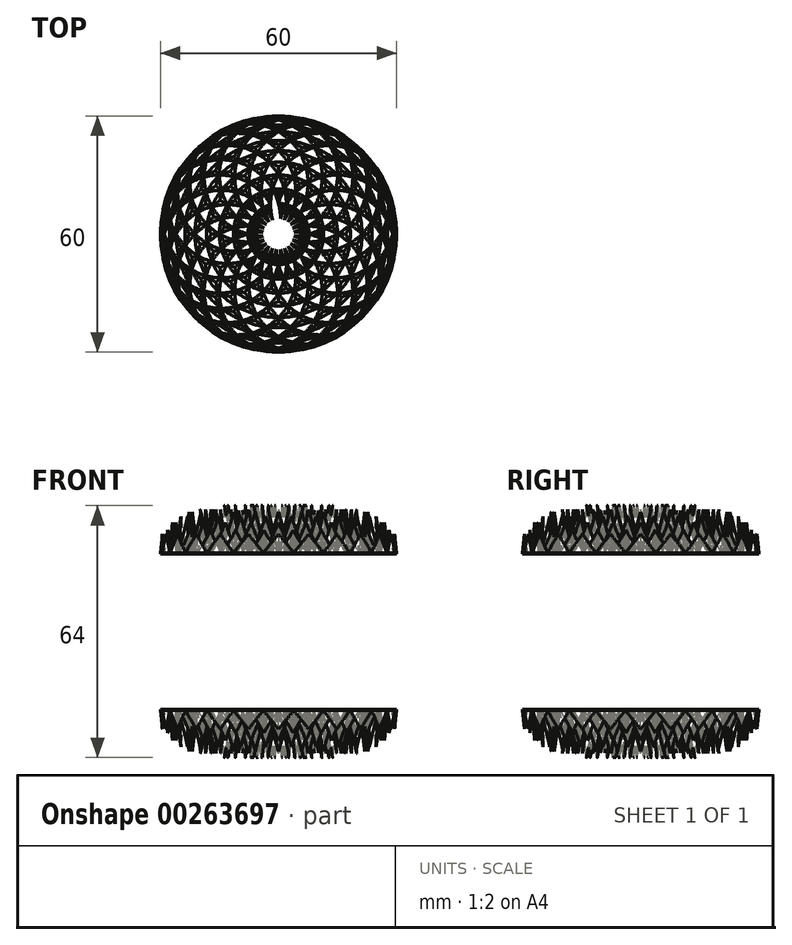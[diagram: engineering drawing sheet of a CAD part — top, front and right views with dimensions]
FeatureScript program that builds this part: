
annotation { "Feature Type Name" : "Feature", "Feature Type Description" : "" }
export const myFeature = defineFeature(function(context is Context, id is Id, definition is map)
    precondition{}
    {
        {
            var Q0;
            Q0=qCreatedBy(makeId("Top.planeOp"),FACE);
            var sketch = newSketch(context, id + "F0", { "sketchPlane" : qUnion([Q0])});
            skCircle(sketch, "E0", {"center": v(0, 0) * mm, "radius": 15 * mm});
            skLineSegment(sketch, "E1", {"start": v(-15, 0) * mm, "end": v(15, 0) * mm, "construction": true});
            skLineSegment(sketch, "E2", {"start": v(0, 15) * mm, "end": v(0, -15) * mm, "construction": true});
            skCircle(sketch, "E3", {"center": v(15, 0) * mm, "radius": 15 * mm});
            skCircle(sketch, "E4", {"center": v(7.5, 13) * mm, "radius": 15 * mm});
            skCircle(sketch, "E5", {"center": v(7.5, -13) * mm, "radius": 15 * mm});
            skCircle(sketch, "E6", {"center": v(-7.5, 13) * mm, "radius": 15 * mm});
            skCircle(sketch, "E7", {"center": v(-7.5, -13) * mm, "radius": 15 * mm});
            skCircle(sketch, "E8", {"center": v(-15, 0) * mm, "radius": 15 * mm});
            skLineSegment(sketch, "E9", {"start": v(0, 0) * mm, "end": v(22.5, 13) * mm, "construction": true});
            skCircle(sketch, "E10", {"center": v(13, 7.5) * mm, "radius": 15 * mm});
            skCircle(sketch, "E11", {"center": v(13, -7.5) * mm, "radius": 15 * mm});
            skCircle(sketch, "E12", {"center": v(0, -15) * mm, "radius": 15 * mm});
            skCircle(sketch, "E13", {"center": v(-13, -7.5) * mm, "radius": 15 * mm});
            skCircle(sketch, "E14", {"center": v(-13, 7.5) * mm, "radius": 15 * mm});
            skCircle(sketch, "E15", {"center": v(0, 15) * mm, "radius": 15 * mm});
            skLineSegment(sketch, "E16", {"start": v(7.5, 2) * mm, "end": v(20.5, 5.5) * mm, "construction": true});
            skCircle(sketch, "E17", {"center": v(14.49, 3.88) * mm, "radius": 15 * mm});
            skCircle(sketch, "E18", {"center": v(10.6, -10.6) * mm, "radius": 15 * mm});
            skCircle(sketch, "E19", {"center": v(-3.88, -14.49) * mm, "radius": 15 * mm});
            skCircle(sketch, "E20", {"center": v(-14.49, -3.88) * mm, "radius": 15 * mm});
            skCircle(sketch, "E21", {"center": v(-10.6, 10.6) * mm, "radius": 15 * mm});
            skCircle(sketch, "E22", {"center": v(3.88, 14.49) * mm, "radius": 15 * mm});
            skLineSegment(sketch, "E23", {"start": v(-2, 7.5) * mm, "end": v(-5.5, 20.5) * mm, "construction": true});
            skCircle(sketch, "E24", {"center": v(-3.88, 14.49) * mm, "radius": 15 * mm});
            skCircle(sketch, "E25", {"center": v(10.6, 10.6) * mm, "radius": 15 * mm});
            skCircle(sketch, "E26", {"center": v(14.49, -3.88) * mm, "radius": 15 * mm});
            skCircle(sketch, "E27", {"center": v(3.88, -14.49) * mm, "radius": 15 * mm});
            skCircle(sketch, "E28", {"center": v(-10.6, -10.6) * mm, "radius": 15 * mm});
            skCircle(sketch, "E29", {"center": v(-14.49, 3.88) * mm, "radius": 15 * mm});
            skCircle(sketch, "E30", {"center": v(0, 0) * mm, "radius": 18.26 * mm});
            skLineSegment(sketch, "E31", {"start": v(-6.99, 16.87) * mm, "end": v(-2.38, 18.1) * mm, "construction": true});
            skCircle(sketch, "E32", {"center": v(0, 0) * mm, "radius": 21.21 * mm});
            skLineSegment(sketch, "E33", {"start": v(0, 0) * mm, "end": v(7.5, 28) * mm, "construction": true});
            skCircle(sketch, "E34", {"center": v(0, 0) * mm, "radius": 28.98 * mm});
            skLineSegment(sketch, "E35", {"start": v(0, 0) * mm, "end": v(3.1, 23.6) * mm, "construction": true});
            skCircle(sketch, "E36", {"center": v(0, 0) * mm, "radius": 23.8 * mm});
            skLineSegment(sketch, "E37", {"start": v(0, 0) * mm, "end": v(-3.62, 27.48) * mm, "construction": true});
            skCircle(sketch, "E38", {"center": v(0, 0) * mm, "radius": 27.72 * mm});
            skLineSegment(sketch, "E39", {"start": v(0, 0) * mm, "end": v(-13, 22.5) * mm, "construction": true});
            skCircle(sketch, "E40", {"center": v(0, 0) * mm, "radius": 25.98 * mm});
            skLineSegment(sketch, "E41", {"start": v(0, 0) * mm, "end": v(-9.1, 6.99) * mm, "construction": true});
            skCircle(sketch, "E42", {"center": v(0, 0) * mm, "radius": 11.48 * mm});
            skLineSegment(sketch, "E43", {"start": v(0, 0) * mm, "end": v(-6.72, 3.88) * mm, "construction": true});
            skCircle(sketch, "E44", {"center": v(0, 0) * mm, "radius": 7.76 * mm});
            skLineSegment(sketch, "E45", {"start": v(0, 0) * mm, "end": v(-2.38, -3.1) * mm, "construction": true});
            skCircle(sketch, "E46", {"center": v(0, 0) * mm, "radius": 3.92 * mm});
            skSolve(sketch);
        }
        {
            var Q0;
            Q0=qCreatedBy(makeId("Top.planeOp"),FACE);
            cPlane(context, id + "F1", {"entities" : qUnion([Q0]), "cplaneType" : CPlaneType.OFFSET, "offset" : 0 * mm, "width" : 150 * mm, "height" : 150 * mm});
        }
        {
            var Q0;
            Q0=qCreatedBy(id+"F1.planeOp",FACE);
            var sketch = newSketch(context, id + "F2", { "sketchPlane" : qUnion([Q0])});
            skArc(sketch, "E47.0.0", {"start": v(-7.5, 2) * mm, "mid": v(-9.46, 1.88) * mm, "end": v(-11.38, 1.5) * mm});
            skArc(sketch, "E47.0.1", {"start": v(-11.38, 1.5) * mm, "mid": v(-9.62, 0.63) * mm, "end": v(-7.76, 0) * mm});
            skArc(sketch, "E48.0.1", {"start": v(-6.72, 3.88) * mm, "mid": v(-8.65, 4.27) * mm, "end": v(-10.6, 4.4) * mm});
            skArc(sketch, "E48.0.2", {"start": v(-10.6, 4.4) * mm, "mid": v(-9.13, 3.1) * mm, "end": v(-7.5, 2) * mm});
            skArc(sketch, "E49.0.1", {"start": v(-5.5, 5.5) * mm, "mid": v(-7.25, 6.36) * mm, "end": v(-9.1, 6.99) * mm});
            skArc(sketch, "E49.0.2", {"start": v(-9.1, 6.99) * mm, "mid": v(-8.02, 5.36) * mm, "end": v(-6.72, 3.88) * mm});
            skArc(sketch, "E50.0.0", {"start": v(-3.88, 6.72) * mm, "mid": v(-5.36, 8.02) * mm, "end": v(-6.99, 9.1) * mm});
            skArc(sketch, "E50.0.1", {"start": v(-6.99, 9.1) * mm, "mid": v(-6.36, 7.25) * mm, "end": v(-5.5, 5.5) * mm});
            skArc(sketch, "E51.0.1", {"start": v(-2, 7.5) * mm, "mid": v(-3.1, 9.13) * mm, "end": v(-4.4, 10.6) * mm});
            skArc(sketch, "E51.0.2", {"start": v(-4.4, 10.6) * mm, "mid": v(-4.27, 8.65) * mm, "end": v(-3.88, 6.72) * mm});
            skArc(sketch, "E52.0.1", {"start": v(0, 7.76) * mm, "mid": v(-0.63, 9.62) * mm, "end": v(-1.5, 11.38) * mm});
            skArc(sketch, "E52.0.2", {"start": v(-1.5, 11.38) * mm, "mid": v(-1.88, 9.46) * mm, "end": v(-2, 7.5) * mm});
            skArc(sketch, "E53.0.0", {"start": v(2, 7.5) * mm, "mid": v(1.88, 9.46) * mm, "end": v(1.5, 11.38) * mm});
            skArc(sketch, "E53.0.1", {"start": v(1.5, 11.38) * mm, "mid": v(0.63, 9.62) * mm, "end": v(0, 7.76) * mm});
            skArc(sketch, "E54.0.0", {"start": v(3.88, 6.72) * mm, "mid": v(4.27, 8.65) * mm, "end": v(4.4, 10.6) * mm});
            skArc(sketch, "E54.0.1", {"start": v(4.4, 10.6) * mm, "mid": v(3.1, 9.13) * mm, "end": v(2, 7.5) * mm});
            skArc(sketch, "E55.0.0", {"start": v(5.5, 5.5) * mm, "mid": v(6.36, 7.25) * mm, "end": v(6.99, 9.1) * mm});
            skArc(sketch, "E55.0.1", {"start": v(6.99, 9.1) * mm, "mid": v(5.36, 8.02) * mm, "end": v(3.88, 6.72) * mm});
            skArc(sketch, "E56.0.1", {"start": v(6.72, 3.88) * mm, "mid": v(8.02, 5.36) * mm, "end": v(9.1, 6.99) * mm});
            skArc(sketch, "E56.0.2", {"start": v(9.1, 6.99) * mm, "mid": v(7.25, 6.36) * mm, "end": v(5.5, 5.5) * mm});
            skArc(sketch, "E57.0.1", {"start": v(7.5, 2) * mm, "mid": v(9.13, 3.1) * mm, "end": v(10.6, 4.4) * mm});
            skArc(sketch, "E57.0.2", {"start": v(10.6, 4.4) * mm, "mid": v(8.65, 4.27) * mm, "end": v(6.72, 3.88) * mm});
            skArc(sketch, "E58.0.0", {"start": v(7.76, 0) * mm, "mid": v(9.62, 0.63) * mm, "end": v(11.38, 1.5) * mm});
            skArc(sketch, "E58.0.1", {"start": v(11.38, 1.5) * mm, "mid": v(9.46, 1.88) * mm, "end": v(7.5, 2) * mm});
            skArc(sketch, "E59.0.1", {"start": v(7.5, -2) * mm, "mid": v(9.46, -1.88) * mm, "end": v(11.38, -1.5) * mm});
            skArc(sketch, "E59.0.2", {"start": v(11.38, -1.5) * mm, "mid": v(9.62, -0.63) * mm, "end": v(7.76, 0) * mm});
            skArc(sketch, "E60.0.1", {"start": v(6.72, -3.88) * mm, "mid": v(8.65, -4.27) * mm, "end": v(10.6, -4.4) * mm});
            skArc(sketch, "E60.0.2", {"start": v(10.6, -4.4) * mm, "mid": v(9.13, -3.1) * mm, "end": v(7.5, -2) * mm});
            skArc(sketch, "E61.0.1", {"start": v(5.5, -5.5) * mm, "mid": v(7.25, -6.36) * mm, "end": v(9.1, -6.99) * mm});
            skArc(sketch, "E61.0.2", {"start": v(9.1, -6.99) * mm, "mid": v(8.02, -5.36) * mm, "end": v(6.72, -3.88) * mm});
            skArc(sketch, "E62.0.1", {"start": v(3.88, -6.72) * mm, "mid": v(5.36, -8.02) * mm, "end": v(6.99, -9.1) * mm});
            skArc(sketch, "E62.0.2", {"start": v(6.99, -9.1) * mm, "mid": v(6.36, -7.25) * mm, "end": v(5.5, -5.5) * mm});
            skArc(sketch, "E63.0.0", {"start": v(2, -7.5) * mm, "mid": v(3.1, -9.13) * mm, "end": v(4.4, -10.6) * mm});
            skArc(sketch, "E63.0.1", {"start": v(4.4, -10.6) * mm, "mid": v(4.27, -8.65) * mm, "end": v(3.88, -6.72) * mm});
            skArc(sketch, "E64.0.1", {"start": v(0, -7.76) * mm, "mid": v(0.63, -9.62) * mm, "end": v(1.5, -11.38) * mm});
            skArc(sketch, "E64.0.2", {"start": v(1.5, -11.38) * mm, "mid": v(1.88, -9.46) * mm, "end": v(2, -7.5) * mm});
            skArc(sketch, "E65.0.0", {"start": v(-2, -7.5) * mm, "mid": v(-1.88, -9.46) * mm, "end": v(-1.5, -11.38) * mm});
            skArc(sketch, "E65.0.1", {"start": v(-1.5, -11.38) * mm, "mid": v(-0.63, -9.62) * mm, "end": v(0, -7.76) * mm});
            skArc(sketch, "E66.0.1", {"start": v(-3.88, -6.72) * mm, "mid": v(-4.27, -8.65) * mm, "end": v(-4.4, -10.6) * mm});
            skArc(sketch, "E66.0.2", {"start": v(-4.4, -10.6) * mm, "mid": v(-3.1, -9.13) * mm, "end": v(-2, -7.5) * mm});
            skArc(sketch, "E67.0.0", {"start": v(-5.5, -5.5) * mm, "mid": v(-6.36, -7.25) * mm, "end": v(-6.99, -9.1) * mm});
            skArc(sketch, "E67.0.1", {"start": v(-6.99, -9.1) * mm, "mid": v(-5.36, -8.02) * mm, "end": v(-3.88, -6.72) * mm});
            skArc(sketch, "E68.0.1", {"start": v(-6.72, -3.88) * mm, "mid": v(-8.02, -5.36) * mm, "end": v(-9.1, -6.99) * mm});
            skArc(sketch, "E68.0.2", {"start": v(-9.1, -6.99) * mm, "mid": v(-7.25, -6.36) * mm, "end": v(-5.5, -5.5) * mm});
            skArc(sketch, "E69.0.1", {"start": v(-7.5, -2) * mm, "mid": v(-9.13, -3.1) * mm, "end": v(-10.6, -4.4) * mm});
            skArc(sketch, "E69.0.2", {"start": v(-10.6, -4.4) * mm, "mid": v(-8.65, -4.27) * mm, "end": v(-6.72, -3.88) * mm});
            skArc(sketch, "E70.0.1", {"start": v(-7.76, 0) * mm, "mid": v(-9.62, -0.63) * mm, "end": v(-11.38, -1.5) * mm});
            skArc(sketch, "E70.0.2", {"start": v(-11.38, -1.5) * mm, "mid": v(-9.46, -1.88) * mm, "end": v(-7.5, -2) * mm});
            skArc(sketch, "E71.0.1", {"start": v(-10.6, 4.4) * mm, "mid": v(-12.56, 4.27) * mm, "end": v(-14.49, 3.88) * mm});
            skArc(sketch, "E71.0.2", {"start": v(-14.49, 3.88) * mm, "mid": v(-13.01, 2.59) * mm, "end": v(-11.38, 1.5) * mm});
            skArc(sketch, "E72.0.1", {"start": v(-9.1, 6.99) * mm, "mid": v(-11.03, 7.37) * mm, "end": v(-13, 7.5) * mm});
            skArc(sketch, "E72.0.2", {"start": v(-13, 7.5) * mm, "mid": v(-11.9, 5.87) * mm, "end": v(-10.6, 4.4) * mm});
            skArc(sketch, "E73.0.1", {"start": v(-6.99, 9.1) * mm, "mid": v(-8.75, 9.98) * mm, "end": v(-10.6, 10.6) * mm});
            skArc(sketch, "E73.0.2", {"start": v(-10.6, 10.6) * mm, "mid": v(-9.98, 8.75) * mm, "end": v(-9.1, 6.99) * mm});
            skArc(sketch, "E74.0.1", {"start": v(-4.4, 10.6) * mm, "mid": v(-5.87, 11.9) * mm, "end": v(-7.5, 13) * mm});
            skArc(sketch, "E74.0.2", {"start": v(-7.5, 13) * mm, "mid": v(-7.37, 11.03) * mm, "end": v(-6.99, 9.1) * mm});
            skArc(sketch, "E75.0.1", {"start": v(-1.5, 11.38) * mm, "mid": v(-2.59, 13.01) * mm, "end": v(-3.88, 14.49) * mm});
            skArc(sketch, "E75.0.2", {"start": v(-3.88, 14.49) * mm, "mid": v(-4.27, 12.56) * mm, "end": v(-4.4, 10.6) * mm});
            skArc(sketch, "E76.0.0", {"start": v(1.5, 11.38) * mm, "mid": v(0.87, 13.24) * mm, "end": v(0, 15) * mm});
            skArc(sketch, "E76.0.1", {"start": v(0, 15) * mm, "mid": v(-0.87, 13.24) * mm, "end": v(-1.5, 11.38) * mm});
            skArc(sketch, "E77.0.1", {"start": v(4.4, 10.6) * mm, "mid": v(4.27, 12.56) * mm, "end": v(3.88, 14.49) * mm});
            skArc(sketch, "E77.0.2", {"start": v(3.88, 14.49) * mm, "mid": v(2.59, 13.01) * mm, "end": v(1.5, 11.38) * mm});
            skArc(sketch, "E78.0.1", {"start": v(6.99, 9.1) * mm, "mid": v(7.37, 11.03) * mm, "end": v(7.5, 13) * mm});
            skArc(sketch, "E78.0.2", {"start": v(7.5, 13) * mm, "mid": v(5.87, 11.9) * mm, "end": v(4.4, 10.6) * mm});
            skArc(sketch, "E79.0.1", {"start": v(9.1, 6.99) * mm, "mid": v(9.98, 8.75) * mm, "end": v(10.6, 10.6) * mm});
            skArc(sketch, "E79.0.2", {"start": v(10.6, 10.6) * mm, "mid": v(8.75, 9.98) * mm, "end": v(6.99, 9.1) * mm});
            skArc(sketch, "E80.0.0", {"start": v(10.6, 4.4) * mm, "mid": v(11.9, 5.87) * mm, "end": v(13, 7.5) * mm});
            skArc(sketch, "E80.0.1", {"start": v(13, 7.5) * mm, "mid": v(11.03, 7.37) * mm, "end": v(9.1, 6.99) * mm});
            skArc(sketch, "E81.0.1", {"start": v(11.38, 1.5) * mm, "mid": v(13.01, 2.59) * mm, "end": v(14.49, 3.88) * mm});
            skArc(sketch, "E81.0.2", {"start": v(14.49, 3.88) * mm, "mid": v(12.56, 4.27) * mm, "end": v(10.6, 4.4) * mm});
            skArc(sketch, "E82.0.0", {"start": v(11.38, -1.5) * mm, "mid": v(13.24, -0.87) * mm, "end": v(15, 0) * mm});
            skArc(sketch, "E82.0.1", {"start": v(15, 0) * mm, "mid": v(13.24, 0.87) * mm, "end": v(11.38, 1.5) * mm});
            skArc(sketch, "E83.0.1", {"start": v(10.6, -4.4) * mm, "mid": v(12.56, -4.27) * mm, "end": v(14.49, -3.88) * mm});
            skArc(sketch, "E83.0.2", {"start": v(14.49, -3.88) * mm, "mid": v(13.01, -2.59) * mm, "end": v(11.38, -1.5) * mm});
            skArc(sketch, "E84.0.1", {"start": v(9.1, -6.99) * mm, "mid": v(11.03, -7.37) * mm, "end": v(13, -7.5) * mm});
            skArc(sketch, "E84.0.2", {"start": v(13, -7.5) * mm, "mid": v(11.9, -5.87) * mm, "end": v(10.6, -4.4) * mm});
            skArc(sketch, "E85.0.1", {"start": v(6.99, -9.1) * mm, "mid": v(8.75, -9.98) * mm, "end": v(10.6, -10.6) * mm});
            skArc(sketch, "E85.0.2", {"start": v(10.6, -10.6) * mm, "mid": v(9.98, -8.75) * mm, "end": v(9.1, -6.99) * mm});
            skArc(sketch, "E86.0.0", {"start": v(4.4, -10.6) * mm, "mid": v(5.87, -11.9) * mm, "end": v(7.5, -13) * mm});
            skArc(sketch, "E86.0.1", {"start": v(7.5, -13) * mm, "mid": v(7.37, -11.03) * mm, "end": v(6.99, -9.1) * mm});
            skArc(sketch, "E87.0.1", {"start": v(1.5, -11.38) * mm, "mid": v(2.59, -13.01) * mm, "end": v(3.88, -14.49) * mm});
            skArc(sketch, "E87.0.2", {"start": v(3.88, -14.49) * mm, "mid": v(4.27, -12.56) * mm, "end": v(4.4, -10.6) * mm});
            skArc(sketch, "E88.0.1", {"start": v(-1.5, -11.38) * mm, "mid": v(-0.87, -13.24) * mm, "end": v(0, -15) * mm});
            skArc(sketch, "E88.0.2", {"start": v(0, -15) * mm, "mid": v(0.87, -13.24) * mm, "end": v(1.5, -11.38) * mm});
            skArc(sketch, "E89.0.1", {"start": v(-4.4, -10.6) * mm, "mid": v(-4.27, -12.56) * mm, "end": v(-3.88, -14.49) * mm});
            skArc(sketch, "E89.0.2", {"start": v(-3.88, -14.49) * mm, "mid": v(-2.59, -13.01) * mm, "end": v(-1.5, -11.38) * mm});
            skArc(sketch, "E90.0.1", {"start": v(-6.99, -9.1) * mm, "mid": v(-7.37, -11.03) * mm, "end": v(-7.5, -13) * mm});
            skArc(sketch, "E90.0.2", {"start": v(-7.5, -13) * mm, "mid": v(-5.87, -11.9) * mm, "end": v(-4.4, -10.6) * mm});
            skArc(sketch, "E91.0.0", {"start": v(-9.1, -6.99) * mm, "mid": v(-9.98, -8.75) * mm, "end": v(-10.6, -10.6) * mm});
            skArc(sketch, "E91.0.1", {"start": v(-10.6, -10.6) * mm, "mid": v(-8.75, -9.98) * mm, "end": v(-6.99, -9.1) * mm});
            skArc(sketch, "E92.0.1", {"start": v(-10.6, -4.4) * mm, "mid": v(-11.9, -5.87) * mm, "end": v(-13, -7.5) * mm});
            skArc(sketch, "E92.0.2", {"start": v(-13, -7.5) * mm, "mid": v(-11.03, -7.37) * mm, "end": v(-9.1, -6.99) * mm});
            skArc(sketch, "E93.0.0", {"start": v(-11.38, -1.5) * mm, "mid": v(-13.01, -2.59) * mm, "end": v(-14.49, -3.88) * mm});
            skArc(sketch, "E93.0.1", {"start": v(-14.49, -3.88) * mm, "mid": v(-12.56, -4.27) * mm, "end": v(-10.6, -4.4) * mm});
            skArc(sketch, "E94.0.1", {"start": v(-11.38, 1.5) * mm, "mid": v(-13.24, 0.87) * mm, "end": v(-15, 0) * mm});
            skArc(sketch, "E94.0.2", {"start": v(-15, 0) * mm, "mid": v(-13.24, -0.87) * mm, "end": v(-11.38, -1.5) * mm});
            skArc(sketch, "E95.0.0", {"start": v(-3.88, 6.72) * mm, "mid": v(-2.59, 5.25) * mm, "end": v(-1.5, 3.62) * mm});
            skArc(sketch, "E95.0.1", {"start": v(-1.5, 3.62) * mm, "mid": v(-1.88, 5.54) * mm, "end": v(-2, 7.5) * mm});
            skArc(sketch, "E95.0.2", {"start": v(-2, 7.5) * mm, "mid": v(-2.97, 7.17) * mm, "end": v(-3.88, 6.72) * mm});
            skArc(sketch, "E96.0.0", {"start": v(-2.38, 3.1) * mm, "mid": v(-3.25, 4.87) * mm, "end": v(-3.88, 6.72) * mm});
            skArc(sketch, "E96.0.1", {"start": v(-3.88, 6.72) * mm, "mid": v(-4.73, 6.16) * mm, "end": v(-5.5, 5.5) * mm});
            skArc(sketch, "E96.0.2", {"start": v(-5.5, 5.5) * mm, "mid": v(-3.86, 4.4) * mm, "end": v(-2.38, 3.1) * mm});
            skArc(sketch, "E97.0.0", {"start": v(-6.72, 3.88) * mm, "mid": v(-4.87, 3.25) * mm, "end": v(-3.1, 2.38) * mm});
            skArc(sketch, "E97.0.1", {"start": v(-3.1, 2.38) * mm, "mid": v(-4.4, 3.86) * mm, "end": v(-5.5, 5.5) * mm});
            skArc(sketch, "E98.0.0", {"start": v(-3.62, 1.5) * mm, "mid": v(-5.25, 2.59) * mm, "end": v(-6.72, 3.88) * mm});
            skArc(sketch, "E98.0.1", {"start": v(-6.72, 3.88) * mm, "mid": v(-7.17, 2.97) * mm, "end": v(-7.5, 2) * mm});
            skArc(sketch, "E98.0.2", {"start": v(-7.5, 2) * mm, "mid": v(-5.54, 1.88) * mm, "end": v(-3.62, 1.5) * mm});
            skArc(sketch, "E99.0.0", {"start": v(-3.88, 0.51) * mm, "mid": v(-5.74, 1.14) * mm, "end": v(-7.5, 2) * mm});
            skArc(sketch, "E99.0.1", {"start": v(-7.5, 2) * mm, "mid": v(-7.7, 1.01) * mm, "end": v(-7.76, 0) * mm});
            skArc(sketch, "E99.0.2", {"start": v(-7.76, 0) * mm, "mid": v(-5.84, 0.38) * mm, "end": v(-3.88, 0.51) * mm});
            skArc(sketch, "E100.0.0", {"start": v(-3.88, -0.51) * mm, "mid": v(-5.84, -0.38) * mm, "end": v(-7.76, 0) * mm});
            skArc(sketch, "E100.0.1", {"start": v(-7.76, 0) * mm, "mid": v(-7.7, -1.01) * mm, "end": v(-7.5, -2) * mm});
            skArc(sketch, "E100.0.2", {"start": v(-7.5, -2) * mm, "mid": v(-5.74, -1.14) * mm, "end": v(-3.88, -0.51) * mm});
            skArc(sketch, "E101.0.0", {"start": v(-3.62, -1.5) * mm, "mid": v(-5.54, -1.88) * mm, "end": v(-7.5, -2) * mm});
            skArc(sketch, "E101.0.1", {"start": v(-7.5, -2) * mm, "mid": v(-7.17, -2.97) * mm, "end": v(-6.72, -3.88) * mm});
            skArc(sketch, "E101.0.2", {"start": v(-6.72, -3.88) * mm, "mid": v(-5.25, -2.59) * mm, "end": v(-3.62, -1.5) * mm});
            skArc(sketch, "E102.0.0", {"start": v(-5.5, -5.5) * mm, "mid": v(-4.4, -3.86) * mm, "end": v(-3.1, -2.38) * mm});
            skArc(sketch, "E102.0.1", {"start": v(-3.1, -2.38) * mm, "mid": v(-4.87, -3.25) * mm, "end": v(-6.72, -3.88) * mm});
            skArc(sketch, "E102.0.2", {"start": v(-6.72, -3.88) * mm, "mid": v(-6.16, -4.73) * mm, "end": v(-5.5, -5.5) * mm});
            skArc(sketch, "E103.0.0", {"start": v(-2.38, -3.1) * mm, "mid": v(-3.86, -4.4) * mm, "end": v(-5.5, -5.5) * mm});
            skArc(sketch, "E103.0.1", {"start": v(-5.5, -5.5) * mm, "mid": v(-4.73, -6.16) * mm, "end": v(-3.88, -6.72) * mm});
            skArc(sketch, "E103.0.2", {"start": v(-3.88, -6.72) * mm, "mid": v(-3.25, -4.87) * mm, "end": v(-2.38, -3.1) * mm});
            skArc(sketch, "E104.0.0", {"start": v(-1.5, -3.62) * mm, "mid": v(-2.59, -5.25) * mm, "end": v(-3.88, -6.72) * mm});
            skArc(sketch, "E104.0.1", {"start": v(-3.88, -6.72) * mm, "mid": v(-2.97, -7.17) * mm, "end": v(-2, -7.5) * mm});
            skArc(sketch, "E104.0.2", {"start": v(-2, -7.5) * mm, "mid": v(-1.88, -5.54) * mm, "end": v(-1.5, -3.62) * mm});
            skArc(sketch, "E105.0.0", {"start": v(0, -7.76) * mm, "mid": v(-0.38, -5.84) * mm, "end": v(-0.51, -3.88) * mm});
            skArc(sketch, "E105.0.1", {"start": v(-0.51, -3.88) * mm, "mid": v(-1.14, -5.74) * mm, "end": v(-2, -7.5) * mm});
            skArc(sketch, "E105.0.2", {"start": v(-2, -7.5) * mm, "mid": v(-1.01, -7.7) * mm, "end": v(0, -7.76) * mm});
            skArc(sketch, "E106.0.0", {"start": v(0.51, -3.88) * mm, "mid": v(0.38, -5.84) * mm, "end": v(0, -7.76) * mm});
            skArc(sketch, "E106.0.1", {"start": v(0, -7.76) * mm, "mid": v(1.01, -7.7) * mm, "end": v(2, -7.5) * mm});
            skArc(sketch, "E106.0.2", {"start": v(2, -7.5) * mm, "mid": v(1.14, -5.74) * mm, "end": v(0.51, -3.88) * mm});
            skArc(sketch, "E107.0.0", {"start": v(1.5, -3.62) * mm, "mid": v(1.88, -5.54) * mm, "end": v(2, -7.5) * mm});
            skArc(sketch, "E107.0.1", {"start": v(2, -7.5) * mm, "mid": v(2.97, -7.17) * mm, "end": v(3.88, -6.72) * mm});
            skArc(sketch, "E107.0.2", {"start": v(3.88, -6.72) * mm, "mid": v(2.59, -5.25) * mm, "end": v(1.5, -3.62) * mm});
            skArc(sketch, "E108.0.0", {"start": v(2.38, -3.1) * mm, "mid": v(3.25, -4.87) * mm, "end": v(3.88, -6.72) * mm});
            skArc(sketch, "E108.0.1", {"start": v(3.88, -6.72) * mm, "mid": v(4.73, -6.16) * mm, "end": v(5.5, -5.5) * mm});
            skArc(sketch, "E108.0.2", {"start": v(5.5, -5.5) * mm, "mid": v(3.86, -4.4) * mm, "end": v(2.38, -3.1) * mm});
            skArc(sketch, "E109.0.0", {"start": v(3.1, -2.38) * mm, "mid": v(4.4, -3.86) * mm, "end": v(5.5, -5.5) * mm});
            skArc(sketch, "E109.0.1", {"start": v(5.5, -5.5) * mm, "mid": v(6.16, -4.73) * mm, "end": v(6.72, -3.88) * mm});
            skArc(sketch, "E109.0.2", {"start": v(6.72, -3.88) * mm, "mid": v(4.87, -3.25) * mm, "end": v(3.1, -2.38) * mm});
            skArc(sketch, "E110.0.0", {"start": v(7.5, -2) * mm, "mid": v(5.54, -1.88) * mm, "end": v(3.62, -1.5) * mm});
            skArc(sketch, "E110.0.1", {"start": v(3.62, -1.5) * mm, "mid": v(5.25, -2.59) * mm, "end": v(6.72, -3.88) * mm});
            skArc(sketch, "E110.0.2", {"start": v(6.72, -3.88) * mm, "mid": v(7.17, -2.97) * mm, "end": v(7.5, -2) * mm});
            skArc(sketch, "E111.0.0", {"start": v(3.88, -0.51) * mm, "mid": v(5.74, -1.14) * mm, "end": v(7.5, -2) * mm});
            skArc(sketch, "E111.0.1", {"start": v(7.5, -2) * mm, "mid": v(7.7, -1.01) * mm, "end": v(7.76, 0) * mm});
            skArc(sketch, "E111.0.2", {"start": v(7.76, 0) * mm, "mid": v(5.84, -0.38) * mm, "end": v(3.88, -0.51) * mm});
            skArc(sketch, "E112.0.0", {"start": v(7.5, 2) * mm, "mid": v(5.74, 1.14) * mm, "end": v(3.88, 0.51) * mm});
            skArc(sketch, "E112.0.1", {"start": v(3.88, 0.51) * mm, "mid": v(5.84, 0.38) * mm, "end": v(7.76, 0) * mm});
            skArc(sketch, "E112.0.2", {"start": v(7.76, 0) * mm, "mid": v(7.7, 1.01) * mm, "end": v(7.5, 2) * mm});
            skArc(sketch, "E113.0.0", {"start": v(6.72, 3.88) * mm, "mid": v(5.25, 2.59) * mm, "end": v(3.62, 1.5) * mm});
            skArc(sketch, "E113.0.1", {"start": v(3.62, 1.5) * mm, "mid": v(5.54, 1.88) * mm, "end": v(7.5, 2) * mm});
            skArc(sketch, "E113.0.2", {"start": v(7.5, 2) * mm, "mid": v(7.17, 2.97) * mm, "end": v(6.72, 3.88) * mm});
            skArc(sketch, "E114.0.0", {"start": v(3.1, 2.38) * mm, "mid": v(4.87, 3.25) * mm, "end": v(6.72, 3.88) * mm});
            skArc(sketch, "E114.0.1", {"start": v(6.72, 3.88) * mm, "mid": v(6.16, 4.73) * mm, "end": v(5.5, 5.5) * mm});
            skArc(sketch, "E114.0.2", {"start": v(5.5, 5.5) * mm, "mid": v(4.4, 3.86) * mm, "end": v(3.1, 2.38) * mm});
            skArc(sketch, "E115.0.0", {"start": v(2.38, 3.1) * mm, "mid": v(3.86, 4.4) * mm, "end": v(5.5, 5.5) * mm});
            skArc(sketch, "E115.0.1", {"start": v(5.5, 5.5) * mm, "mid": v(4.73, 6.16) * mm, "end": v(3.88, 6.72) * mm});
            skArc(sketch, "E115.0.2", {"start": v(3.88, 6.72) * mm, "mid": v(3.25, 4.87) * mm, "end": v(2.38, 3.1) * mm});
            skArc(sketch, "E116.0.0", {"start": v(1.5, 3.62) * mm, "mid": v(2.59, 5.25) * mm, "end": v(3.88, 6.72) * mm});
            skArc(sketch, "E116.0.1", {"start": v(3.88, 6.72) * mm, "mid": v(2.97, 7.17) * mm, "end": v(2, 7.5) * mm});
            skArc(sketch, "E116.0.2", {"start": v(2, 7.5) * mm, "mid": v(1.88, 5.54) * mm, "end": v(1.5, 3.62) * mm});
            skArc(sketch, "E117.0.0", {"start": v(0.51, 3.88) * mm, "mid": v(1.14, 5.74) * mm, "end": v(2, 7.5) * mm});
            skArc(sketch, "E117.0.1", {"start": v(2, 7.5) * mm, "mid": v(1.01, 7.7) * mm, "end": v(0, 7.76) * mm});
            skArc(sketch, "E117.0.2", {"start": v(0, 7.76) * mm, "mid": v(0.38, 5.84) * mm, "end": v(0.51, 3.88) * mm});
            skArc(sketch, "E118.0.0", {"start": v(-2, 7.5) * mm, "mid": v(-1.14, 5.74) * mm, "end": v(-0.51, 3.88) * mm});
            skArc(sketch, "E118.0.1", {"start": v(-0.51, 3.88) * mm, "mid": v(-0.38, 5.84) * mm, "end": v(0, 7.76) * mm});
            skArc(sketch, "E118.0.2", {"start": v(0, 7.76) * mm, "mid": v(-1.01, 7.7) * mm, "end": v(-2, 7.5) * mm});
            skArc(sketch, "E119.0.0", {"start": v(0, 0) * mm, "mid": v(0.87, 1.76) * mm, "end": v(1.5, 3.62) * mm});
            skArc(sketch, "E119.0.1", {"start": v(1.5, 3.62) * mm, "mid": v(0.63, 1.86) * mm, "end": v(0, 0) * mm});
            skArc(sketch, "E120.0.0", {"start": v(0, 0) * mm, "mid": v(1.3, 1.48) * mm, "end": v(2.38, 3.1) * mm});
            skArc(sketch, "E120.0.1", {"start": v(2.38, 3.1) * mm, "mid": v(1.1, 1.63) * mm, "end": v(0, 0) * mm});
            skArc(sketch, "E121.0.0", {"start": v(3.1, 2.38) * mm, "mid": v(1.48, 1.3) * mm, "end": v(0, 0) * mm});
            skArc(sketch, "E121.0.1", {"start": v(0, 0) * mm, "mid": v(1.63, 1.1) * mm, "end": v(3.1, 2.38) * mm});
            skArc(sketch, "E122.0.0", {"start": v(3.62, 1.5) * mm, "mid": v(1.76, 0.87) * mm, "end": v(0, 0) * mm});
            skArc(sketch, "E122.0.1", {"start": v(0, 0) * mm, "mid": v(1.86, 0.63) * mm, "end": v(3.62, 1.5) * mm});
            skArc(sketch, "E123.0.0", {"start": v(3.88, 0.51) * mm, "mid": v(1.92, 0.38) * mm, "end": v(0, 0) * mm});
            skArc(sketch, "E123.0.1", {"start": v(0, 0) * mm, "mid": v(1.96, 0.13) * mm, "end": v(3.88, 0.51) * mm});
            skArc(sketch, "E124.0.0", {"start": v(3.88, -0.51) * mm, "mid": v(1.96, -0.13) * mm, "end": v(0, 0) * mm});
            skArc(sketch, "E124.0.1", {"start": v(0, 0) * mm, "mid": v(1.92, -0.38) * mm, "end": v(3.88, -0.51) * mm});
            skArc(sketch, "E125.0.0", {"start": v(3.62, -1.5) * mm, "mid": v(1.86, -0.63) * mm, "end": v(0, 0) * mm});
            skArc(sketch, "E125.0.1", {"start": v(0, 0) * mm, "mid": v(1.76, -0.87) * mm, "end": v(3.62, -1.5) * mm});
            skArc(sketch, "E126.0.0", {"start": v(3.1, -2.38) * mm, "mid": v(1.63, -1.1) * mm, "end": v(0, 0) * mm});
            skArc(sketch, "E126.0.1", {"start": v(0, 0) * mm, "mid": v(1.48, -1.3) * mm, "end": v(3.1, -2.38) * mm});
            skArc(sketch, "E127.0.0", {"start": v(0, 0) * mm, "mid": v(1.1, -1.63) * mm, "end": v(2.38, -3.1) * mm});
            skArc(sketch, "E127.0.1", {"start": v(2.38, -3.1) * mm, "mid": v(1.3, -1.48) * mm, "end": v(0, 0) * mm});
            skArc(sketch, "E128.0.0", {"start": v(0, 0) * mm, "mid": v(0.63, -1.86) * mm, "end": v(1.5, -3.62) * mm});
            skArc(sketch, "E128.0.1", {"start": v(1.5, -3.62) * mm, "mid": v(0.87, -1.76) * mm, "end": v(0, 0) * mm});
            skArc(sketch, "E129.0.0", {"start": v(0, 0) * mm, "mid": v(0.13, -1.96) * mm, "end": v(0.51, -3.88) * mm});
            skArc(sketch, "E129.0.1", {"start": v(0.51, -3.88) * mm, "mid": v(0.38, -1.92) * mm, "end": v(0, 0) * mm});
            skArc(sketch, "E130.0.0", {"start": v(-0.51, -3.88) * mm, "mid": v(-0.13, -1.96) * mm, "end": v(0, 0) * mm});
            skArc(sketch, "E130.0.1", {"start": v(0, 0) * mm, "mid": v(-0.38, -1.92) * mm, "end": v(-0.51, -3.88) * mm});
            skArc(sketch, "E131.0.0", {"start": v(0, 0) * mm, "mid": v(-0.87, -1.76) * mm, "end": v(-1.5, -3.62) * mm});
            skArc(sketch, "E131.0.1", {"start": v(-1.5, -3.62) * mm, "mid": v(-0.63, -1.86) * mm, "end": v(0, 0) * mm});
            skArc(sketch, "E132.0.0", {"start": v(0, 0) * mm, "mid": v(-1.3, -1.48) * mm, "end": v(-2.38, -3.1) * mm});
            skArc(sketch, "E132.0.1", {"start": v(-2.38, -3.1) * mm, "mid": v(-1.1, -1.63) * mm, "end": v(0, 0) * mm});
            skArc(sketch, "E133.0.0", {"start": v(-3.1, -2.38) * mm, "mid": v(-1.48, -1.3) * mm, "end": v(0, 0) * mm});
            skArc(sketch, "E133.0.1", {"start": v(0, 0) * mm, "mid": v(-1.63, -1.1) * mm, "end": v(-3.1, -2.38) * mm});
            skArc(sketch, "E134.0.0", {"start": v(-3.62, -1.5) * mm, "mid": v(-1.76, -0.87) * mm, "end": v(0, 0) * mm});
            skArc(sketch, "E134.0.1", {"start": v(0, 0) * mm, "mid": v(-1.86, -0.63) * mm, "end": v(-3.62, -1.5) * mm});
            skArc(sketch, "E135.0.0", {"start": v(0, 0) * mm, "mid": v(-1.96, -0.13) * mm, "end": v(-3.88, -0.51) * mm});
            skArc(sketch, "E135.0.1", {"start": v(-3.88, -0.51) * mm, "mid": v(-1.92, -0.38) * mm, "end": v(0, 0) * mm});
            skArc(sketch, "E136.0.0", {"start": v(0, 0) * mm, "mid": v(-1.92, 0.38) * mm, "end": v(-3.88, 0.51) * mm});
            skArc(sketch, "E136.0.1", {"start": v(-3.88, 0.51) * mm, "mid": v(-1.96, 0.13) * mm, "end": v(0, 0) * mm});
            skArc(sketch, "E137.0.0", {"start": v(0, 0) * mm, "mid": v(-1.76, 0.87) * mm, "end": v(-3.62, 1.5) * mm});
            skArc(sketch, "E137.0.1", {"start": v(-3.62, 1.5) * mm, "mid": v(-1.86, 0.63) * mm, "end": v(0, 0) * mm});
            skArc(sketch, "E138.0.0", {"start": v(-3.1, 2.38) * mm, "mid": v(-1.63, 1.1) * mm, "end": v(0, 0) * mm});
            skArc(sketch, "E138.0.1", {"start": v(0, 0) * mm, "mid": v(-1.48, 1.3) * mm, "end": v(-3.1, 2.38) * mm});
            skArc(sketch, "E139.0.0", {"start": v(-2.38, 3.1) * mm, "mid": v(-1.3, 1.48) * mm, "end": v(0, 0) * mm});
            skArc(sketch, "E139.0.1", {"start": v(0, 0) * mm, "mid": v(-1.1, 1.63) * mm, "end": v(-2.38, 3.1) * mm});
            skArc(sketch, "E140.0.0", {"start": v(-1.5, 3.62) * mm, "mid": v(-0.87, 1.76) * mm, "end": v(0, 0) * mm});
            skArc(sketch, "E140.0.1", {"start": v(0, 0) * mm, "mid": v(-0.63, 1.86) * mm, "end": v(-1.5, 3.62) * mm});
            skArc(sketch, "E141.0.0", {"start": v(0, 0) * mm, "mid": v(-0.13, 1.96) * mm, "end": v(-0.51, 3.88) * mm});
            skArc(sketch, "E141.0.1", {"start": v(-0.51, 3.88) * mm, "mid": v(-0.38, 1.92) * mm, "end": v(0, 0) * mm});
            skArc(sketch, "E142.0.0", {"start": v(0, 0) * mm, "mid": v(0.38, 1.92) * mm, "end": v(0.51, 3.88) * mm});
            skArc(sketch, "E142.0.1", {"start": v(0.51, 3.88) * mm, "mid": v(0.13, 1.96) * mm, "end": v(0, 0) * mm});
            skCircle(sketch, "E143.0", {"center": v(0, 0) * mm, "radius": 7.76 * mm});
            skCircle(sketch, "E144.0", {"center": v(0, 0) * mm, "radius": 11.48 * mm});
            skCircle(sketch, "E145.0", {"center": v(0, 0) * mm, "radius": 15 * mm});
            skCircle(sketch, "E146.0", {"center": v(0, 0) * mm, "radius": 18.26 * mm});
            skCircle(sketch, "E147.0", {"center": v(0, 0) * mm, "radius": 21.21 * mm});
            skCircle(sketch, "E148.0", {"center": v(0, 0) * mm, "radius": 23.8 * mm});
            skCircle(sketch, "E149.0", {"center": v(0, 0) * mm, "radius": 25.98 * mm});
            skCircle(sketch, "E150.0", {"center": v(0, 0) * mm, "radius": 27.72 * mm});
            skCircle(sketch, "E151.0", {"center": v(0, 0) * mm, "radius": 28.98 * mm});
            skSolve(sketch);
        }
        {
            var Q0;
            Q0=makeQuery(id+"F2.imprint","IMPRINT",FACE,{"disambiguationData":[TD([[makeQuery(id+"F2.imprint","IMPRINT",EDGE,{"derivedFrom":sQuery(id+"F2.wireOp",EDGE,"E117.0.2")}),-1.0]])]});
            var Q1;
            Q1=makeQuery(id+"F2.imprint","IMPRINT",FACE,{"disambiguationData":[TD([[makeQuery(id+"F2.imprint","IMPRINT",EDGE,{"derivedFrom":sQuery(id+"F2.wireOp",EDGE,"E116.0.2")}),-1.0]])]});
            var Q2;
            Q2=makeQuery(id+"F2.imprint","IMPRINT",FACE,{"disambiguationData":[TD([[makeQuery(id+"F2.imprint","IMPRINT",EDGE,{"derivedFrom":sQuery(id+"F2.wireOp",EDGE,"E115.0.2")}),-1.0]])]});
            var Q3;
            Q3=makeQuery(id+"F2.imprint","IMPRINT",FACE,{"disambiguationData":[TD([[makeQuery(id+"F2.imprint","IMPRINT",EDGE,{"derivedFrom":sQuery(id+"F2.wireOp",EDGE,"E114.0.2")}),-1.0]])]});
            var Q4;
            Q4=makeQuery(id+"F2.imprint","IMPRINT",FACE,{"disambiguationData":[TD([[makeQuery(id+"F2.imprint","IMPRINT",EDGE,{"derivedFrom":sQuery(id+"F2.wireOp",EDGE,"E113.0.0")}),-1.0]])]});
            var Q5;
            Q5=makeQuery(id+"F2.imprint","IMPRINT",FACE,{"disambiguationData":[TD([[makeQuery(id+"F2.imprint","IMPRINT",EDGE,{"derivedFrom":sQuery(id+"F2.wireOp",EDGE,"E112.0.0")}),-1.0]])]});
            var Q6;
            Q6=makeQuery(id+"F2.imprint","IMPRINT",FACE,{"disambiguationData":[TD([[makeQuery(id+"F2.imprint","IMPRINT",EDGE,{"derivedFrom":sQuery(id+"F2.wireOp",EDGE,"E111.0.2")}),-1.0]])]});
            var Q7;
            Q7=makeQuery(id+"F2.imprint","IMPRINT",FACE,{"disambiguationData":[TD([[makeQuery(id+"F2.imprint","IMPRINT",EDGE,{"derivedFrom":sQuery(id+"F2.wireOp",EDGE,"E110.0.0")}),-1.0]])]});
            var Q8;
            Q8=makeQuery(id+"F2.imprint","IMPRINT",FACE,{"disambiguationData":[TD([[makeQuery(id+"F2.imprint","IMPRINT",EDGE,{"derivedFrom":sQuery(id+"F2.wireOp",EDGE,"E109.0.2")}),-1.0]])]});
            var Q9;
            Q9=makeQuery(id+"F2.imprint","IMPRINT",FACE,{"disambiguationData":[TD([[makeQuery(id+"F2.imprint","IMPRINT",EDGE,{"derivedFrom":sQuery(id+"F2.wireOp",EDGE,"E108.0.2")}),-1.0]])]});
            var Q10;
            Q10=makeQuery(id+"F2.imprint","IMPRINT",FACE,{"disambiguationData":[TD([[makeQuery(id+"F2.imprint","IMPRINT",EDGE,{"derivedFrom":sQuery(id+"F2.wireOp",EDGE,"E106.0.2")}),-1.0]])]});
            var Q11;
            Q11=makeQuery(id+"F2.imprint","IMPRINT",FACE,{"disambiguationData":[TD([[makeQuery(id+"F2.imprint","IMPRINT",EDGE,{"derivedFrom":sQuery(id+"F2.wireOp",EDGE,"E104.0.2")}),-1.0]])]});
            var Q12;
            Q12=makeQuery(id+"F2.imprint","IMPRINT",FACE,{"disambiguationData":[TD([[makeQuery(id+"F2.imprint","IMPRINT",EDGE,{"derivedFrom":sQuery(id+"F2.wireOp",EDGE,"E103.0.2")}),-1.0]])]});
            var Q13;
            Q13=makeQuery(id+"F2.imprint","IMPRINT",FACE,{"disambiguationData":[TD([[makeQuery(id+"F2.imprint","IMPRINT",EDGE,{"derivedFrom":sQuery(id+"F2.wireOp",EDGE,"E102.0.0")}),-1.0]])]});
            var Q14;
            Q14=makeQuery(id+"F2.imprint","IMPRINT",FACE,{"disambiguationData":[TD([[makeQuery(id+"F2.imprint","IMPRINT",EDGE,{"derivedFrom":sQuery(id+"F2.wireOp",EDGE,"E101.0.2")}),-1.0]])]});
            var Q15;
            Q15=makeQuery(id+"F2.imprint","IMPRINT",FACE,{"disambiguationData":[TD([[makeQuery(id+"F2.imprint","IMPRINT",EDGE,{"derivedFrom":sQuery(id+"F2.wireOp",EDGE,"E100.0.2")}),-1.0]])]});
            var Q16;
            Q16=makeQuery(id+"F2.imprint","IMPRINT",FACE,{"disambiguationData":[TD([[makeQuery(id+"F2.imprint","IMPRINT",EDGE,{"derivedFrom":sQuery(id+"F2.wireOp",EDGE,"E99.0.2")}),-1.0]])]});
            var Q17;
            Q17=makeQuery(id+"F2.imprint","IMPRINT",FACE,{"disambiguationData":[TD([[makeQuery(id+"F2.imprint","IMPRINT",EDGE,{"derivedFrom":sQuery(id+"F2.wireOp",EDGE,"E98.0.2")}),-1.0]])]});
            var Q18;
            Q18=makeQuery(id+"F2.imprint","IMPRINT",FACE,{"disambiguationData":[TD([[makeQuery(id+"F2.imprint","IMPRINT",EDGE,{"derivedFrom":sQuery(id+"F2.wireOp",EDGE,"E96.0.2")}),-1.0]])]});
            var Q19;
            Q19=makeQuery(id+"F2.imprint","IMPRINT",FACE,{"disambiguationData":[TD([[makeQuery(id+"F2.imprint","IMPRINT",EDGE,{"derivedFrom":sQuery(id+"F2.wireOp",EDGE,"E95.0.0")}),-1.0]])]});
            var Q20;
            Q20=makeQuery(id+"F2.imprint","IMPRINT",FACE,{"disambiguationData":[TD([[makeQuery(id+"F2.imprint","IMPRINT",EDGE,{"derivedFrom":sQuery(id+"F2.wireOp",EDGE,"E95.0.1")}),-1.0]])]});
            var Q21;
            Q21=makeQuery(id+"F2.imprint","IMPRINT",FACE,{"disambiguationData":[TD([[makeQuery(id+"F2.imprint","IMPRINT",EDGE,{"derivedFrom":sQuery(id+"F2.wireOp",EDGE,"E105.0.0")}),-1.0]])]});
            var Q22;
            Q22=makeQuery(id+"F2.imprint","IMPRINT",FACE,{"disambiguationData":[TD([[makeQuery(id+"F2.imprint","IMPRINT",EDGE,{"derivedFrom":sQuery(id+"F2.wireOp",EDGE,"E107.0.2")}),-1.0]])]});
            var Q23;
            Q23=makeQuery(id+"F2.imprint","IMPRINT",FACE,{"disambiguationData":[TD([[makeQuery(id+"F2.imprint","IMPRINT",EDGE,{"derivedFrom":sQuery(id+"F2.wireOp",EDGE,"E97.0.0")}),-1.0]])]});
            extrude(context, id + "F3", {"entities" : qUnion([Q0, Q1, Q2, Q3, Q4, Q5, Q6, Q7, Q8, Q9, Q10, Q11, Q12, Q13, Q14, Q15, Q16, Q17, Q18, Q19, Q20, Q21, Q22, Q23]), "depth" : 12 * mm, "hasDraft" : true, "draftAngle" : 3 * degree, "draftPullDirection" : true});
        }
        {
            var Q0;
            {var subQ0=sQuery(id+"F0.wireOp",EDGE,"E42");var subQ1=sQuery(id+"F0.wireOp",EDGE,"E17");var subQ2=makeQuery(id+"F0.imprint","INTERSECT",VERTEX,{"derivedFrom":[sQuery(id+"F0.wireOp",EDGE,"E7"),subQ1,subQ0]});Q0=makeQuery(id+"F0.imprint","IMPRINT",FACE,{"disambiguationData":[TD([[makeQuery(id+"F0.imprint","IMPRINT",EDGE,{"disambiguationData":[TD([[subQ2,1.0]])],"derivedFrom":subQ1}),-1.0]])]});}
            var Q1;
            {var subQ0=sQuery(id+"F0.wireOp",EDGE,"E28");var subQ1=sQuery(id+"F0.wireOp",EDGE,"E0");var subQ2=makeQuery(id+"F0.imprint","INTERSECT",VERTEX,{"derivedFrom":[subQ1,sQuery(id+"F0.wireOp",EDGE,"E26"),subQ0]});Q1=makeQuery(id+"F0.imprint","IMPRINT",FACE,{"disambiguationData":[TD([[makeQuery(id+"F0.imprint","IMPRINT",EDGE,{"disambiguationData":[TD([[subQ2,-1.0]])],"derivedFrom":subQ1}),1.0]])]});}
            var Q2;
            {var subQ0=sQuery(id+"F0.wireOp",EDGE,"E7");var subQ1=sQuery(id+"F0.wireOp",EDGE,"E0");var subQ2=makeQuery(id+"F0.imprint","INTERSECT",VERTEX,{"derivedFrom":[subQ1,sQuery(id+"F0.wireOp",EDGE,"E3"),subQ0]});Q2=makeQuery(id+"F0.imprint","IMPRINT",FACE,{"disambiguationData":[TD([[makeQuery(id+"F0.imprint","IMPRINT",EDGE,{"disambiguationData":[TD([[subQ2,-1.0]])],"derivedFrom":subQ1}),1.0]])]});}
            var Q3;
            {var subQ0=sQuery(id+"F0.wireOp",EDGE,"E42");var subQ1=sQuery(id+"F0.wireOp",EDGE,"E7");var subQ2=makeQuery(id+"F0.imprint","INTERSECT",VERTEX,{"derivedFrom":[subQ1,sQuery(id+"F0.wireOp",EDGE,"E17"),subQ0]});Q3=makeQuery(id+"F0.imprint","IMPRINT",FACE,{"disambiguationData":[TD([[makeQuery(id+"F0.imprint","IMPRINT",EDGE,{"disambiguationData":[TD([[subQ2,-1.0]])],"derivedFrom":subQ1}),-1.0]])]});}
            var Q4;
            {var subQ0=sQuery(id+"F0.wireOp",EDGE,"E19");var subQ1=sQuery(id+"F0.wireOp",EDGE,"E0");var subQ2=makeQuery(id+"F0.imprint","INTERSECT",VERTEX,{"derivedFrom":[subQ1,sQuery(id+"F0.wireOp",EDGE,"E17"),subQ0]});Q4=makeQuery(id+"F0.imprint","IMPRINT",FACE,{"disambiguationData":[TD([[makeQuery(id+"F0.imprint","IMPRINT",EDGE,{"disambiguationData":[TD([[subQ2,-1.0]])],"derivedFrom":subQ1}),1.0]])]});}
            var Q5;
            {var subQ0=sQuery(id+"F0.wireOp",EDGE,"E13");var subQ1=sQuery(id+"F0.wireOp",EDGE,"E3");var subQ2=makeQuery(id+"F0.imprint","INTERSECT",VERTEX,{"derivedFrom":[subQ1,subQ0,sQuery(id+"F0.wireOp",EDGE,"E44")]});Q5=makeQuery(id+"F0.imprint","IMPRINT",FACE,{"disambiguationData":[TD([[makeQuery(id+"F0.imprint","IMPRINT",EDGE,{"disambiguationData":[TD([[subQ2,-1.0]])],"derivedFrom":subQ1}),-1.0]])]});}
            var Q6;
            {var subQ0=sQuery(id+"F0.wireOp",EDGE,"E42");var subQ1=sQuery(id+"F0.wireOp",EDGE,"E20");var subQ2=makeQuery(id+"F0.imprint","INTERSECT",VERTEX,{"derivedFrom":[sQuery(id+"F0.wireOp",EDGE,"E11"),subQ1,subQ0]});Q6=makeQuery(id+"F0.imprint","IMPRINT",FACE,{"disambiguationData":[TD([[makeQuery(id+"F0.imprint","IMPRINT",EDGE,{"disambiguationData":[TD([[subQ2,-1.0]])],"derivedFrom":subQ1}),-1.0]])]});}
            var Q7;
            {var subQ0=sQuery(id+"F0.wireOp",EDGE,"E42");var subQ1=sQuery(id+"F0.wireOp",EDGE,"E8");var subQ2=makeQuery(id+"F0.imprint","INTERSECT",VERTEX,{"derivedFrom":[subQ1,sQuery(id+"F0.wireOp",EDGE,"E18"),subQ0]});Q7=makeQuery(id+"F0.imprint","IMPRINT",FACE,{"disambiguationData":[TD([[makeQuery(id+"F0.imprint","IMPRINT",EDGE,{"disambiguationData":[TD([[subQ2,-1.0]])],"derivedFrom":subQ1}),-1.0]])]});}
            var Q8;
            {var subQ0=sQuery(id+"F0.wireOp",EDGE,"E42");var subQ1=sQuery(id+"F0.wireOp",EDGE,"E18");var subQ2=makeQuery(id+"F0.imprint","INTERSECT",VERTEX,{"derivedFrom":[sQuery(id+"F0.wireOp",EDGE,"E8"),subQ1,subQ0]});Q8=makeQuery(id+"F0.imprint","IMPRINT",FACE,{"disambiguationData":[TD([[makeQuery(id+"F0.imprint","IMPRINT",EDGE,{"disambiguationData":[TD([[subQ2,1.0]])],"derivedFrom":subQ1}),-1.0]])]});}
            var Q9;
            {var subQ0=sQuery(id+"F0.wireOp",EDGE,"E14");var subQ1=sQuery(id+"F0.wireOp",EDGE,"E5");var subQ2=makeQuery(id+"F0.imprint","INTERSECT",VERTEX,{"derivedFrom":[subQ1,subQ0,sQuery(id+"F0.wireOp",EDGE,"E44")]});Q9=makeQuery(id+"F0.imprint","IMPRINT",FACE,{"disambiguationData":[TD([[makeQuery(id+"F0.imprint","IMPRINT",EDGE,{"disambiguationData":[TD([[subQ2,-1.0]])],"derivedFrom":subQ1}),-1.0]])]});}
            var Q10;
            {var subQ0=sQuery(id+"F0.wireOp",EDGE,"E42");var subQ1=sQuery(id+"F0.wireOp",EDGE,"E21");var subQ2=makeQuery(id+"F0.imprint","INTERSECT",VERTEX,{"derivedFrom":[sQuery(id+"F0.wireOp",EDGE,"E12"),subQ1,subQ0]});Q10=makeQuery(id+"F0.imprint","IMPRINT",FACE,{"disambiguationData":[TD([[makeQuery(id+"F0.imprint","IMPRINT",EDGE,{"disambiguationData":[TD([[subQ2,-1.0]])],"derivedFrom":subQ1}),-1.0]])]});}
            var Q11;
            {var subQ0=sQuery(id+"F0.wireOp",EDGE,"E42");var subQ1=sQuery(id+"F0.wireOp",EDGE,"E6");var subQ2=makeQuery(id+"F0.imprint","INTERSECT",VERTEX,{"derivedFrom":[subQ1,sQuery(id+"F0.wireOp",EDGE,"E19"),subQ0]});Q11=makeQuery(id+"F0.imprint","IMPRINT",FACE,{"disambiguationData":[TD([[makeQuery(id+"F0.imprint","IMPRINT",EDGE,{"disambiguationData":[TD([[subQ2,-1.0]])],"derivedFrom":subQ1}),-1.0]])]});}
            var Q12;
            {var subQ0=sQuery(id+"F0.wireOp",EDGE,"E42");var subQ1=sQuery(id+"F0.wireOp",EDGE,"E19");var subQ2=makeQuery(id+"F0.imprint","INTERSECT",VERTEX,{"derivedFrom":[sQuery(id+"F0.wireOp",EDGE,"E6"),subQ1,subQ0]});Q12=makeQuery(id+"F0.imprint","IMPRINT",FACE,{"disambiguationData":[TD([[makeQuery(id+"F0.imprint","IMPRINT",EDGE,{"disambiguationData":[TD([[subQ2,1.0]])],"derivedFrom":subQ1}),-1.0]])]});}
            var Q13;
            {var subQ0=sQuery(id+"F0.wireOp",EDGE,"E42");var subQ1=sQuery(id+"F0.wireOp",EDGE,"E22");var subQ2=makeQuery(id+"F0.imprint","INTERSECT",VERTEX,{"derivedFrom":[sQuery(id+"F0.wireOp",EDGE,"E13"),subQ1,subQ0]});Q13=makeQuery(id+"F0.imprint","IMPRINT",FACE,{"disambiguationData":[TD([[makeQuery(id+"F0.imprint","IMPRINT",EDGE,{"disambiguationData":[TD([[subQ2,-1.0]])],"derivedFrom":subQ1}),-1.0]])]});}
            var Q14;
            {var subQ0=sQuery(id+"F0.wireOp",EDGE,"E42");var subQ1=sQuery(id+"F0.wireOp",EDGE,"E4");var subQ2=makeQuery(id+"F0.imprint","INTERSECT",VERTEX,{"derivedFrom":[subQ1,sQuery(id+"F0.wireOp",EDGE,"E20"),subQ0]});Q14=makeQuery(id+"F0.imprint","IMPRINT",FACE,{"disambiguationData":[TD([[makeQuery(id+"F0.imprint","IMPRINT",EDGE,{"disambiguationData":[TD([[subQ2,-1.0]])],"derivedFrom":subQ1}),-1.0]])]});}
            var Q15;
            {var subQ0=sQuery(id+"F0.wireOp",EDGE,"E15");var subQ1=sQuery(id+"F0.wireOp",EDGE,"E7");var subQ2=makeQuery(id+"F0.imprint","INTERSECT",VERTEX,{"derivedFrom":[subQ1,subQ0,sQuery(id+"F0.wireOp",EDGE,"E44")]});Q15=makeQuery(id+"F0.imprint","IMPRINT",FACE,{"disambiguationData":[TD([[makeQuery(id+"F0.imprint","IMPRINT",EDGE,{"disambiguationData":[TD([[subQ2,-1.0]])],"derivedFrom":subQ1}),-1.0]])]});}
            var Q16;
            {var subQ0=sQuery(id+"F0.wireOp",EDGE,"E42");var subQ1=sQuery(id+"F0.wireOp",EDGE,"E20");var subQ2=makeQuery(id+"F0.imprint","INTERSECT",VERTEX,{"derivedFrom":[sQuery(id+"F0.wireOp",EDGE,"E4"),subQ1,subQ0]});Q16=makeQuery(id+"F0.imprint","IMPRINT",FACE,{"disambiguationData":[TD([[makeQuery(id+"F0.imprint","IMPRINT",EDGE,{"disambiguationData":[TD([[subQ2,1.0]])],"derivedFrom":subQ1}),-1.0]])]});}
            var Q17;
            {var subQ0=sQuery(id+"F0.wireOp",EDGE,"E10");var subQ1=sQuery(id+"F0.wireOp",EDGE,"E8");var subQ2=makeQuery(id+"F0.imprint","INTERSECT",VERTEX,{"derivedFrom":[subQ1,subQ0,sQuery(id+"F0.wireOp",EDGE,"E44")]});Q17=makeQuery(id+"F0.imprint","IMPRINT",FACE,{"disambiguationData":[TD([[makeQuery(id+"F0.imprint","IMPRINT",EDGE,{"disambiguationData":[TD([[subQ2,-1.0]])],"derivedFrom":subQ1}),-1.0]])]});}
            var Q18;
            {var subQ0=sQuery(id+"F0.wireOp",EDGE,"E42");var subQ1=sQuery(id+"F0.wireOp",EDGE,"E3");var subQ2=makeQuery(id+"F0.imprint","INTERSECT",VERTEX,{"derivedFrom":[subQ1,sQuery(id+"F0.wireOp",EDGE,"E21"),subQ0]});Q18=makeQuery(id+"F0.imprint","IMPRINT",FACE,{"disambiguationData":[TD([[makeQuery(id+"F0.imprint","IMPRINT",EDGE,{"disambiguationData":[TD([[subQ2,-1.0]])],"derivedFrom":subQ1}),-1.0]])]});}
            var Q19;
            {var subQ0=sQuery(id+"F0.wireOp",EDGE,"E42");var subQ1=sQuery(id+"F0.wireOp",EDGE,"E21");var subQ2=makeQuery(id+"F0.imprint","INTERSECT",VERTEX,{"derivedFrom":[sQuery(id+"F0.wireOp",EDGE,"E3"),subQ1,subQ0]});Q19=makeQuery(id+"F0.imprint","IMPRINT",FACE,{"disambiguationData":[TD([[makeQuery(id+"F0.imprint","IMPRINT",EDGE,{"disambiguationData":[TD([[subQ2,1.0]])],"derivedFrom":subQ1}),-1.0]])]});}
            var Q20;
            {var subQ0=sQuery(id+"F0.wireOp",EDGE,"E11");var subQ1=sQuery(id+"F0.wireOp",EDGE,"E6");var subQ2=makeQuery(id+"F0.imprint","INTERSECT",VERTEX,{"derivedFrom":[subQ1,subQ0,sQuery(id+"F0.wireOp",EDGE,"E44")]});Q20=makeQuery(id+"F0.imprint","IMPRINT",FACE,{"disambiguationData":[TD([[makeQuery(id+"F0.imprint","IMPRINT",EDGE,{"disambiguationData":[TD([[subQ2,-1.0]])],"derivedFrom":subQ1}),-1.0]])]});}
            var Q21;
            {var subQ0=sQuery(id+"F0.wireOp",EDGE,"E42");var subQ1=sQuery(id+"F0.wireOp",EDGE,"E18");var subQ2=makeQuery(id+"F0.imprint","INTERSECT",VERTEX,{"derivedFrom":[sQuery(id+"F0.wireOp",EDGE,"E15"),subQ1,subQ0]});Q21=makeQuery(id+"F0.imprint","IMPRINT",FACE,{"disambiguationData":[TD([[makeQuery(id+"F0.imprint","IMPRINT",EDGE,{"disambiguationData":[TD([[subQ2,-1.0]])],"derivedFrom":subQ1}),-1.0]])]});}
            var Q22;
            {var subQ0=sQuery(id+"F0.wireOp",EDGE,"E42");var subQ1=sQuery(id+"F0.wireOp",EDGE,"E5");var subQ2=makeQuery(id+"F0.imprint","INTERSECT",VERTEX,{"derivedFrom":[subQ1,sQuery(id+"F0.wireOp",EDGE,"E22"),subQ0]});Q22=makeQuery(id+"F0.imprint","IMPRINT",FACE,{"disambiguationData":[TD([[makeQuery(id+"F0.imprint","IMPRINT",EDGE,{"disambiguationData":[TD([[subQ2,-1.0]])],"derivedFrom":subQ1}),-1.0]])]});}
            var Q23;
            {var subQ0=sQuery(id+"F0.wireOp",EDGE,"E42");var subQ1=sQuery(id+"F0.wireOp",EDGE,"E22");var subQ2=makeQuery(id+"F0.imprint","INTERSECT",VERTEX,{"derivedFrom":[sQuery(id+"F0.wireOp",EDGE,"E5"),subQ1,subQ0]});Q23=makeQuery(id+"F0.imprint","IMPRINT",FACE,{"disambiguationData":[TD([[makeQuery(id+"F0.imprint","IMPRINT",EDGE,{"disambiguationData":[TD([[subQ2,1.0]])],"derivedFrom":subQ1}),-1.0]])]});}
            var Q24;
            {var subQ0=sQuery(id+"F0.wireOp",EDGE,"E12");var subQ1=sQuery(id+"F0.wireOp",EDGE,"E4");var subQ2=makeQuery(id+"F0.imprint","INTERSECT",VERTEX,{"derivedFrom":[subQ1,subQ0,sQuery(id+"F0.wireOp",EDGE,"E44")]});Q24=makeQuery(id+"F0.imprint","IMPRINT",FACE,{"disambiguationData":[TD([[makeQuery(id+"F0.imprint","IMPRINT",EDGE,{"disambiguationData":[TD([[subQ2,-1.0]])],"derivedFrom":subQ1}),-1.0]])]});}
            var Q25;
            {var subQ0=sQuery(id+"F0.wireOp",EDGE,"E42");var subQ1=sQuery(id+"F0.wireOp",EDGE,"E19");var subQ2=makeQuery(id+"F0.imprint","INTERSECT",VERTEX,{"derivedFrom":[sQuery(id+"F0.wireOp",EDGE,"E10"),subQ1,subQ0]});Q25=makeQuery(id+"F0.imprint","IMPRINT",FACE,{"disambiguationData":[TD([[makeQuery(id+"F0.imprint","IMPRINT",EDGE,{"disambiguationData":[TD([[subQ2,-1.0]])],"derivedFrom":subQ1}),-1.0]])]});}
            var Q26;
            {var subQ0=sQuery(id+"F0.wireOp",EDGE,"E13");var subQ1=sQuery(id+"F0.wireOp",EDGE,"E0");var subQ2=makeQuery(id+"F0.imprint","INTERSECT",VERTEX,{"derivedFrom":[subQ1,sQuery(id+"F0.wireOp",EDGE,"E11"),subQ0]});Q26=makeQuery(id+"F0.imprint","IMPRINT",FACE,{"disambiguationData":[TD([[makeQuery(id+"F0.imprint","IMPRINT",EDGE,{"disambiguationData":[TD([[subQ2,-1.0]])],"derivedFrom":subQ1}),1.0]])]});}
            var Q27;
            {var subQ0=sQuery(id+"F0.wireOp",EDGE,"E20");var subQ1=sQuery(id+"F0.wireOp",EDGE,"E0");var subQ2=makeQuery(id+"F0.imprint","INTERSECT",VERTEX,{"derivedFrom":[subQ1,sQuery(id+"F0.wireOp",EDGE,"E18"),subQ0]});Q27=makeQuery(id+"F0.imprint","IMPRINT",FACE,{"disambiguationData":[TD([[makeQuery(id+"F0.imprint","IMPRINT",EDGE,{"disambiguationData":[TD([[subQ2,-1.0]])],"derivedFrom":subQ1}),1.0]])]});}
            var Q28;
            {var subQ0=sQuery(id+"F0.wireOp",EDGE,"E8");var subQ1=sQuery(id+"F0.wireOp",EDGE,"E0");var subQ2=makeQuery(id+"F0.imprint","INTERSECT",VERTEX,{"derivedFrom":[subQ1,sQuery(id+"F0.wireOp",EDGE,"E5"),subQ0]});Q28=makeQuery(id+"F0.imprint","IMPRINT",FACE,{"disambiguationData":[TD([[makeQuery(id+"F0.imprint","IMPRINT",EDGE,{"disambiguationData":[TD([[subQ2,-1.0]])],"derivedFrom":subQ1}),1.0]])]});}
            var Q29;
            {var subQ0=sQuery(id+"F0.wireOp",EDGE,"E29");var subQ1=sQuery(id+"F0.wireOp",EDGE,"E0");var subQ2=makeQuery(id+"F0.imprint","INTERSECT",VERTEX,{"derivedFrom":[subQ1,sQuery(id+"F0.wireOp",EDGE,"E27"),subQ0]});Q29=makeQuery(id+"F0.imprint","IMPRINT",FACE,{"disambiguationData":[TD([[makeQuery(id+"F0.imprint","IMPRINT",EDGE,{"disambiguationData":[TD([[subQ2,-1.0]])],"derivedFrom":subQ1}),1.0]])]});}
            var Q30;
            {var subQ0=sQuery(id+"F0.wireOp",EDGE,"E14");var subQ1=sQuery(id+"F0.wireOp",EDGE,"E0");var subQ2=makeQuery(id+"F0.imprint","INTERSECT",VERTEX,{"derivedFrom":[subQ1,sQuery(id+"F0.wireOp",EDGE,"E12"),subQ0]});Q30=makeQuery(id+"F0.imprint","IMPRINT",FACE,{"disambiguationData":[TD([[makeQuery(id+"F0.imprint","IMPRINT",EDGE,{"disambiguationData":[TD([[subQ2,-1.0]])],"derivedFrom":subQ1}),1.0]])]});}
            var Q31;
            {var subQ0=sQuery(id+"F0.wireOp",EDGE,"E21");var subQ1=sQuery(id+"F0.wireOp",EDGE,"E0");var subQ2=makeQuery(id+"F0.imprint","INTERSECT",VERTEX,{"derivedFrom":[subQ1,sQuery(id+"F0.wireOp",EDGE,"E19"),subQ0]});Q31=makeQuery(id+"F0.imprint","IMPRINT",FACE,{"disambiguationData":[TD([[makeQuery(id+"F0.imprint","IMPRINT",EDGE,{"disambiguationData":[TD([[subQ2,-1.0]])],"derivedFrom":subQ1}),1.0]])]});}
            var Q32;
            {var subQ0=sQuery(id+"F0.wireOp",EDGE,"E6");var subQ1=sQuery(id+"F0.wireOp",EDGE,"E0");var subQ2=makeQuery(id+"F0.imprint","INTERSECT",VERTEX,{"derivedFrom":[subQ1,subQ0,sQuery(id+"F0.wireOp",EDGE,"E7")]});Q32=makeQuery(id+"F0.imprint","IMPRINT",FACE,{"disambiguationData":[TD([[makeQuery(id+"F0.imprint","IMPRINT",EDGE,{"disambiguationData":[TD([[subQ2,-1.0]])],"derivedFrom":subQ1}),1.0]])]});}
            var Q33;
            {var subQ0=sQuery(id+"F0.wireOp",EDGE,"E24");var subQ1=sQuery(id+"F0.wireOp",EDGE,"E0");var subQ2=makeQuery(id+"F0.imprint","INTERSECT",VERTEX,{"derivedFrom":[subQ1,subQ0,sQuery(id+"F0.wireOp",EDGE,"E28")]});Q33=makeQuery(id+"F0.imprint","IMPRINT",FACE,{"disambiguationData":[TD([[makeQuery(id+"F0.imprint","IMPRINT",EDGE,{"disambiguationData":[TD([[subQ2,-1.0]])],"derivedFrom":subQ1}),1.0]])]});}
            var Q34;
            {var subQ0=sQuery(id+"F0.wireOp",EDGE,"E15");var subQ1=sQuery(id+"F0.wireOp",EDGE,"E0");var subQ2=makeQuery(id+"F0.imprint","INTERSECT",VERTEX,{"derivedFrom":[subQ1,sQuery(id+"F0.wireOp",EDGE,"E13"),subQ0]});Q34=makeQuery(id+"F0.imprint","IMPRINT",FACE,{"disambiguationData":[TD([[makeQuery(id+"F0.imprint","IMPRINT",EDGE,{"disambiguationData":[TD([[subQ2,-1.0]])],"derivedFrom":subQ1}),1.0]])]});}
            var Q35;
            {var subQ0=sQuery(id+"F0.wireOp",EDGE,"E22");var subQ1=sQuery(id+"F0.wireOp",EDGE,"E0");var subQ2=makeQuery(id+"F0.imprint","INTERSECT",VERTEX,{"derivedFrom":[subQ1,sQuery(id+"F0.wireOp",EDGE,"E20"),subQ0]});Q35=makeQuery(id+"F0.imprint","IMPRINT",FACE,{"disambiguationData":[TD([[makeQuery(id+"F0.imprint","IMPRINT",EDGE,{"disambiguationData":[TD([[subQ2,-1.0]])],"derivedFrom":subQ1}),1.0]])]});}
            var Q36;
            {var subQ0=sQuery(id+"F0.wireOp",EDGE,"E4");var subQ1=sQuery(id+"F0.wireOp",EDGE,"E0");var subQ2=makeQuery(id+"F0.imprint","INTERSECT",VERTEX,{"derivedFrom":[subQ1,subQ0,sQuery(id+"F0.wireOp",EDGE,"E8")]});Q36=makeQuery(id+"F0.imprint","IMPRINT",FACE,{"disambiguationData":[TD([[makeQuery(id+"F0.imprint","IMPRINT",EDGE,{"disambiguationData":[TD([[subQ2,-1.0]])],"derivedFrom":subQ1}),1.0]])]});}
            var Q37;
            {var subQ0=sQuery(id+"F0.wireOp",EDGE,"E25");var subQ1=sQuery(id+"F0.wireOp",EDGE,"E0");var subQ2=makeQuery(id+"F0.imprint","INTERSECT",VERTEX,{"derivedFrom":[subQ1,subQ0,sQuery(id+"F0.wireOp",EDGE,"E29")]});Q37=makeQuery(id+"F0.imprint","IMPRINT",FACE,{"disambiguationData":[TD([[makeQuery(id+"F0.imprint","IMPRINT",EDGE,{"disambiguationData":[TD([[subQ2,-1.0]])],"derivedFrom":subQ1}),1.0]])]});}
            var Q38;
            {var subQ0=sQuery(id+"F0.wireOp",EDGE,"E26");var subQ1=sQuery(id+"F0.wireOp",EDGE,"E0");var subQ2=makeQuery(id+"F0.imprint","INTERSECT",VERTEX,{"derivedFrom":[subQ1,sQuery(id+"F0.wireOp",EDGE,"E24"),subQ0]});Q38=makeQuery(id+"F0.imprint","IMPRINT",FACE,{"disambiguationData":[TD([[makeQuery(id+"F0.imprint","IMPRINT",EDGE,{"disambiguationData":[TD([[subQ2,-1.0]])],"derivedFrom":subQ1}),1.0]])]});}
            var Q39;
            {var subQ0=sQuery(id+"F0.wireOp",EDGE,"E18");var subQ1=sQuery(id+"F0.wireOp",EDGE,"E0");var subQ2=makeQuery(id+"F0.imprint","INTERSECT",VERTEX,{"derivedFrom":[subQ1,subQ0,sQuery(id+"F0.wireOp",EDGE,"E22")]});Q39=makeQuery(id+"F0.imprint","IMPRINT",FACE,{"disambiguationData":[TD([[makeQuery(id+"F0.imprint","IMPRINT",EDGE,{"disambiguationData":[TD([[subQ2,-1.0]])],"derivedFrom":subQ1}),1.0]])]});}
            var Q40;
            {var subQ0=sQuery(id+"F0.wireOp",EDGE,"E11");var subQ1=sQuery(id+"F0.wireOp",EDGE,"E0");var subQ2=makeQuery(id+"F0.imprint","INTERSECT",VERTEX,{"derivedFrom":[subQ1,subQ0,sQuery(id+"F0.wireOp",EDGE,"E15")]});Q40=makeQuery(id+"F0.imprint","IMPRINT",FACE,{"disambiguationData":[TD([[makeQuery(id+"F0.imprint","IMPRINT",EDGE,{"disambiguationData":[TD([[subQ2,-1.0]])],"derivedFrom":subQ1}),1.0]])]});}
            var Q41;
            {var subQ0=sQuery(id+"F0.wireOp",EDGE,"E4");var subQ1=sQuery(id+"F0.wireOp",EDGE,"E0");var subQ2=makeQuery(id+"F0.imprint","INTERSECT",VERTEX,{"derivedFrom":[subQ1,subQ0,sQuery(id+"F0.wireOp",EDGE,"E5")]});Q41=makeQuery(id+"F0.imprint","IMPRINT",FACE,{"disambiguationData":[TD([[makeQuery(id+"F0.imprint","IMPRINT",EDGE,{"disambiguationData":[TD([[subQ2,1.0]])],"derivedFrom":subQ1}),1.0]])]});}
            var Q42;
            {var subQ0=sQuery(id+"F0.wireOp",EDGE,"E22");var subQ1=sQuery(id+"F0.wireOp",EDGE,"E0");var subQ2=makeQuery(id+"F0.imprint","INTERSECT",VERTEX,{"derivedFrom":[subQ1,sQuery(id+"F0.wireOp",EDGE,"E18"),subQ0]});Q42=makeQuery(id+"F0.imprint","IMPRINT",FACE,{"disambiguationData":[TD([[makeQuery(id+"F0.imprint","IMPRINT",EDGE,{"disambiguationData":[TD([[subQ2,1.0]])],"derivedFrom":subQ1}),1.0]])]});}
            var Q43;
            {var subQ0=sQuery(id+"F0.wireOp",EDGE,"E12");var subQ1=sQuery(id+"F0.wireOp",EDGE,"E0");var subQ2=makeQuery(id+"F0.imprint","INTERSECT",VERTEX,{"derivedFrom":[subQ1,sQuery(id+"F0.wireOp",EDGE,"E10"),subQ0]});Q43=makeQuery(id+"F0.imprint","IMPRINT",FACE,{"disambiguationData":[TD([[makeQuery(id+"F0.imprint","IMPRINT",EDGE,{"disambiguationData":[TD([[subQ2,-1.0]])],"derivedFrom":subQ1}),1.0]])]});}
            var Q44;
            {var subQ0=sQuery(id+"F0.wireOp",EDGE,"E3");var subQ1=sQuery(id+"F0.wireOp",EDGE,"E0");var subQ2=makeQuery(id+"F0.imprint","INTERSECT",VERTEX,{"derivedFrom":[subQ1,subQ0,sQuery(id+"F0.wireOp",EDGE,"E6")]});Q44=makeQuery(id+"F0.imprint","IMPRINT",FACE,{"disambiguationData":[TD([[makeQuery(id+"F0.imprint","IMPRINT",EDGE,{"disambiguationData":[TD([[subQ2,-1.0]])],"derivedFrom":subQ1}),1.0]])]});}
            var Q45;
            {var subQ0=sQuery(id+"F0.wireOp",EDGE,"E10");var subQ1=sQuery(id+"F0.wireOp",EDGE,"E0");var subQ2=makeQuery(id+"F0.imprint","INTERSECT",VERTEX,{"derivedFrom":[subQ1,subQ0,sQuery(id+"F0.wireOp",EDGE,"E14")]});Q45=makeQuery(id+"F0.imprint","IMPRINT",FACE,{"disambiguationData":[TD([[makeQuery(id+"F0.imprint","IMPRINT",EDGE,{"disambiguationData":[TD([[subQ2,-1.0]])],"derivedFrom":subQ1}),1.0]])]});}
            var Q46;
            {var subQ0=sQuery(id+"F0.wireOp",EDGE,"E17");var subQ1=sQuery(id+"F0.wireOp",EDGE,"E0");var subQ2=makeQuery(id+"F0.imprint","INTERSECT",VERTEX,{"derivedFrom":[subQ1,subQ0,sQuery(id+"F0.wireOp",EDGE,"E21")]});Q46=makeQuery(id+"F0.imprint","IMPRINT",FACE,{"disambiguationData":[TD([[makeQuery(id+"F0.imprint","IMPRINT",EDGE,{"disambiguationData":[TD([[subQ2,-1.0]])],"derivedFrom":subQ1}),1.0]])]});}
            var Q47;
            {var subQ0=sQuery(id+"F0.wireOp",EDGE,"E42");var subQ1=sQuery(id+"F0.wireOp",EDGE,"E17");var subQ2=makeQuery(id+"F0.imprint","INTERSECT",VERTEX,{"derivedFrom":[sQuery(id+"F0.wireOp",EDGE,"E14"),subQ1,subQ0]});Q47=makeQuery(id+"F0.imprint","IMPRINT",FACE,{"disambiguationData":[TD([[makeQuery(id+"F0.imprint","IMPRINT",EDGE,{"disambiguationData":[TD([[subQ2,-1.0]])],"derivedFrom":subQ1}),-1.0]])]});}
            extrude(context, id + "F4", {"entities" : qUnion([Q0, Q1, Q2, Q3, Q4, Q5, Q6, Q7, Q8, Q9, Q10, Q11, Q12, Q13, Q14, Q15, Q16, Q17, Q18, Q19, Q20, Q21, Q22, Q23, Q24, Q25, Q26, Q27, Q28, Q29, Q30, Q31, Q32, Q33, Q34, Q35, Q36, Q37, Q38, Q39, Q40, Q41, Q42, Q43, Q44, Q45, Q46, Q47]), "depth" : 12 * mm, "hasDraft" : true, "draftAngle" : 5 * degree, "draftPullDirection" : true});
        }
        {
            var Q0;
            {var subQ0=sQuery(id+"F0.wireOp",EDGE,"E20");var subQ1=sQuery(id+"F0.wireOp",EDGE,"E18");var subQ2=makeQuery(id+"F0.imprint","INTERSECT",VERTEX,{"derivedFrom":[sQuery(id+"F0.wireOp",EDGE,"E0"),subQ1,subQ0]});Q0=makeQuery(id+"F0.imprint","IMPRINT",FACE,{"disambiguationData":[TD([[makeQuery(id+"F0.imprint","IMPRINT",EDGE,{"disambiguationData":[TD([[subQ2,-1.0]])],"derivedFrom":subQ1}),-1.0]])]});}
            var Q1;
            {var subQ0=sQuery(id+"F0.wireOp",EDGE,"E13");var subQ1=sQuery(id+"F0.wireOp",EDGE,"E11");var subQ2=makeQuery(id+"F0.imprint","INTERSECT",VERTEX,{"derivedFrom":[sQuery(id+"F0.wireOp",EDGE,"E0"),subQ1,subQ0]});Q1=makeQuery(id+"F0.imprint","IMPRINT",FACE,{"disambiguationData":[TD([[makeQuery(id+"F0.imprint","IMPRINT",EDGE,{"disambiguationData":[TD([[subQ2,-1.0]])],"derivedFrom":subQ1}),-1.0]])]});}
            var Q2;
            {var subQ0=sQuery(id+"F0.wireOp",EDGE,"E28");var subQ1=sQuery(id+"F0.wireOp",EDGE,"E26");var subQ2=makeQuery(id+"F0.imprint","INTERSECT",VERTEX,{"derivedFrom":[sQuery(id+"F0.wireOp",EDGE,"E0"),subQ1,subQ0]});Q2=makeQuery(id+"F0.imprint","IMPRINT",FACE,{"disambiguationData":[TD([[makeQuery(id+"F0.imprint","IMPRINT",EDGE,{"disambiguationData":[TD([[subQ2,-1.0]])],"derivedFrom":subQ1}),-1.0]])]});}
            var Q3;
            {var subQ0=sQuery(id+"F0.wireOp",EDGE,"E7");var subQ1=sQuery(id+"F0.wireOp",EDGE,"E3");var subQ2=makeQuery(id+"F0.imprint","INTERSECT",VERTEX,{"derivedFrom":[sQuery(id+"F0.wireOp",EDGE,"E0"),subQ1,subQ0]});Q3=makeQuery(id+"F0.imprint","IMPRINT",FACE,{"disambiguationData":[TD([[makeQuery(id+"F0.imprint","IMPRINT",EDGE,{"disambiguationData":[TD([[subQ2,-1.0]])],"derivedFrom":subQ1}),-1.0]])]});}
            var Q4;
            {var subQ0=sQuery(id+"F0.wireOp",EDGE,"E19");var subQ1=sQuery(id+"F0.wireOp",EDGE,"E17");var subQ2=makeQuery(id+"F0.imprint","INTERSECT",VERTEX,{"derivedFrom":[sQuery(id+"F0.wireOp",EDGE,"E0"),subQ1,subQ0]});Q4=makeQuery(id+"F0.imprint","IMPRINT",FACE,{"disambiguationData":[TD([[makeQuery(id+"F0.imprint","IMPRINT",EDGE,{"disambiguationData":[TD([[subQ2,-1.0]])],"derivedFrom":subQ1}),-1.0]])]});}
            var Q5;
            {var subQ0=sQuery(id+"F0.wireOp",EDGE,"E12");var subQ1=sQuery(id+"F0.wireOp",EDGE,"E10");var subQ2=makeQuery(id+"F0.imprint","INTERSECT",VERTEX,{"derivedFrom":[sQuery(id+"F0.wireOp",EDGE,"E0"),subQ1,subQ0]});Q5=makeQuery(id+"F0.imprint","IMPRINT",FACE,{"disambiguationData":[TD([[makeQuery(id+"F0.imprint","IMPRINT",EDGE,{"disambiguationData":[TD([[subQ2,-1.0]])],"derivedFrom":subQ1}),-1.0]])]});}
            var Q6;
            {var subQ0=sQuery(id+"F0.wireOp",EDGE,"E27");var subQ1=sQuery(id+"F0.wireOp",EDGE,"E25");var subQ2=makeQuery(id+"F0.imprint","INTERSECT",VERTEX,{"derivedFrom":[sQuery(id+"F0.wireOp",EDGE,"E0"),subQ1,subQ0]});Q6=makeQuery(id+"F0.imprint","IMPRINT",FACE,{"disambiguationData":[TD([[makeQuery(id+"F0.imprint","IMPRINT",EDGE,{"disambiguationData":[TD([[subQ2,-1.0]])],"derivedFrom":subQ1}),-1.0]])]});}
            var Q7;
            {var subQ0=sQuery(id+"F0.wireOp",EDGE,"E5");var subQ1=sQuery(id+"F0.wireOp",EDGE,"E4");var subQ2=makeQuery(id+"F0.imprint","INTERSECT",VERTEX,{"derivedFrom":[sQuery(id+"F0.wireOp",EDGE,"E0"),subQ1,subQ0]});Q7=makeQuery(id+"F0.imprint","IMPRINT",FACE,{"disambiguationData":[TD([[makeQuery(id+"F0.imprint","IMPRINT",EDGE,{"disambiguationData":[TD([[subQ2,-1.0]])],"derivedFrom":subQ1}),-1.0]])]});}
            var Q8;
            {var subQ0=sQuery(id+"F0.wireOp",EDGE,"E22");var subQ1=sQuery(id+"F0.wireOp",EDGE,"E18");var subQ2=makeQuery(id+"F0.imprint","INTERSECT",VERTEX,{"derivedFrom":[sQuery(id+"F0.wireOp",EDGE,"E0"),subQ1,subQ0]});Q8=makeQuery(id+"F0.imprint","IMPRINT",FACE,{"disambiguationData":[TD([[makeQuery(id+"F0.imprint","IMPRINT",EDGE,{"disambiguationData":[TD([[subQ2,1.0]])],"derivedFrom":subQ1}),-1.0]])]});}
            var Q9;
            {var subQ0=sQuery(id+"F0.wireOp",EDGE,"E15");var subQ1=sQuery(id+"F0.wireOp",EDGE,"E11");var subQ2=makeQuery(id+"F0.imprint","INTERSECT",VERTEX,{"derivedFrom":[sQuery(id+"F0.wireOp",EDGE,"E0"),subQ1,subQ0]});Q9=makeQuery(id+"F0.imprint","IMPRINT",FACE,{"disambiguationData":[TD([[makeQuery(id+"F0.imprint","IMPRINT",EDGE,{"disambiguationData":[TD([[subQ2,1.0]])],"derivedFrom":subQ1}),-1.0]])]});}
            var Q10;
            {var subQ0=sQuery(id+"F0.wireOp",EDGE,"E26");var subQ1=sQuery(id+"F0.wireOp",EDGE,"E24");var subQ2=makeQuery(id+"F0.imprint","INTERSECT",VERTEX,{"derivedFrom":[sQuery(id+"F0.wireOp",EDGE,"E0"),subQ1,subQ0]});Q10=makeQuery(id+"F0.imprint","IMPRINT",FACE,{"disambiguationData":[TD([[makeQuery(id+"F0.imprint","IMPRINT",EDGE,{"disambiguationData":[TD([[subQ2,-1.0]])],"derivedFrom":subQ1}),-1.0]])]});}
            var Q11;
            {var subQ0=sQuery(id+"F0.wireOp",EDGE,"E6");var subQ1=sQuery(id+"F0.wireOp",EDGE,"E3");var subQ2=makeQuery(id+"F0.imprint","INTERSECT",VERTEX,{"derivedFrom":[sQuery(id+"F0.wireOp",EDGE,"E0"),subQ1,subQ0]});Q11=makeQuery(id+"F0.imprint","IMPRINT",FACE,{"disambiguationData":[TD([[makeQuery(id+"F0.imprint","IMPRINT",EDGE,{"disambiguationData":[TD([[subQ2,1.0]])],"derivedFrom":subQ1}),-1.0]])]});}
            var Q12;
            {var subQ0=sQuery(id+"F0.wireOp",EDGE,"E21");var subQ1=sQuery(id+"F0.wireOp",EDGE,"E17");var subQ2=makeQuery(id+"F0.imprint","INTERSECT",VERTEX,{"derivedFrom":[sQuery(id+"F0.wireOp",EDGE,"E0"),subQ1,subQ0]});Q12=makeQuery(id+"F0.imprint","IMPRINT",FACE,{"disambiguationData":[TD([[makeQuery(id+"F0.imprint","IMPRINT",EDGE,{"disambiguationData":[TD([[subQ2,1.0]])],"derivedFrom":subQ1}),-1.0]])]});}
            var Q13;
            {var subQ0=sQuery(id+"F0.wireOp",EDGE,"E14");var subQ1=sQuery(id+"F0.wireOp",EDGE,"E10");var subQ2=makeQuery(id+"F0.imprint","INTERSECT",VERTEX,{"derivedFrom":[sQuery(id+"F0.wireOp",EDGE,"E0"),subQ1,subQ0]});Q13=makeQuery(id+"F0.imprint","IMPRINT",FACE,{"disambiguationData":[TD([[makeQuery(id+"F0.imprint","IMPRINT",EDGE,{"disambiguationData":[TD([[subQ2,1.0]])],"derivedFrom":subQ1}),-1.0]])]});}
            var Q14;
            {var subQ0=sQuery(id+"F0.wireOp",EDGE,"E29");var subQ1=sQuery(id+"F0.wireOp",EDGE,"E25");var subQ2=makeQuery(id+"F0.imprint","INTERSECT",VERTEX,{"derivedFrom":[sQuery(id+"F0.wireOp",EDGE,"E0"),subQ1,subQ0]});Q14=makeQuery(id+"F0.imprint","IMPRINT",FACE,{"disambiguationData":[TD([[makeQuery(id+"F0.imprint","IMPRINT",EDGE,{"disambiguationData":[TD([[subQ2,1.0]])],"derivedFrom":subQ1}),-1.0]])]});}
            var Q15;
            {var subQ0=sQuery(id+"F0.wireOp",EDGE,"E8");var subQ1=sQuery(id+"F0.wireOp",EDGE,"E4");var subQ2=makeQuery(id+"F0.imprint","INTERSECT",VERTEX,{"derivedFrom":[sQuery(id+"F0.wireOp",EDGE,"E0"),subQ1,subQ0]});Q15=makeQuery(id+"F0.imprint","IMPRINT",FACE,{"disambiguationData":[TD([[makeQuery(id+"F0.imprint","IMPRINT",EDGE,{"disambiguationData":[TD([[subQ2,1.0]])],"derivedFrom":subQ1}),-1.0]])]});}
            var Q16;
            {var subQ0=sQuery(id+"F0.wireOp",EDGE,"E22");var subQ1=sQuery(id+"F0.wireOp",EDGE,"E20");var subQ2=makeQuery(id+"F0.imprint","INTERSECT",VERTEX,{"derivedFrom":[sQuery(id+"F0.wireOp",EDGE,"E0"),subQ1,subQ0]});Q16=makeQuery(id+"F0.imprint","IMPRINT",FACE,{"disambiguationData":[TD([[makeQuery(id+"F0.imprint","IMPRINT",EDGE,{"disambiguationData":[TD([[subQ2,-1.0]])],"derivedFrom":subQ1}),-1.0]])]});}
            var Q17;
            {var subQ0=sQuery(id+"F0.wireOp",EDGE,"E15");var subQ1=sQuery(id+"F0.wireOp",EDGE,"E13");var subQ2=makeQuery(id+"F0.imprint","INTERSECT",VERTEX,{"derivedFrom":[sQuery(id+"F0.wireOp",EDGE,"E0"),subQ1,subQ0]});Q17=makeQuery(id+"F0.imprint","IMPRINT",FACE,{"disambiguationData":[TD([[makeQuery(id+"F0.imprint","IMPRINT",EDGE,{"disambiguationData":[TD([[subQ2,-1.0]])],"derivedFrom":subQ1}),-1.0]])]});}
            var Q18;
            {var subQ0=sQuery(id+"F0.wireOp",EDGE,"E28");var subQ1=sQuery(id+"F0.wireOp",EDGE,"E24");var subQ2=makeQuery(id+"F0.imprint","INTERSECT",VERTEX,{"derivedFrom":[sQuery(id+"F0.wireOp",EDGE,"E0"),subQ1,subQ0]});Q18=makeQuery(id+"F0.imprint","IMPRINT",FACE,{"disambiguationData":[TD([[makeQuery(id+"F0.imprint","IMPRINT",EDGE,{"disambiguationData":[TD([[subQ2,1.0]])],"derivedFrom":subQ1}),-1.0]])]});}
            var Q19;
            {var subQ0=sQuery(id+"F0.wireOp",EDGE,"E7");var subQ1=sQuery(id+"F0.wireOp",EDGE,"E6");var subQ2=makeQuery(id+"F0.imprint","INTERSECT",VERTEX,{"derivedFrom":[sQuery(id+"F0.wireOp",EDGE,"E0"),subQ1,subQ0]});Q19=makeQuery(id+"F0.imprint","IMPRINT",FACE,{"disambiguationData":[TD([[makeQuery(id+"F0.imprint","IMPRINT",EDGE,{"disambiguationData":[TD([[subQ2,1.0]])],"derivedFrom":subQ1}),-1.0]])]});}
            var Q20;
            {var subQ0=sQuery(id+"F0.wireOp",EDGE,"E21");var subQ1=sQuery(id+"F0.wireOp",EDGE,"E19");var subQ2=makeQuery(id+"F0.imprint","INTERSECT",VERTEX,{"derivedFrom":[sQuery(id+"F0.wireOp",EDGE,"E0"),subQ1,subQ0]});Q20=makeQuery(id+"F0.imprint","IMPRINT",FACE,{"disambiguationData":[TD([[makeQuery(id+"F0.imprint","IMPRINT",EDGE,{"disambiguationData":[TD([[subQ2,-1.0]])],"derivedFrom":subQ1}),-1.0]])]});}
            var Q21;
            {var subQ0=sQuery(id+"F0.wireOp",EDGE,"E14");var subQ1=sQuery(id+"F0.wireOp",EDGE,"E12");var subQ2=makeQuery(id+"F0.imprint","INTERSECT",VERTEX,{"derivedFrom":[sQuery(id+"F0.wireOp",EDGE,"E0"),subQ1,subQ0]});Q21=makeQuery(id+"F0.imprint","IMPRINT",FACE,{"disambiguationData":[TD([[makeQuery(id+"F0.imprint","IMPRINT",EDGE,{"disambiguationData":[TD([[subQ2,-1.0]])],"derivedFrom":subQ1}),-1.0]])]});}
            var Q22;
            {var subQ0=sQuery(id+"F0.wireOp",EDGE,"E29");var subQ1=sQuery(id+"F0.wireOp",EDGE,"E27");var subQ2=makeQuery(id+"F0.imprint","INTERSECT",VERTEX,{"derivedFrom":[sQuery(id+"F0.wireOp",EDGE,"E0"),subQ1,subQ0]});Q22=makeQuery(id+"F0.imprint","IMPRINT",FACE,{"disambiguationData":[TD([[makeQuery(id+"F0.imprint","IMPRINT",EDGE,{"disambiguationData":[TD([[subQ2,-1.0]])],"derivedFrom":subQ1}),-1.0]])]});}
            var Q23;
            {var subQ0=sQuery(id+"F0.wireOp",EDGE,"E8");var subQ1=sQuery(id+"F0.wireOp",EDGE,"E5");var subQ2=makeQuery(id+"F0.imprint","INTERSECT",VERTEX,{"derivedFrom":[sQuery(id+"F0.wireOp",EDGE,"E0"),subQ1,subQ0]});Q23=makeQuery(id+"F0.imprint","IMPRINT",FACE,{"disambiguationData":[TD([[makeQuery(id+"F0.imprint","IMPRINT",EDGE,{"disambiguationData":[TD([[subQ2,-1.0]])],"derivedFrom":subQ1}),-1.0]])]});}
            var Q24;
            {var subQ0=sQuery(id+"F0.wireOp",EDGE,"E22");var subQ1=sQuery(id+"F0.wireOp",EDGE,"E8");var subQ2=makeQuery(id+"F0.imprint","INTERSECT",VERTEX,{"derivedFrom":[subQ1,subQ0,sQuery(id+"F0.wireOp",EDGE,"E30")]});Q24=makeQuery(id+"F0.imprint","IMPRINT",FACE,{"disambiguationData":[TD([[makeQuery(id+"F0.imprint","IMPRINT",EDGE,{"disambiguationData":[TD([[subQ2,-1.0]])],"derivedFrom":subQ1}),-1.0]])]});}
            var Q25;
            {var subQ0=sQuery(id+"F0.wireOp",EDGE,"E32");var subQ1=sQuery(id+"F0.wireOp",EDGE,"E15");var subQ2=makeQuery(id+"F0.imprint","INTERSECT",VERTEX,{"derivedFrom":[sQuery(id+"F0.wireOp",EDGE,"E8"),subQ1,subQ0]});Q25=makeQuery(id+"F0.imprint","IMPRINT",FACE,{"disambiguationData":[TD([[makeQuery(id+"F0.imprint","IMPRINT",EDGE,{"disambiguationData":[TD([[subQ2,-1.0]])],"derivedFrom":subQ1}),-1.0]])]});}
            var Q26;
            {var subQ0=sQuery(id+"F0.wireOp",EDGE,"E32");var subQ1=sQuery(id+"F0.wireOp",EDGE,"E13");var subQ2=makeQuery(id+"F0.imprint","INTERSECT",VERTEX,{"derivedFrom":[sQuery(id+"F0.wireOp",EDGE,"E6"),subQ1,subQ0]});Q26=makeQuery(id+"F0.imprint","IMPRINT",FACE,{"disambiguationData":[TD([[makeQuery(id+"F0.imprint","IMPRINT",EDGE,{"disambiguationData":[TD([[subQ2,1.0]])],"derivedFrom":subQ1}),-1.0]])]});}
            var Q27;
            {var subQ0=sQuery(id+"F0.wireOp",EDGE,"E32");var subQ1=sQuery(id+"F0.wireOp",EDGE,"E6");var subQ2=makeQuery(id+"F0.imprint","INTERSECT",VERTEX,{"derivedFrom":[subQ1,sQuery(id+"F0.wireOp",EDGE,"E13"),subQ0]});Q27=makeQuery(id+"F0.imprint","IMPRINT",FACE,{"disambiguationData":[TD([[makeQuery(id+"F0.imprint","IMPRINT",EDGE,{"disambiguationData":[TD([[subQ2,-1.0]])],"derivedFrom":subQ1}),-1.0]])]});}
            var Q28;
            {var subQ0=sQuery(id+"F0.wireOp",EDGE,"E21");var subQ1=sQuery(id+"F0.wireOp",EDGE,"E7");var subQ2=makeQuery(id+"F0.imprint","INTERSECT",VERTEX,{"derivedFrom":[subQ1,subQ0,sQuery(id+"F0.wireOp",EDGE,"E30")]});Q28=makeQuery(id+"F0.imprint","IMPRINT",FACE,{"disambiguationData":[TD([[makeQuery(id+"F0.imprint","IMPRINT",EDGE,{"disambiguationData":[TD([[subQ2,-1.0]])],"derivedFrom":subQ1}),-1.0]])]});}
            var Q29;
            {var subQ0=sQuery(id+"F0.wireOp",EDGE,"E32");var subQ1=sQuery(id+"F0.wireOp",EDGE,"E14");var subQ2=makeQuery(id+"F0.imprint","INTERSECT",VERTEX,{"derivedFrom":[sQuery(id+"F0.wireOp",EDGE,"E7"),subQ1,subQ0]});Q29=makeQuery(id+"F0.imprint","IMPRINT",FACE,{"disambiguationData":[TD([[makeQuery(id+"F0.imprint","IMPRINT",EDGE,{"disambiguationData":[TD([[subQ2,-1.0]])],"derivedFrom":subQ1}),-1.0]])]});}
            var Q30;
            {var subQ0=sQuery(id+"F0.wireOp",EDGE,"E32");var subQ1=sQuery(id+"F0.wireOp",EDGE,"E12");var subQ2=makeQuery(id+"F0.imprint","INTERSECT",VERTEX,{"derivedFrom":[sQuery(id+"F0.wireOp",EDGE,"E8"),subQ1,subQ0]});Q30=makeQuery(id+"F0.imprint","IMPRINT",FACE,{"disambiguationData":[TD([[makeQuery(id+"F0.imprint","IMPRINT",EDGE,{"disambiguationData":[TD([[subQ2,1.0]])],"derivedFrom":subQ1}),-1.0]])]});}
            var Q31;
            {var subQ0=sQuery(id+"F0.wireOp",EDGE,"E32");var subQ1=sQuery(id+"F0.wireOp",EDGE,"E8");var subQ2=makeQuery(id+"F0.imprint","INTERSECT",VERTEX,{"derivedFrom":[subQ1,sQuery(id+"F0.wireOp",EDGE,"E12"),subQ0]});Q31=makeQuery(id+"F0.imprint","IMPRINT",FACE,{"disambiguationData":[TD([[makeQuery(id+"F0.imprint","IMPRINT",EDGE,{"disambiguationData":[TD([[subQ2,-1.0]])],"derivedFrom":subQ1}),-1.0]])]});}
            var Q32;
            {var subQ0=sQuery(id+"F0.wireOp",EDGE,"E20");var subQ1=sQuery(id+"F0.wireOp",EDGE,"E5");var subQ2=makeQuery(id+"F0.imprint","INTERSECT",VERTEX,{"derivedFrom":[subQ1,subQ0,sQuery(id+"F0.wireOp",EDGE,"E30")]});Q32=makeQuery(id+"F0.imprint","IMPRINT",FACE,{"disambiguationData":[TD([[makeQuery(id+"F0.imprint","IMPRINT",EDGE,{"disambiguationData":[TD([[subQ2,-1.0]])],"derivedFrom":subQ1}),-1.0]])]});}
            var Q33;
            {var subQ0=sQuery(id+"F0.wireOp",EDGE,"E32");var subQ1=sQuery(id+"F0.wireOp",EDGE,"E13");var subQ2=makeQuery(id+"F0.imprint","INTERSECT",VERTEX,{"derivedFrom":[sQuery(id+"F0.wireOp",EDGE,"E5"),subQ1,subQ0]});Q33=makeQuery(id+"F0.imprint","IMPRINT",FACE,{"disambiguationData":[TD([[makeQuery(id+"F0.imprint","IMPRINT",EDGE,{"disambiguationData":[TD([[subQ2,-1.0]])],"derivedFrom":subQ1}),-1.0]])]});}
            var Q34;
            {var subQ0=sQuery(id+"F0.wireOp",EDGE,"E32");var subQ1=sQuery(id+"F0.wireOp",EDGE,"E11");var subQ2=makeQuery(id+"F0.imprint","INTERSECT",VERTEX,{"derivedFrom":[sQuery(id+"F0.wireOp",EDGE,"E7"),subQ1,subQ0]});Q34=makeQuery(id+"F0.imprint","IMPRINT",FACE,{"disambiguationData":[TD([[makeQuery(id+"F0.imprint","IMPRINT",EDGE,{"disambiguationData":[TD([[subQ2,1.0]])],"derivedFrom":subQ1}),-1.0]])]});}
            var Q35;
            {var subQ0=sQuery(id+"F0.wireOp",EDGE,"E32");var subQ1=sQuery(id+"F0.wireOp",EDGE,"E7");var subQ2=makeQuery(id+"F0.imprint","INTERSECT",VERTEX,{"derivedFrom":[subQ1,sQuery(id+"F0.wireOp",EDGE,"E11"),subQ0]});Q35=makeQuery(id+"F0.imprint","IMPRINT",FACE,{"disambiguationData":[TD([[makeQuery(id+"F0.imprint","IMPRINT",EDGE,{"disambiguationData":[TD([[subQ2,-1.0]])],"derivedFrom":subQ1}),-1.0]])]});}
            var Q36;
            {var subQ0=sQuery(id+"F0.wireOp",EDGE,"E19");var subQ1=sQuery(id+"F0.wireOp",EDGE,"E3");var subQ2=makeQuery(id+"F0.imprint","INTERSECT",VERTEX,{"derivedFrom":[subQ1,subQ0,sQuery(id+"F0.wireOp",EDGE,"E30")]});Q36=makeQuery(id+"F0.imprint","IMPRINT",FACE,{"disambiguationData":[TD([[makeQuery(id+"F0.imprint","IMPRINT",EDGE,{"disambiguationData":[TD([[subQ2,-1.0]])],"derivedFrom":subQ1}),-1.0]])]});}
            var Q37;
            {var subQ0=sQuery(id+"F0.wireOp",EDGE,"E32");var subQ1=sQuery(id+"F0.wireOp",EDGE,"E12");var subQ2=makeQuery(id+"F0.imprint","INTERSECT",VERTEX,{"derivedFrom":[sQuery(id+"F0.wireOp",EDGE,"E3"),subQ1,subQ0]});Q37=makeQuery(id+"F0.imprint","IMPRINT",FACE,{"disambiguationData":[TD([[makeQuery(id+"F0.imprint","IMPRINT",EDGE,{"disambiguationData":[TD([[subQ2,-1.0]])],"derivedFrom":subQ1}),-1.0]])]});}
            var Q38;
            {var subQ0=sQuery(id+"F0.wireOp",EDGE,"E32");var subQ1=sQuery(id+"F0.wireOp",EDGE,"E10");var subQ2=makeQuery(id+"F0.imprint","INTERSECT",VERTEX,{"derivedFrom":[sQuery(id+"F0.wireOp",EDGE,"E5"),subQ1,subQ0]});Q38=makeQuery(id+"F0.imprint","IMPRINT",FACE,{"disambiguationData":[TD([[makeQuery(id+"F0.imprint","IMPRINT",EDGE,{"disambiguationData":[TD([[subQ2,1.0]])],"derivedFrom":subQ1}),-1.0]])]});}
            var Q39;
            {var subQ0=sQuery(id+"F0.wireOp",EDGE,"E32");var subQ1=sQuery(id+"F0.wireOp",EDGE,"E5");var subQ2=makeQuery(id+"F0.imprint","INTERSECT",VERTEX,{"derivedFrom":[subQ1,sQuery(id+"F0.wireOp",EDGE,"E10"),subQ0]});Q39=makeQuery(id+"F0.imprint","IMPRINT",FACE,{"disambiguationData":[TD([[makeQuery(id+"F0.imprint","IMPRINT",EDGE,{"disambiguationData":[TD([[subQ2,-1.0]])],"derivedFrom":subQ1}),-1.0]])]});}
            var Q40;
            {var subQ0=sQuery(id+"F0.wireOp",EDGE,"E18");var subQ1=sQuery(id+"F0.wireOp",EDGE,"E4");var subQ2=makeQuery(id+"F0.imprint","INTERSECT",VERTEX,{"derivedFrom":[subQ1,subQ0,sQuery(id+"F0.wireOp",EDGE,"E30")]});Q40=makeQuery(id+"F0.imprint","IMPRINT",FACE,{"disambiguationData":[TD([[makeQuery(id+"F0.imprint","IMPRINT",EDGE,{"disambiguationData":[TD([[subQ2,-1.0]])],"derivedFrom":subQ1}),-1.0]])]});}
            var Q41;
            {var subQ0=sQuery(id+"F0.wireOp",EDGE,"E32");var subQ1=sQuery(id+"F0.wireOp",EDGE,"E11");var subQ2=makeQuery(id+"F0.imprint","INTERSECT",VERTEX,{"derivedFrom":[sQuery(id+"F0.wireOp",EDGE,"E4"),subQ1,subQ0]});Q41=makeQuery(id+"F0.imprint","IMPRINT",FACE,{"disambiguationData":[TD([[makeQuery(id+"F0.imprint","IMPRINT",EDGE,{"disambiguationData":[TD([[subQ2,-1.0]])],"derivedFrom":subQ1}),-1.0]])]});}
            var Q42;
            {var subQ0=sQuery(id+"F0.wireOp",EDGE,"E32");var subQ1=sQuery(id+"F0.wireOp",EDGE,"E15");var subQ2=makeQuery(id+"F0.imprint","INTERSECT",VERTEX,{"derivedFrom":[sQuery(id+"F0.wireOp",EDGE,"E3"),subQ1,subQ0]});Q42=makeQuery(id+"F0.imprint","IMPRINT",FACE,{"disambiguationData":[TD([[makeQuery(id+"F0.imprint","IMPRINT",EDGE,{"disambiguationData":[TD([[subQ2,1.0]])],"derivedFrom":subQ1}),-1.0]])]});}
            var Q43;
            {var subQ0=sQuery(id+"F0.wireOp",EDGE,"E32");var subQ1=sQuery(id+"F0.wireOp",EDGE,"E3");var subQ2=makeQuery(id+"F0.imprint","INTERSECT",VERTEX,{"derivedFrom":[subQ1,sQuery(id+"F0.wireOp",EDGE,"E15"),subQ0]});Q43=makeQuery(id+"F0.imprint","IMPRINT",FACE,{"disambiguationData":[TD([[makeQuery(id+"F0.imprint","IMPRINT",EDGE,{"disambiguationData":[TD([[subQ2,-1.0]])],"derivedFrom":subQ1}),-1.0]])]});}
            var Q44;
            {var subQ0=sQuery(id+"F0.wireOp",EDGE,"E17");var subQ1=sQuery(id+"F0.wireOp",EDGE,"E6");var subQ2=makeQuery(id+"F0.imprint","INTERSECT",VERTEX,{"derivedFrom":[subQ1,subQ0,sQuery(id+"F0.wireOp",EDGE,"E30")]});Q44=makeQuery(id+"F0.imprint","IMPRINT",FACE,{"disambiguationData":[TD([[makeQuery(id+"F0.imprint","IMPRINT",EDGE,{"disambiguationData":[TD([[subQ2,-1.0]])],"derivedFrom":subQ1}),-1.0]])]});}
            var Q45;
            {var subQ0=sQuery(id+"F0.wireOp",EDGE,"E32");var subQ1=sQuery(id+"F0.wireOp",EDGE,"E10");var subQ2=makeQuery(id+"F0.imprint","INTERSECT",VERTEX,{"derivedFrom":[sQuery(id+"F0.wireOp",EDGE,"E6"),subQ1,subQ0]});Q45=makeQuery(id+"F0.imprint","IMPRINT",FACE,{"disambiguationData":[TD([[makeQuery(id+"F0.imprint","IMPRINT",EDGE,{"disambiguationData":[TD([[subQ2,-1.0]])],"derivedFrom":subQ1}),-1.0]])]});}
            var Q46;
            {var subQ0=sQuery(id+"F0.wireOp",EDGE,"E32");var subQ1=sQuery(id+"F0.wireOp",EDGE,"E14");var subQ2=makeQuery(id+"F0.imprint","INTERSECT",VERTEX,{"derivedFrom":[sQuery(id+"F0.wireOp",EDGE,"E4"),subQ1,subQ0]});Q46=makeQuery(id+"F0.imprint","IMPRINT",FACE,{"disambiguationData":[TD([[makeQuery(id+"F0.imprint","IMPRINT",EDGE,{"disambiguationData":[TD([[subQ2,1.0]])],"derivedFrom":subQ1}),-1.0]])]});}
            var Q47;
            {var subQ0=sQuery(id+"F0.wireOp",EDGE,"E32");var subQ1=sQuery(id+"F0.wireOp",EDGE,"E4");var subQ2=makeQuery(id+"F0.imprint","INTERSECT",VERTEX,{"derivedFrom":[subQ1,sQuery(id+"F0.wireOp",EDGE,"E14"),subQ0]});Q47=makeQuery(id+"F0.imprint","IMPRINT",FACE,{"disambiguationData":[TD([[makeQuery(id+"F0.imprint","IMPRINT",EDGE,{"disambiguationData":[TD([[subQ2,-1.0]])],"derivedFrom":subQ1}),-1.0]])]});}
            var Q48;
            {var subQ0=sQuery(id+"F0.wireOp",EDGE,"E32");var subQ1=sQuery(id+"F0.wireOp",EDGE,"E14");var subQ2=makeQuery(id+"F0.imprint","INTERSECT",VERTEX,{"derivedFrom":[sQuery(id+"F0.wireOp",EDGE,"E4"),subQ1,subQ0]});Q48=makeQuery(id+"F0.imprint","IMPRINT",FACE,{"disambiguationData":[TD([[makeQuery(id+"F0.imprint","IMPRINT",EDGE,{"disambiguationData":[TD([[subQ2,1.0]])],"derivedFrom":subQ1}),-1.0]])]});}
            var Q49;
            {var subQ0=sQuery(id+"F0.wireOp",EDGE,"E36");var subQ1=sQuery(id+"F0.wireOp",EDGE,"E18");var subQ2=makeQuery(id+"F0.imprint","INTERSECT",VERTEX,{"derivedFrom":[sQuery(id+"F0.wireOp",EDGE,"E7"),subQ1,subQ0]});Q49=makeQuery(id+"F0.imprint","IMPRINT",FACE,{"disambiguationData":[TD([[makeQuery(id+"F0.imprint","IMPRINT",EDGE,{"disambiguationData":[TD([[subQ2,1.0]])],"derivedFrom":subQ1}),-1.0]])]});}
            var Q50;
            {var subQ0=sQuery(id+"F0.wireOp",EDGE,"E36");var subQ1=sQuery(id+"F0.wireOp",EDGE,"E7");var subQ2=makeQuery(id+"F0.imprint","INTERSECT",VERTEX,{"derivedFrom":[subQ1,sQuery(id+"F0.wireOp",EDGE,"E18"),subQ0]});Q50=makeQuery(id+"F0.imprint","IMPRINT",FACE,{"disambiguationData":[TD([[makeQuery(id+"F0.imprint","IMPRINT",EDGE,{"disambiguationData":[TD([[subQ2,-1.0]])],"derivedFrom":subQ1}),-1.0]])]});}
            var Q51;
            {var subQ0=sQuery(id+"F0.wireOp",EDGE,"E36");var subQ1=sQuery(id+"F0.wireOp",EDGE,"E19");var subQ2=makeQuery(id+"F0.imprint","INTERSECT",VERTEX,{"derivedFrom":[sQuery(id+"F0.wireOp",EDGE,"E11"),subQ1,subQ0]});Q51=makeQuery(id+"F0.imprint","IMPRINT",FACE,{"disambiguationData":[TD([[makeQuery(id+"F0.imprint","IMPRINT",EDGE,{"disambiguationData":[TD([[subQ2,-1.0]])],"derivedFrom":subQ1}),-1.0]])]});}
            var Q52;
            {var subQ0=sQuery(id+"F0.wireOp",EDGE,"E12");var subQ1=sQuery(id+"F0.wireOp",EDGE,"E3");var subQ2=makeQuery(id+"F0.imprint","INTERSECT",VERTEX,{"derivedFrom":[subQ1,subQ0,sQuery(id+"F0.wireOp",EDGE,"E32")]});Q52=makeQuery(id+"F0.imprint","IMPRINT",FACE,{"disambiguationData":[TD([[makeQuery(id+"F0.imprint","IMPRINT",EDGE,{"disambiguationData":[TD([[subQ2,-1.0]])],"derivedFrom":subQ1}),-1.0]])]});}
            var Q53;
            {var subQ0=sQuery(id+"F0.wireOp",EDGE,"E36");var subQ1=sQuery(id+"F0.wireOp",EDGE,"E17");var subQ2=makeQuery(id+"F0.imprint","INTERSECT",VERTEX,{"derivedFrom":[sQuery(id+"F0.wireOp",EDGE,"E5"),subQ1,subQ0]});Q53=makeQuery(id+"F0.imprint","IMPRINT",FACE,{"disambiguationData":[TD([[makeQuery(id+"F0.imprint","IMPRINT",EDGE,{"disambiguationData":[TD([[subQ2,1.0]])],"derivedFrom":subQ1}),-1.0]])]});}
            var Q54;
            {var subQ0=sQuery(id+"F0.wireOp",EDGE,"E36");var subQ1=sQuery(id+"F0.wireOp",EDGE,"E5");var subQ2=makeQuery(id+"F0.imprint","INTERSECT",VERTEX,{"derivedFrom":[subQ1,sQuery(id+"F0.wireOp",EDGE,"E17"),subQ0]});Q54=makeQuery(id+"F0.imprint","IMPRINT",FACE,{"disambiguationData":[TD([[makeQuery(id+"F0.imprint","IMPRINT",EDGE,{"disambiguationData":[TD([[subQ2,-1.0]])],"derivedFrom":subQ1}),-1.0]])]});}
            var Q55;
            {var subQ0=sQuery(id+"F0.wireOp",EDGE,"E36");var subQ1=sQuery(id+"F0.wireOp",EDGE,"E18");var subQ2=makeQuery(id+"F0.imprint","INTERSECT",VERTEX,{"derivedFrom":[sQuery(id+"F0.wireOp",EDGE,"E10"),subQ1,subQ0]});Q55=makeQuery(id+"F0.imprint","IMPRINT",FACE,{"disambiguationData":[TD([[makeQuery(id+"F0.imprint","IMPRINT",EDGE,{"disambiguationData":[TD([[subQ2,-1.0]])],"derivedFrom":subQ1}),-1.0]])]});}
            var Q56;
            {var subQ0=sQuery(id+"F0.wireOp",EDGE,"E11");var subQ1=sQuery(id+"F0.wireOp",EDGE,"E4");var subQ2=makeQuery(id+"F0.imprint","INTERSECT",VERTEX,{"derivedFrom":[subQ1,subQ0,sQuery(id+"F0.wireOp",EDGE,"E32")]});Q56=makeQuery(id+"F0.imprint","IMPRINT",FACE,{"disambiguationData":[TD([[makeQuery(id+"F0.imprint","IMPRINT",EDGE,{"disambiguationData":[TD([[subQ2,-1.0]])],"derivedFrom":subQ1}),-1.0]])]});}
            var Q57;
            {var subQ0=sQuery(id+"F0.wireOp",EDGE,"E36");var subQ1=sQuery(id+"F0.wireOp",EDGE,"E22");var subQ2=makeQuery(id+"F0.imprint","INTERSECT",VERTEX,{"derivedFrom":[sQuery(id+"F0.wireOp",EDGE,"E3"),subQ1,subQ0]});Q57=makeQuery(id+"F0.imprint","IMPRINT",FACE,{"disambiguationData":[TD([[makeQuery(id+"F0.imprint","IMPRINT",EDGE,{"disambiguationData":[TD([[subQ2,1.0]])],"derivedFrom":subQ1}),-1.0]])]});}
            var Q58;
            {var subQ0=sQuery(id+"F0.wireOp",EDGE,"E36");var subQ1=sQuery(id+"F0.wireOp",EDGE,"E3");var subQ2=makeQuery(id+"F0.imprint","INTERSECT",VERTEX,{"derivedFrom":[subQ1,sQuery(id+"F0.wireOp",EDGE,"E22"),subQ0]});Q58=makeQuery(id+"F0.imprint","IMPRINT",FACE,{"disambiguationData":[TD([[makeQuery(id+"F0.imprint","IMPRINT",EDGE,{"disambiguationData":[TD([[subQ2,-1.0]])],"derivedFrom":subQ1}),-1.0]])]});}
            var Q59;
            {var subQ0=sQuery(id+"F0.wireOp",EDGE,"E36");var subQ1=sQuery(id+"F0.wireOp",EDGE,"E17");var subQ2=makeQuery(id+"F0.imprint","INTERSECT",VERTEX,{"derivedFrom":[sQuery(id+"F0.wireOp",EDGE,"E15"),subQ1,subQ0]});Q59=makeQuery(id+"F0.imprint","IMPRINT",FACE,{"disambiguationData":[TD([[makeQuery(id+"F0.imprint","IMPRINT",EDGE,{"disambiguationData":[TD([[subQ2,-1.0]])],"derivedFrom":subQ1}),-1.0]])]});}
            var Q60;
            {var subQ0=sQuery(id+"F0.wireOp",EDGE,"E10");var subQ1=sQuery(id+"F0.wireOp",EDGE,"E6");var subQ2=makeQuery(id+"F0.imprint","INTERSECT",VERTEX,{"derivedFrom":[subQ1,subQ0,sQuery(id+"F0.wireOp",EDGE,"E32")]});Q60=makeQuery(id+"F0.imprint","IMPRINT",FACE,{"disambiguationData":[TD([[makeQuery(id+"F0.imprint","IMPRINT",EDGE,{"disambiguationData":[TD([[subQ2,-1.0]])],"derivedFrom":subQ1}),-1.0]])]});}
            var Q61;
            {var subQ0=sQuery(id+"F0.wireOp",EDGE,"E36");var subQ1=sQuery(id+"F0.wireOp",EDGE,"E21");var subQ2=makeQuery(id+"F0.imprint","INTERSECT",VERTEX,{"derivedFrom":[sQuery(id+"F0.wireOp",EDGE,"E4"),subQ1,subQ0]});Q61=makeQuery(id+"F0.imprint","IMPRINT",FACE,{"disambiguationData":[TD([[makeQuery(id+"F0.imprint","IMPRINT",EDGE,{"disambiguationData":[TD([[subQ2,1.0]])],"derivedFrom":subQ1}),-1.0]])]});}
            var Q62;
            {var subQ0=sQuery(id+"F0.wireOp",EDGE,"E36");var subQ1=sQuery(id+"F0.wireOp",EDGE,"E4");var subQ2=makeQuery(id+"F0.imprint","INTERSECT",VERTEX,{"derivedFrom":[subQ1,sQuery(id+"F0.wireOp",EDGE,"E21"),subQ0]});Q62=makeQuery(id+"F0.imprint","IMPRINT",FACE,{"disambiguationData":[TD([[makeQuery(id+"F0.imprint","IMPRINT",EDGE,{"disambiguationData":[TD([[subQ2,-1.0]])],"derivedFrom":subQ1}),-1.0]])]});}
            var Q63;
            {var subQ0=sQuery(id+"F0.wireOp",EDGE,"E36");var subQ1=sQuery(id+"F0.wireOp",EDGE,"E22");var subQ2=makeQuery(id+"F0.imprint","INTERSECT",VERTEX,{"derivedFrom":[sQuery(id+"F0.wireOp",EDGE,"E14"),subQ1,subQ0]});Q63=makeQuery(id+"F0.imprint","IMPRINT",FACE,{"disambiguationData":[TD([[makeQuery(id+"F0.imprint","IMPRINT",EDGE,{"disambiguationData":[TD([[subQ2,-1.0]])],"derivedFrom":subQ1}),-1.0]])]});}
            var Q64;
            {var subQ0=sQuery(id+"F0.wireOp",EDGE,"E15");var subQ1=sQuery(id+"F0.wireOp",EDGE,"E8");var subQ2=makeQuery(id+"F0.imprint","INTERSECT",VERTEX,{"derivedFrom":[subQ1,subQ0,sQuery(id+"F0.wireOp",EDGE,"E32")]});Q64=makeQuery(id+"F0.imprint","IMPRINT",FACE,{"disambiguationData":[TD([[makeQuery(id+"F0.imprint","IMPRINT",EDGE,{"disambiguationData":[TD([[subQ2,-1.0]])],"derivedFrom":subQ1}),-1.0]])]});}
            var Q65;
            {var subQ0=sQuery(id+"F0.wireOp",EDGE,"E36");var subQ1=sQuery(id+"F0.wireOp",EDGE,"E20");var subQ2=makeQuery(id+"F0.imprint","INTERSECT",VERTEX,{"derivedFrom":[sQuery(id+"F0.wireOp",EDGE,"E6"),subQ1,subQ0]});Q65=makeQuery(id+"F0.imprint","IMPRINT",FACE,{"disambiguationData":[TD([[makeQuery(id+"F0.imprint","IMPRINT",EDGE,{"disambiguationData":[TD([[subQ2,1.0]])],"derivedFrom":subQ1}),-1.0]])]});}
            var Q66;
            {var subQ0=sQuery(id+"F0.wireOp",EDGE,"E36");var subQ1=sQuery(id+"F0.wireOp",EDGE,"E6");var subQ2=makeQuery(id+"F0.imprint","INTERSECT",VERTEX,{"derivedFrom":[subQ1,sQuery(id+"F0.wireOp",EDGE,"E20"),subQ0]});Q66=makeQuery(id+"F0.imprint","IMPRINT",FACE,{"disambiguationData":[TD([[makeQuery(id+"F0.imprint","IMPRINT",EDGE,{"disambiguationData":[TD([[subQ2,-1.0]])],"derivedFrom":subQ1}),-1.0]])]});}
            var Q67;
            {var subQ0=sQuery(id+"F0.wireOp",EDGE,"E36");var subQ1=sQuery(id+"F0.wireOp",EDGE,"E21");var subQ2=makeQuery(id+"F0.imprint","INTERSECT",VERTEX,{"derivedFrom":[sQuery(id+"F0.wireOp",EDGE,"E13"),subQ1,subQ0]});Q67=makeQuery(id+"F0.imprint","IMPRINT",FACE,{"disambiguationData":[TD([[makeQuery(id+"F0.imprint","IMPRINT",EDGE,{"disambiguationData":[TD([[subQ2,-1.0]])],"derivedFrom":subQ1}),-1.0]])]});}
            var Q68;
            {var subQ0=sQuery(id+"F0.wireOp",EDGE,"E14");var subQ1=sQuery(id+"F0.wireOp",EDGE,"E7");var subQ2=makeQuery(id+"F0.imprint","INTERSECT",VERTEX,{"derivedFrom":[subQ1,subQ0,sQuery(id+"F0.wireOp",EDGE,"E32")]});Q68=makeQuery(id+"F0.imprint","IMPRINT",FACE,{"disambiguationData":[TD([[makeQuery(id+"F0.imprint","IMPRINT",EDGE,{"disambiguationData":[TD([[subQ2,-1.0]])],"derivedFrom":subQ1}),-1.0]])]});}
            var Q69;
            {var subQ0=sQuery(id+"F0.wireOp",EDGE,"E36");var subQ1=sQuery(id+"F0.wireOp",EDGE,"E19");var subQ2=makeQuery(id+"F0.imprint","INTERSECT",VERTEX,{"derivedFrom":[sQuery(id+"F0.wireOp",EDGE,"E8"),subQ1,subQ0]});Q69=makeQuery(id+"F0.imprint","IMPRINT",FACE,{"disambiguationData":[TD([[makeQuery(id+"F0.imprint","IMPRINT",EDGE,{"disambiguationData":[TD([[subQ2,1.0]])],"derivedFrom":subQ1}),-1.0]])]});}
            var Q70;
            {var subQ0=sQuery(id+"F0.wireOp",EDGE,"E36");var subQ1=sQuery(id+"F0.wireOp",EDGE,"E8");var subQ2=makeQuery(id+"F0.imprint","INTERSECT",VERTEX,{"derivedFrom":[subQ1,sQuery(id+"F0.wireOp",EDGE,"E19"),subQ0]});Q70=makeQuery(id+"F0.imprint","IMPRINT",FACE,{"disambiguationData":[TD([[makeQuery(id+"F0.imprint","IMPRINT",EDGE,{"disambiguationData":[TD([[subQ2,-1.0]])],"derivedFrom":subQ1}),-1.0]])]});}
            var Q71;
            {var subQ0=sQuery(id+"F0.wireOp",EDGE,"E36");var subQ1=sQuery(id+"F0.wireOp",EDGE,"E20");var subQ2=makeQuery(id+"F0.imprint","INTERSECT",VERTEX,{"derivedFrom":[sQuery(id+"F0.wireOp",EDGE,"E12"),subQ1,subQ0]});Q71=makeQuery(id+"F0.imprint","IMPRINT",FACE,{"disambiguationData":[TD([[makeQuery(id+"F0.imprint","IMPRINT",EDGE,{"disambiguationData":[TD([[subQ2,-1.0]])],"derivedFrom":subQ1}),-1.0]])]});}
            var Q72;
            {var subQ0=sQuery(id+"F0.wireOp",EDGE,"E13");var subQ1=sQuery(id+"F0.wireOp",EDGE,"E5");var subQ2=makeQuery(id+"F0.imprint","INTERSECT",VERTEX,{"derivedFrom":[subQ1,subQ0,sQuery(id+"F0.wireOp",EDGE,"E32")]});Q72=makeQuery(id+"F0.imprint","IMPRINT",FACE,{"disambiguationData":[TD([[makeQuery(id+"F0.imprint","IMPRINT",EDGE,{"disambiguationData":[TD([[subQ2,-1.0]])],"derivedFrom":subQ1}),-1.0]])]});}
            var Q73;
            {var subQ0=sQuery(id+"F0.wireOp",EDGE,"E40");var subQ1=sQuery(id+"F0.wireOp",EDGE,"E6");var subQ2=makeQuery(id+"F0.imprint","INTERSECT",VERTEX,{"derivedFrom":[sQuery(id+"F0.wireOp",EDGE,"E4"),subQ1,subQ0]});Q73=makeQuery(id+"F0.imprint","IMPRINT",FACE,{"disambiguationData":[TD([[makeQuery(id+"F0.imprint","IMPRINT",EDGE,{"disambiguationData":[TD([[subQ2,1.0]])],"derivedFrom":subQ1}),-1.0]])]});}
            var Q74;
            {var subQ0=sQuery(id+"F0.wireOp",EDGE,"E40");var subQ1=sQuery(id+"F0.wireOp",EDGE,"E10");var subQ2=makeQuery(id+"F0.imprint","INTERSECT",VERTEX,{"derivedFrom":[subQ1,sQuery(id+"F0.wireOp",EDGE,"E15"),subQ0]});Q74=makeQuery(id+"F0.imprint","IMPRINT",FACE,{"disambiguationData":[TD([[makeQuery(id+"F0.imprint","IMPRINT",EDGE,{"disambiguationData":[TD([[subQ2,-1.0]])],"derivedFrom":subQ1}),-1.0]])]});}
            var Q75;
            {var subQ0=sQuery(id+"F0.wireOp",EDGE,"E40");var subQ1=sQuery(id+"F0.wireOp",EDGE,"E15");var subQ2=makeQuery(id+"F0.imprint","INTERSECT",VERTEX,{"derivedFrom":[sQuery(id+"F0.wireOp",EDGE,"E10"),subQ1,subQ0]});Q75=makeQuery(id+"F0.imprint","IMPRINT",FACE,{"disambiguationData":[TD([[makeQuery(id+"F0.imprint","IMPRINT",EDGE,{"disambiguationData":[TD([[subQ2,1.0]])],"derivedFrom":subQ1}),-1.0]])]});}
            var Q76;
            {var subQ0=sQuery(id+"F0.wireOp",EDGE,"E40");var subQ1=sQuery(id+"F0.wireOp",EDGE,"E3");var subQ2=makeQuery(id+"F0.imprint","INTERSECT",VERTEX,{"derivedFrom":[subQ1,sQuery(id+"F0.wireOp",EDGE,"E4"),subQ0]});Q76=makeQuery(id+"F0.imprint","IMPRINT",FACE,{"disambiguationData":[TD([[makeQuery(id+"F0.imprint","IMPRINT",EDGE,{"disambiguationData":[TD([[subQ2,-1.0]])],"derivedFrom":subQ1}),-1.0]])]});}
            var Q77;
            {var subQ0=sQuery(id+"F0.wireOp",EDGE,"E40");var subQ1=sQuery(id+"F0.wireOp",EDGE,"E4");var subQ2=makeQuery(id+"F0.imprint","INTERSECT",VERTEX,{"derivedFrom":[sQuery(id+"F0.wireOp",EDGE,"E3"),subQ1,subQ0]});Q77=makeQuery(id+"F0.imprint","IMPRINT",FACE,{"disambiguationData":[TD([[makeQuery(id+"F0.imprint","IMPRINT",EDGE,{"disambiguationData":[TD([[subQ2,1.0]])],"derivedFrom":subQ1}),-1.0]])]});}
            var Q78;
            {var subQ0=sQuery(id+"F0.wireOp",EDGE,"E40");var subQ1=sQuery(id+"F0.wireOp",EDGE,"E11");var subQ2=makeQuery(id+"F0.imprint","INTERSECT",VERTEX,{"derivedFrom":[sQuery(id+"F0.wireOp",EDGE,"E10"),subQ1,subQ0]});Q78=makeQuery(id+"F0.imprint","IMPRINT",FACE,{"disambiguationData":[TD([[makeQuery(id+"F0.imprint","IMPRINT",EDGE,{"disambiguationData":[TD([[subQ2,-1.0]])],"derivedFrom":subQ1}),-1.0]])]});}
            var Q79;
            {var subQ0=sQuery(id+"F0.wireOp",EDGE,"E18");var subQ1=sQuery(id+"F0.wireOp",EDGE,"E10");var subQ2=makeQuery(id+"F0.imprint","INTERSECT",VERTEX,{"derivedFrom":[subQ1,subQ0,sQuery(id+"F0.wireOp",EDGE,"E36")]});Q79=makeQuery(id+"F0.imprint","IMPRINT",FACE,{"disambiguationData":[TD([[makeQuery(id+"F0.imprint","IMPRINT",EDGE,{"disambiguationData":[TD([[subQ2,-1.0]])],"derivedFrom":subQ1}),-1.0]])]});}
            var Q80;
            {var subQ0=sQuery(id+"F0.wireOp",EDGE,"E40");var subQ1=sQuery(id+"F0.wireOp",EDGE,"E5");var subQ2=makeQuery(id+"F0.imprint","INTERSECT",VERTEX,{"derivedFrom":[sQuery(id+"F0.wireOp",EDGE,"E3"),subQ1,subQ0]});Q80=makeQuery(id+"F0.imprint","IMPRINT",FACE,{"disambiguationData":[TD([[makeQuery(id+"F0.imprint","IMPRINT",EDGE,{"disambiguationData":[TD([[subQ2,-1.0]])],"derivedFrom":subQ1}),-1.0]])]});}
            var Q81;
            {var subQ0=sQuery(id+"F0.wireOp",EDGE,"E27");var subQ1=sQuery(id+"F0.wireOp",EDGE,"E3");var subQ2=makeQuery(id+"F0.imprint","INTERSECT",VERTEX,{"derivedFrom":[subQ1,subQ0,sQuery(id+"F0.wireOp",EDGE,"E36")]});Q81=makeQuery(id+"F0.imprint","IMPRINT",FACE,{"disambiguationData":[TD([[makeQuery(id+"F0.imprint","IMPRINT",EDGE,{"disambiguationData":[TD([[subQ2,-1.0]])],"derivedFrom":subQ1}),-1.0]])]});}
            var Q82;
            {var subQ0=sQuery(id+"F0.wireOp",EDGE,"E40");var subQ1=sQuery(id+"F0.wireOp",EDGE,"E12");var subQ2=makeQuery(id+"F0.imprint","INTERSECT",VERTEX,{"derivedFrom":[sQuery(id+"F0.wireOp",EDGE,"E11"),subQ1,subQ0]});Q82=makeQuery(id+"F0.imprint","IMPRINT",FACE,{"disambiguationData":[TD([[makeQuery(id+"F0.imprint","IMPRINT",EDGE,{"disambiguationData":[TD([[subQ2,-1.0]])],"derivedFrom":subQ1}),-1.0]])]});}
            var Q83;
            {var subQ0=sQuery(id+"F0.wireOp",EDGE,"E19");var subQ1=sQuery(id+"F0.wireOp",EDGE,"E11");var subQ2=makeQuery(id+"F0.imprint","INTERSECT",VERTEX,{"derivedFrom":[subQ1,subQ0,sQuery(id+"F0.wireOp",EDGE,"E36")]});Q83=makeQuery(id+"F0.imprint","IMPRINT",FACE,{"disambiguationData":[TD([[makeQuery(id+"F0.imprint","IMPRINT",EDGE,{"disambiguationData":[TD([[subQ2,-1.0]])],"derivedFrom":subQ1}),-1.0]])]});}
            var Q84;
            {var subQ0=sQuery(id+"F0.wireOp",EDGE,"E40");var subQ1=sQuery(id+"F0.wireOp",EDGE,"E7");var subQ2=makeQuery(id+"F0.imprint","INTERSECT",VERTEX,{"derivedFrom":[sQuery(id+"F0.wireOp",EDGE,"E5"),subQ1,subQ0]});Q84=makeQuery(id+"F0.imprint","IMPRINT",FACE,{"disambiguationData":[TD([[makeQuery(id+"F0.imprint","IMPRINT",EDGE,{"disambiguationData":[TD([[subQ2,-1.0]])],"derivedFrom":subQ1}),-1.0]])]});}
            var Q85;
            {var subQ0=sQuery(id+"F0.wireOp",EDGE,"E28");var subQ1=sQuery(id+"F0.wireOp",EDGE,"E5");var subQ2=makeQuery(id+"F0.imprint","INTERSECT",VERTEX,{"derivedFrom":[subQ1,subQ0,sQuery(id+"F0.wireOp",EDGE,"E36")]});Q85=makeQuery(id+"F0.imprint","IMPRINT",FACE,{"disambiguationData":[TD([[makeQuery(id+"F0.imprint","IMPRINT",EDGE,{"disambiguationData":[TD([[subQ2,-1.0]])],"derivedFrom":subQ1}),-1.0]])]});}
            var Q86;
            {var subQ0=sQuery(id+"F0.wireOp",EDGE,"E40");var subQ1=sQuery(id+"F0.wireOp",EDGE,"E13");var subQ2=makeQuery(id+"F0.imprint","INTERSECT",VERTEX,{"derivedFrom":[sQuery(id+"F0.wireOp",EDGE,"E12"),subQ1,subQ0]});Q86=makeQuery(id+"F0.imprint","IMPRINT",FACE,{"disambiguationData":[TD([[makeQuery(id+"F0.imprint","IMPRINT",EDGE,{"disambiguationData":[TD([[subQ2,-1.0]])],"derivedFrom":subQ1}),-1.0]])]});}
            var Q87;
            {var subQ0=sQuery(id+"F0.wireOp",EDGE,"E20");var subQ1=sQuery(id+"F0.wireOp",EDGE,"E12");var subQ2=makeQuery(id+"F0.imprint","INTERSECT",VERTEX,{"derivedFrom":[subQ1,subQ0,sQuery(id+"F0.wireOp",EDGE,"E36")]});Q87=makeQuery(id+"F0.imprint","IMPRINT",FACE,{"disambiguationData":[TD([[makeQuery(id+"F0.imprint","IMPRINT",EDGE,{"disambiguationData":[TD([[subQ2,-1.0]])],"derivedFrom":subQ1}),-1.0]])]});}
            var Q88;
            {var subQ0=sQuery(id+"F0.wireOp",EDGE,"E40");var subQ1=sQuery(id+"F0.wireOp",EDGE,"E8");var subQ2=makeQuery(id+"F0.imprint","INTERSECT",VERTEX,{"derivedFrom":[sQuery(id+"F0.wireOp",EDGE,"E7"),subQ1,subQ0]});Q88=makeQuery(id+"F0.imprint","IMPRINT",FACE,{"disambiguationData":[TD([[makeQuery(id+"F0.imprint","IMPRINT",EDGE,{"disambiguationData":[TD([[subQ2,-1.0]])],"derivedFrom":subQ1}),-1.0]])]});}
            var Q89;
            {var subQ0=sQuery(id+"F0.wireOp",EDGE,"E29");var subQ1=sQuery(id+"F0.wireOp",EDGE,"E7");var subQ2=makeQuery(id+"F0.imprint","INTERSECT",VERTEX,{"derivedFrom":[subQ1,subQ0,sQuery(id+"F0.wireOp",EDGE,"E36")]});Q89=makeQuery(id+"F0.imprint","IMPRINT",FACE,{"disambiguationData":[TD([[makeQuery(id+"F0.imprint","IMPRINT",EDGE,{"disambiguationData":[TD([[subQ2,-1.0]])],"derivedFrom":subQ1}),-1.0]])]});}
            var Q90;
            {var subQ0=sQuery(id+"F0.wireOp",EDGE,"E40");var subQ1=sQuery(id+"F0.wireOp",EDGE,"E14");var subQ2=makeQuery(id+"F0.imprint","INTERSECT",VERTEX,{"derivedFrom":[sQuery(id+"F0.wireOp",EDGE,"E13"),subQ1,subQ0]});Q90=makeQuery(id+"F0.imprint","IMPRINT",FACE,{"disambiguationData":[TD([[makeQuery(id+"F0.imprint","IMPRINT",EDGE,{"disambiguationData":[TD([[subQ2,-1.0]])],"derivedFrom":subQ1}),-1.0]])]});}
            var Q91;
            {var subQ0=sQuery(id+"F0.wireOp",EDGE,"E21");var subQ1=sQuery(id+"F0.wireOp",EDGE,"E13");var subQ2=makeQuery(id+"F0.imprint","INTERSECT",VERTEX,{"derivedFrom":[subQ1,subQ0,sQuery(id+"F0.wireOp",EDGE,"E36")]});Q91=makeQuery(id+"F0.imprint","IMPRINT",FACE,{"disambiguationData":[TD([[makeQuery(id+"F0.imprint","IMPRINT",EDGE,{"disambiguationData":[TD([[subQ2,-1.0]])],"derivedFrom":subQ1}),-1.0]])]});}
            var Q92;
            {var subQ0=sQuery(id+"F0.wireOp",EDGE,"E40");var subQ1=sQuery(id+"F0.wireOp",EDGE,"E6");var subQ2=makeQuery(id+"F0.imprint","INTERSECT",VERTEX,{"derivedFrom":[subQ1,sQuery(id+"F0.wireOp",EDGE,"E8"),subQ0]});Q92=makeQuery(id+"F0.imprint","IMPRINT",FACE,{"disambiguationData":[TD([[makeQuery(id+"F0.imprint","IMPRINT",EDGE,{"disambiguationData":[TD([[subQ2,-1.0]])],"derivedFrom":subQ1}),-1.0]])]});}
            var Q93;
            {var subQ0=sQuery(id+"F0.wireOp",EDGE,"E40");var subQ1=sQuery(id+"F0.wireOp",EDGE,"E8");var subQ2=makeQuery(id+"F0.imprint","INTERSECT",VERTEX,{"derivedFrom":[sQuery(id+"F0.wireOp",EDGE,"E6"),subQ1,subQ0]});Q93=makeQuery(id+"F0.imprint","IMPRINT",FACE,{"disambiguationData":[TD([[makeQuery(id+"F0.imprint","IMPRINT",EDGE,{"disambiguationData":[TD([[subQ2,1.0]])],"derivedFrom":subQ1}),-1.0]])]});}
            var Q94;
            {var subQ0=sQuery(id+"F0.wireOp",EDGE,"E40");var subQ1=sQuery(id+"F0.wireOp",EDGE,"E15");var subQ2=makeQuery(id+"F0.imprint","INTERSECT",VERTEX,{"derivedFrom":[sQuery(id+"F0.wireOp",EDGE,"E14"),subQ1,subQ0]});Q94=makeQuery(id+"F0.imprint","IMPRINT",FACE,{"disambiguationData":[TD([[makeQuery(id+"F0.imprint","IMPRINT",EDGE,{"disambiguationData":[TD([[subQ2,-1.0]])],"derivedFrom":subQ1}),-1.0]])]});}
            var Q95;
            {var subQ0=sQuery(id+"F0.wireOp",EDGE,"E22");var subQ1=sQuery(id+"F0.wireOp",EDGE,"E14");var subQ2=makeQuery(id+"F0.imprint","INTERSECT",VERTEX,{"derivedFrom":[subQ1,subQ0,sQuery(id+"F0.wireOp",EDGE,"E36")]});Q95=makeQuery(id+"F0.imprint","IMPRINT",FACE,{"disambiguationData":[TD([[makeQuery(id+"F0.imprint","IMPRINT",EDGE,{"disambiguationData":[TD([[subQ2,-1.0]])],"derivedFrom":subQ1}),-1.0]])]});}
            var Q96;
            {var subQ0=sQuery(id+"F0.wireOp",EDGE,"E40");var subQ1=sQuery(id+"F0.wireOp",EDGE,"E4");var subQ2=makeQuery(id+"F0.imprint","INTERSECT",VERTEX,{"derivedFrom":[subQ1,sQuery(id+"F0.wireOp",EDGE,"E6"),subQ0]});Q96=makeQuery(id+"F0.imprint","IMPRINT",FACE,{"disambiguationData":[TD([[makeQuery(id+"F0.imprint","IMPRINT",EDGE,{"disambiguationData":[TD([[subQ2,-1.0]])],"derivedFrom":subQ1}),-1.0]])]});}
            var Q97;
            {var subQ0=sQuery(id+"F0.wireOp",EDGE,"E38");var subQ1=sQuery(id+"F0.wireOp",EDGE,"E10");var subQ2=makeQuery(id+"F0.imprint","INTERSECT",VERTEX,{"derivedFrom":[subQ1,sQuery(id+"F0.wireOp",EDGE,"E22"),subQ0]});Q97=makeQuery(id+"F0.imprint","IMPRINT",FACE,{"disambiguationData":[TD([[makeQuery(id+"F0.imprint","IMPRINT",EDGE,{"disambiguationData":[TD([[subQ2,-1.0]])],"derivedFrom":subQ1}),-1.0]])]});}
            var Q98;
            {var subQ0=sQuery(id+"F0.wireOp",EDGE,"E38");var subQ1=sQuery(id+"F0.wireOp",EDGE,"E24");var subQ2=makeQuery(id+"F0.imprint","INTERSECT",VERTEX,{"derivedFrom":[sQuery(id+"F0.wireOp",EDGE,"E4"),subQ1,subQ0]});Q98=makeQuery(id+"F0.imprint","IMPRINT",FACE,{"disambiguationData":[TD([[makeQuery(id+"F0.imprint","IMPRINT",EDGE,{"disambiguationData":[TD([[subQ2,1.0]])],"derivedFrom":subQ1}),-1.0]])]});}
            var Q99;
            {var subQ0=sQuery(id+"F0.wireOp",EDGE,"E38");var subQ1=sQuery(id+"F0.wireOp",EDGE,"E4");var subQ2=makeQuery(id+"F0.imprint","INTERSECT",VERTEX,{"derivedFrom":[subQ1,sQuery(id+"F0.wireOp",EDGE,"E24"),subQ0]});Q99=makeQuery(id+"F0.imprint","IMPRINT",FACE,{"disambiguationData":[TD([[makeQuery(id+"F0.imprint","IMPRINT",EDGE,{"disambiguationData":[TD([[subQ2,-1.0]])],"derivedFrom":subQ1}),-1.0]])]});}
            var Q100;
            {var subQ0=sQuery(id+"F0.wireOp",EDGE,"E38");var subQ1=sQuery(id+"F0.wireOp",EDGE,"E21");var subQ2=makeQuery(id+"F0.imprint","INTERSECT",VERTEX,{"derivedFrom":[sQuery(id+"F0.wireOp",EDGE,"E15"),subQ1,subQ0]});Q100=makeQuery(id+"F0.imprint","IMPRINT",FACE,{"disambiguationData":[TD([[makeQuery(id+"F0.imprint","IMPRINT",EDGE,{"disambiguationData":[TD([[subQ2,1.0]])],"derivedFrom":subQ1}),-1.0]])]});}
            var Q101;
            {var subQ0=sQuery(id+"F0.wireOp",EDGE,"E15");var subQ1=sQuery(id+"F0.wireOp",EDGE,"E14");var subQ2=makeQuery(id+"F0.imprint","INTERSECT",VERTEX,{"derivedFrom":[subQ1,subQ0,sQuery(id+"F0.wireOp",EDGE,"E40")]});Q101=makeQuery(id+"F0.imprint","IMPRINT",FACE,{"disambiguationData":[TD([[makeQuery(id+"F0.imprint","IMPRINT",EDGE,{"disambiguationData":[TD([[subQ2,-1.0]])],"derivedFrom":subQ1}),-1.0]])]});}
            var Q102;
            {var subQ0=sQuery(id+"F0.wireOp",EDGE,"E38");var subQ1=sQuery(id+"F0.wireOp",EDGE,"E24");var subQ2=makeQuery(id+"F0.imprint","INTERSECT",VERTEX,{"derivedFrom":[sQuery(id+"F0.wireOp",EDGE,"E14"),subQ1,subQ0]});Q102=makeQuery(id+"F0.imprint","IMPRINT",FACE,{"disambiguationData":[TD([[makeQuery(id+"F0.imprint","IMPRINT",EDGE,{"disambiguationData":[TD([[subQ2,-1.0]])],"derivedFrom":subQ1}),-1.0]])]});}
            var Q103;
            {var subQ0=sQuery(id+"F0.wireOp",EDGE,"E38");var subQ1=sQuery(id+"F0.wireOp",EDGE,"E6");var subQ2=makeQuery(id+"F0.imprint","INTERSECT",VERTEX,{"derivedFrom":[subQ1,sQuery(id+"F0.wireOp",EDGE,"E29"),subQ0]});Q103=makeQuery(id+"F0.imprint","IMPRINT",FACE,{"disambiguationData":[TD([[makeQuery(id+"F0.imprint","IMPRINT",EDGE,{"disambiguationData":[TD([[subQ2,-1.0]])],"derivedFrom":subQ1}),-1.0]])]});}
            var Q104;
            {var subQ0=sQuery(id+"F0.wireOp",EDGE,"E38");var subQ1=sQuery(id+"F0.wireOp",EDGE,"E20");var subQ2=makeQuery(id+"F0.imprint","INTERSECT",VERTEX,{"derivedFrom":[sQuery(id+"F0.wireOp",EDGE,"E14"),subQ1,subQ0]});Q104=makeQuery(id+"F0.imprint","IMPRINT",FACE,{"disambiguationData":[TD([[makeQuery(id+"F0.imprint","IMPRINT",EDGE,{"disambiguationData":[TD([[subQ2,1.0]])],"derivedFrom":subQ1}),-1.0]])]});}
            var Q105;
            {var subQ0=sQuery(id+"F0.wireOp",EDGE,"E14");var subQ1=sQuery(id+"F0.wireOp",EDGE,"E13");var subQ2=makeQuery(id+"F0.imprint","INTERSECT",VERTEX,{"derivedFrom":[subQ1,subQ0,sQuery(id+"F0.wireOp",EDGE,"E40")]});Q105=makeQuery(id+"F0.imprint","IMPRINT",FACE,{"disambiguationData":[TD([[makeQuery(id+"F0.imprint","IMPRINT",EDGE,{"disambiguationData":[TD([[subQ2,-1.0]])],"derivedFrom":subQ1}),-1.0]])]});}
            var Q106;
            {var subQ0=sQuery(id+"F0.wireOp",EDGE,"E38");var subQ1=sQuery(id+"F0.wireOp",EDGE,"E28");var subQ2=makeQuery(id+"F0.imprint","INTERSECT",VERTEX,{"derivedFrom":[sQuery(id+"F0.wireOp",EDGE,"E8"),subQ1,subQ0]});Q106=makeQuery(id+"F0.imprint","IMPRINT",FACE,{"disambiguationData":[TD([[makeQuery(id+"F0.imprint","IMPRINT",EDGE,{"disambiguationData":[TD([[subQ2,1.0]])],"derivedFrom":subQ1}),-1.0]])]});}
            var Q107;
            {var subQ0=sQuery(id+"F0.wireOp",EDGE,"E8");var subQ1=sQuery(id+"F0.wireOp",EDGE,"E7");var subQ2=makeQuery(id+"F0.imprint","INTERSECT",VERTEX,{"derivedFrom":[subQ1,subQ0,sQuery(id+"F0.wireOp",EDGE,"E40")]});Q107=makeQuery(id+"F0.imprint","IMPRINT",FACE,{"disambiguationData":[TD([[makeQuery(id+"F0.imprint","IMPRINT",EDGE,{"disambiguationData":[TD([[subQ2,-1.0]])],"derivedFrom":subQ1}),-1.0]])]});}
            var Q108;
            {var subQ0=sQuery(id+"F0.wireOp",EDGE,"E38");var subQ1=sQuery(id+"F0.wireOp",EDGE,"E19");var subQ2=makeQuery(id+"F0.imprint","INTERSECT",VERTEX,{"derivedFrom":[sQuery(id+"F0.wireOp",EDGE,"E13"),subQ1,subQ0]});Q108=makeQuery(id+"F0.imprint","IMPRINT",FACE,{"disambiguationData":[TD([[makeQuery(id+"F0.imprint","IMPRINT",EDGE,{"disambiguationData":[TD([[subQ2,1.0]])],"derivedFrom":subQ1}),-1.0]])]});}
            var Q109;
            {var subQ0=sQuery(id+"F0.wireOp",EDGE,"E13");var subQ1=sQuery(id+"F0.wireOp",EDGE,"E12");var subQ2=makeQuery(id+"F0.imprint","INTERSECT",VERTEX,{"derivedFrom":[subQ1,subQ0,sQuery(id+"F0.wireOp",EDGE,"E40")]});Q109=makeQuery(id+"F0.imprint","IMPRINT",FACE,{"disambiguationData":[TD([[makeQuery(id+"F0.imprint","IMPRINT",EDGE,{"disambiguationData":[TD([[subQ2,-1.0]])],"derivedFrom":subQ1}),-1.0]])]});}
            var Q110;
            {var subQ0=sQuery(id+"F0.wireOp",EDGE,"E38");var subQ1=sQuery(id+"F0.wireOp",EDGE,"E27");var subQ2=makeQuery(id+"F0.imprint","INTERSECT",VERTEX,{"derivedFrom":[sQuery(id+"F0.wireOp",EDGE,"E7"),subQ1,subQ0]});Q110=makeQuery(id+"F0.imprint","IMPRINT",FACE,{"disambiguationData":[TD([[makeQuery(id+"F0.imprint","IMPRINT",EDGE,{"disambiguationData":[TD([[subQ2,1.0]])],"derivedFrom":subQ1}),-1.0]])]});}
            var Q111;
            {var subQ0=sQuery(id+"F0.wireOp",EDGE,"E7");var subQ1=sQuery(id+"F0.wireOp",EDGE,"E5");var subQ2=makeQuery(id+"F0.imprint","INTERSECT",VERTEX,{"derivedFrom":[subQ1,subQ0,sQuery(id+"F0.wireOp",EDGE,"E40")]});Q111=makeQuery(id+"F0.imprint","IMPRINT",FACE,{"disambiguationData":[TD([[makeQuery(id+"F0.imprint","IMPRINT",EDGE,{"disambiguationData":[TD([[subQ2,-1.0]])],"derivedFrom":subQ1}),-1.0]])]});}
            var Q112;
            {var subQ0=sQuery(id+"F0.wireOp",EDGE,"E38");var subQ1=sQuery(id+"F0.wireOp",EDGE,"E18");var subQ2=makeQuery(id+"F0.imprint","INTERSECT",VERTEX,{"derivedFrom":[sQuery(id+"F0.wireOp",EDGE,"E12"),subQ1,subQ0]});Q112=makeQuery(id+"F0.imprint","IMPRINT",FACE,{"disambiguationData":[TD([[makeQuery(id+"F0.imprint","IMPRINT",EDGE,{"disambiguationData":[TD([[subQ2,1.0]])],"derivedFrom":subQ1}),-1.0]])]});}
            var Q113;
            {var subQ0=sQuery(id+"F0.wireOp",EDGE,"E12");var subQ1=sQuery(id+"F0.wireOp",EDGE,"E11");var subQ2=makeQuery(id+"F0.imprint","INTERSECT",VERTEX,{"derivedFrom":[subQ1,subQ0,sQuery(id+"F0.wireOp",EDGE,"E40")]});Q113=makeQuery(id+"F0.imprint","IMPRINT",FACE,{"disambiguationData":[TD([[makeQuery(id+"F0.imprint","IMPRINT",EDGE,{"disambiguationData":[TD([[subQ2,-1.0]])],"derivedFrom":subQ1}),-1.0]])]});}
            var Q114;
            {var subQ0=sQuery(id+"F0.wireOp",EDGE,"E38");var subQ1=sQuery(id+"F0.wireOp",EDGE,"E26");var subQ2=makeQuery(id+"F0.imprint","INTERSECT",VERTEX,{"derivedFrom":[sQuery(id+"F0.wireOp",EDGE,"E5"),subQ1,subQ0]});Q114=makeQuery(id+"F0.imprint","IMPRINT",FACE,{"disambiguationData":[TD([[makeQuery(id+"F0.imprint","IMPRINT",EDGE,{"disambiguationData":[TD([[subQ2,1.0]])],"derivedFrom":subQ1}),-1.0]])]});}
            var Q115;
            {var subQ0=sQuery(id+"F0.wireOp",EDGE,"E5");var subQ1=sQuery(id+"F0.wireOp",EDGE,"E3");var subQ2=makeQuery(id+"F0.imprint","INTERSECT",VERTEX,{"derivedFrom":[subQ1,subQ0,sQuery(id+"F0.wireOp",EDGE,"E40")]});Q115=makeQuery(id+"F0.imprint","IMPRINT",FACE,{"disambiguationData":[TD([[makeQuery(id+"F0.imprint","IMPRINT",EDGE,{"disambiguationData":[TD([[subQ2,-1.0]])],"derivedFrom":subQ1}),-1.0]])]});}
            var Q116;
            {var subQ0=sQuery(id+"F0.wireOp",EDGE,"E38");var subQ1=sQuery(id+"F0.wireOp",EDGE,"E17");var subQ2=makeQuery(id+"F0.imprint","INTERSECT",VERTEX,{"derivedFrom":[sQuery(id+"F0.wireOp",EDGE,"E11"),subQ1,subQ0]});Q116=makeQuery(id+"F0.imprint","IMPRINT",FACE,{"disambiguationData":[TD([[makeQuery(id+"F0.imprint","IMPRINT",EDGE,{"disambiguationData":[TD([[subQ2,1.0]])],"derivedFrom":subQ1}),-1.0]])]});}
            var Q117;
            {var subQ0=sQuery(id+"F0.wireOp",EDGE,"E11");var subQ1=sQuery(id+"F0.wireOp",EDGE,"E10");var subQ2=makeQuery(id+"F0.imprint","INTERSECT",VERTEX,{"derivedFrom":[subQ1,subQ0,sQuery(id+"F0.wireOp",EDGE,"E40")]});Q117=makeQuery(id+"F0.imprint","IMPRINT",FACE,{"disambiguationData":[TD([[makeQuery(id+"F0.imprint","IMPRINT",EDGE,{"disambiguationData":[TD([[subQ2,-1.0]])],"derivedFrom":subQ1}),-1.0]])]});}
            var Q118;
            {var subQ0=sQuery(id+"F0.wireOp",EDGE,"E38");var subQ1=sQuery(id+"F0.wireOp",EDGE,"E25");var subQ2=makeQuery(id+"F0.imprint","INTERSECT",VERTEX,{"derivedFrom":[sQuery(id+"F0.wireOp",EDGE,"E3"),subQ1,subQ0]});Q118=makeQuery(id+"F0.imprint","IMPRINT",FACE,{"disambiguationData":[TD([[makeQuery(id+"F0.imprint","IMPRINT",EDGE,{"disambiguationData":[TD([[subQ2,1.0]])],"derivedFrom":subQ1}),-1.0]])]});}
            var Q119;
            {var subQ0=sQuery(id+"F0.wireOp",EDGE,"E38");var subQ1=sQuery(id+"F0.wireOp",EDGE,"E3");var subQ2=makeQuery(id+"F0.imprint","INTERSECT",VERTEX,{"derivedFrom":[subQ1,sQuery(id+"F0.wireOp",EDGE,"E25"),subQ0]});Q119=makeQuery(id+"F0.imprint","IMPRINT",FACE,{"disambiguationData":[TD([[makeQuery(id+"F0.imprint","IMPRINT",EDGE,{"disambiguationData":[TD([[subQ2,-1.0]])],"derivedFrom":subQ1}),-1.0]])]});}
            var Q120;
            {var subQ0=sQuery(id+"F0.wireOp",EDGE,"E38");var subQ1=sQuery(id+"F0.wireOp",EDGE,"E17");var subQ2=makeQuery(id+"F0.imprint","INTERSECT",VERTEX,{"derivedFrom":[sQuery(id+"F0.wireOp",EDGE,"E4"),subQ1,subQ0]});Q120=makeQuery(id+"F0.imprint","IMPRINT",FACE,{"disambiguationData":[TD([[makeQuery(id+"F0.imprint","IMPRINT",EDGE,{"disambiguationData":[TD([[subQ2,-1.0]])],"derivedFrom":subQ1}),-1.0]])]});}
            var Q121;
            {var subQ0=sQuery(id+"F0.wireOp",EDGE,"E22");var subQ1=sQuery(id+"F0.wireOp",EDGE,"E6");var subQ2=makeQuery(id+"F0.imprint","INTERSECT",VERTEX,{"derivedFrom":[subQ1,subQ0,sQuery(id+"F0.wireOp",EDGE,"E38")]});Q121=makeQuery(id+"F0.imprint","IMPRINT",FACE,{"disambiguationData":[TD([[makeQuery(id+"F0.imprint","IMPRINT",EDGE,{"disambiguationData":[TD([[subQ2,-1.0]])],"derivedFrom":subQ1}),-1.0]])]});}
            var Q122;
            {var subQ0=sQuery(id+"F0.wireOp",EDGE,"E34");var subQ1=sQuery(id+"F0.wireOp",EDGE,"E4");var subQ2=makeQuery(id+"F0.imprint","INTERSECT",VERTEX,{"derivedFrom":[subQ1,sQuery(id+"F0.wireOp",EDGE,"E15"),subQ0]});Q122=makeQuery(id+"F0.imprint","IMPRINT",FACE,{"disambiguationData":[TD([[makeQuery(id+"F0.imprint","IMPRINT",EDGE,{"disambiguationData":[TD([[subQ2,-1.0]])],"derivedFrom":subQ1}),-1.0]])]});}
            var Q123;
            {var subQ0=sQuery(id+"F0.wireOp",EDGE,"E34");var subQ1=sQuery(id+"F0.wireOp",EDGE,"E15");var subQ2=makeQuery(id+"F0.imprint","INTERSECT",VERTEX,{"derivedFrom":[sQuery(id+"F0.wireOp",EDGE,"E4"),subQ1,subQ0]});Q123=makeQuery(id+"F0.imprint","IMPRINT",FACE,{"disambiguationData":[TD([[makeQuery(id+"F0.imprint","IMPRINT",EDGE,{"disambiguationData":[TD([[subQ2,1.0]])],"derivedFrom":subQ1}),-1.0]])]});}
            var Q124;
            {var subQ0=sQuery(id+"F0.wireOp",EDGE,"E34");var subQ1=sQuery(id+"F0.wireOp",EDGE,"E10");var subQ2=makeQuery(id+"F0.imprint","INTERSECT",VERTEX,{"derivedFrom":[sQuery(id+"F0.wireOp",EDGE,"E4"),subQ1,subQ0]});Q124=makeQuery(id+"F0.imprint","IMPRINT",FACE,{"disambiguationData":[TD([[makeQuery(id+"F0.imprint","IMPRINT",EDGE,{"disambiguationData":[TD([[subQ2,-1.0]])],"derivedFrom":subQ1}),-1.0]])]});}
            var Q125;
            {var subQ0=sQuery(id+"F0.wireOp",EDGE,"E17");var subQ1=sQuery(id+"F0.wireOp",EDGE,"E4");var subQ2=makeQuery(id+"F0.imprint","INTERSECT",VERTEX,{"derivedFrom":[subQ1,subQ0,sQuery(id+"F0.wireOp",EDGE,"E38")]});Q125=makeQuery(id+"F0.imprint","IMPRINT",FACE,{"disambiguationData":[TD([[makeQuery(id+"F0.imprint","IMPRINT",EDGE,{"disambiguationData":[TD([[subQ2,-1.0]])],"derivedFrom":subQ1}),-1.0]])]});}
            var Q126;
            {var subQ0=sQuery(id+"F0.wireOp",EDGE,"E34");var subQ1=sQuery(id+"F0.wireOp",EDGE,"E3");var subQ2=makeQuery(id+"F0.imprint","INTERSECT",VERTEX,{"derivedFrom":[subQ1,sQuery(id+"F0.wireOp",EDGE,"E10"),subQ0]});Q126=makeQuery(id+"F0.imprint","IMPRINT",FACE,{"disambiguationData":[TD([[makeQuery(id+"F0.imprint","IMPRINT",EDGE,{"disambiguationData":[TD([[subQ2,-1.0]])],"derivedFrom":subQ1}),-1.0]])]});}
            var Q127;
            {var subQ0=sQuery(id+"F0.wireOp",EDGE,"E34");var subQ1=sQuery(id+"F0.wireOp",EDGE,"E10");var subQ2=makeQuery(id+"F0.imprint","INTERSECT",VERTEX,{"derivedFrom":[sQuery(id+"F0.wireOp",EDGE,"E3"),subQ1,subQ0]});Q127=makeQuery(id+"F0.imprint","IMPRINT",FACE,{"disambiguationData":[TD([[makeQuery(id+"F0.imprint","IMPRINT",EDGE,{"disambiguationData":[TD([[subQ2,1.0]])],"derivedFrom":subQ1}),-1.0]])]});}
            var Q128;
            {var subQ0=sQuery(id+"F0.wireOp",EDGE,"E34");var subQ1=sQuery(id+"F0.wireOp",EDGE,"E11");var subQ2=makeQuery(id+"F0.imprint","INTERSECT",VERTEX,{"derivedFrom":[sQuery(id+"F0.wireOp",EDGE,"E3"),subQ1,subQ0]});Q128=makeQuery(id+"F0.imprint","IMPRINT",FACE,{"disambiguationData":[TD([[makeQuery(id+"F0.imprint","IMPRINT",EDGE,{"disambiguationData":[TD([[subQ2,-1.0]])],"derivedFrom":subQ1}),-1.0]])]});}
            var Q129;
            {var subQ0=sQuery(id+"F0.wireOp",EDGE,"E18");var subQ1=sQuery(id+"F0.wireOp",EDGE,"E3");var subQ2=makeQuery(id+"F0.imprint","INTERSECT",VERTEX,{"derivedFrom":[subQ1,subQ0,sQuery(id+"F0.wireOp",EDGE,"E38")]});Q129=makeQuery(id+"F0.imprint","IMPRINT",FACE,{"disambiguationData":[TD([[makeQuery(id+"F0.imprint","IMPRINT",EDGE,{"disambiguationData":[TD([[subQ2,-1.0]])],"derivedFrom":subQ1}),-1.0]])]});}
            var Q130;
            {var subQ0=sQuery(id+"F0.wireOp",EDGE,"E34");var subQ1=sQuery(id+"F0.wireOp",EDGE,"E5");var subQ2=makeQuery(id+"F0.imprint","INTERSECT",VERTEX,{"derivedFrom":[subQ1,sQuery(id+"F0.wireOp",EDGE,"E11"),subQ0]});Q130=makeQuery(id+"F0.imprint","IMPRINT",FACE,{"disambiguationData":[TD([[makeQuery(id+"F0.imprint","IMPRINT",EDGE,{"disambiguationData":[TD([[subQ2,-1.0]])],"derivedFrom":subQ1}),-1.0]])]});}
            var Q131;
            {var subQ0=sQuery(id+"F0.wireOp",EDGE,"E34");var subQ1=sQuery(id+"F0.wireOp",EDGE,"E11");var subQ2=makeQuery(id+"F0.imprint","INTERSECT",VERTEX,{"derivedFrom":[sQuery(id+"F0.wireOp",EDGE,"E5"),subQ1,subQ0]});Q131=makeQuery(id+"F0.imprint","IMPRINT",FACE,{"disambiguationData":[TD([[makeQuery(id+"F0.imprint","IMPRINT",EDGE,{"disambiguationData":[TD([[subQ2,1.0]])],"derivedFrom":subQ1}),-1.0]])]});}
            var Q132;
            {var subQ0=sQuery(id+"F0.wireOp",EDGE,"E34");var subQ1=sQuery(id+"F0.wireOp",EDGE,"E12");var subQ2=makeQuery(id+"F0.imprint","INTERSECT",VERTEX,{"derivedFrom":[sQuery(id+"F0.wireOp",EDGE,"E5"),subQ1,subQ0]});Q132=makeQuery(id+"F0.imprint","IMPRINT",FACE,{"disambiguationData":[TD([[makeQuery(id+"F0.imprint","IMPRINT",EDGE,{"disambiguationData":[TD([[subQ2,-1.0]])],"derivedFrom":subQ1}),-1.0]])]});}
            var Q133;
            {var subQ0=sQuery(id+"F0.wireOp",EDGE,"E34");var subQ1=sQuery(id+"F0.wireOp",EDGE,"E7");var subQ2=makeQuery(id+"F0.imprint","INTERSECT",VERTEX,{"derivedFrom":[subQ1,sQuery(id+"F0.wireOp",EDGE,"E12"),subQ0]});Q133=makeQuery(id+"F0.imprint","IMPRINT",FACE,{"disambiguationData":[TD([[makeQuery(id+"F0.imprint","IMPRINT",EDGE,{"disambiguationData":[TD([[subQ2,-1.0]])],"derivedFrom":subQ1}),-1.0]])]});}
            var Q134;
            {var subQ0=sQuery(id+"F0.wireOp",EDGE,"E34");var subQ1=sQuery(id+"F0.wireOp",EDGE,"E12");var subQ2=makeQuery(id+"F0.imprint","INTERSECT",VERTEX,{"derivedFrom":[sQuery(id+"F0.wireOp",EDGE,"E7"),subQ1,subQ0]});Q134=makeQuery(id+"F0.imprint","IMPRINT",FACE,{"disambiguationData":[TD([[makeQuery(id+"F0.imprint","IMPRINT",EDGE,{"disambiguationData":[TD([[subQ2,1.0]])],"derivedFrom":subQ1}),-1.0]])]});}
            var Q135;
            {var subQ0=sQuery(id+"F0.wireOp",EDGE,"E34");var subQ1=sQuery(id+"F0.wireOp",EDGE,"E13");var subQ2=makeQuery(id+"F0.imprint","INTERSECT",VERTEX,{"derivedFrom":[sQuery(id+"F0.wireOp",EDGE,"E7"),subQ1,subQ0]});Q135=makeQuery(id+"F0.imprint","IMPRINT",FACE,{"disambiguationData":[TD([[makeQuery(id+"F0.imprint","IMPRINT",EDGE,{"disambiguationData":[TD([[subQ2,-1.0]])],"derivedFrom":subQ1}),-1.0]])]});}
            var Q136;
            {var subQ0=sQuery(id+"F0.wireOp",EDGE,"E20");var subQ1=sQuery(id+"F0.wireOp",EDGE,"E7");var subQ2=makeQuery(id+"F0.imprint","INTERSECT",VERTEX,{"derivedFrom":[subQ1,subQ0,sQuery(id+"F0.wireOp",EDGE,"E38")]});Q136=makeQuery(id+"F0.imprint","IMPRINT",FACE,{"disambiguationData":[TD([[makeQuery(id+"F0.imprint","IMPRINT",EDGE,{"disambiguationData":[TD([[subQ2,-1.0]])],"derivedFrom":subQ1}),-1.0]])]});}
            var Q137;
            {var subQ0=sQuery(id+"F0.wireOp",EDGE,"E34");var subQ1=sQuery(id+"F0.wireOp",EDGE,"E8");var subQ2=makeQuery(id+"F0.imprint","INTERSECT",VERTEX,{"derivedFrom":[subQ1,sQuery(id+"F0.wireOp",EDGE,"E13"),subQ0]});Q137=makeQuery(id+"F0.imprint","IMPRINT",FACE,{"disambiguationData":[TD([[makeQuery(id+"F0.imprint","IMPRINT",EDGE,{"disambiguationData":[TD([[subQ2,-1.0]])],"derivedFrom":subQ1}),-1.0]])]});}
            var Q138;
            {var subQ0=sQuery(id+"F0.wireOp",EDGE,"E34");var subQ1=sQuery(id+"F0.wireOp",EDGE,"E13");var subQ2=makeQuery(id+"F0.imprint","INTERSECT",VERTEX,{"derivedFrom":[sQuery(id+"F0.wireOp",EDGE,"E8"),subQ1,subQ0]});Q138=makeQuery(id+"F0.imprint","IMPRINT",FACE,{"disambiguationData":[TD([[makeQuery(id+"F0.imprint","IMPRINT",EDGE,{"disambiguationData":[TD([[subQ2,1.0]])],"derivedFrom":subQ1}),-1.0]])]});}
            var Q139;
            {var subQ0=sQuery(id+"F0.wireOp",EDGE,"E34");var subQ1=sQuery(id+"F0.wireOp",EDGE,"E14");var subQ2=makeQuery(id+"F0.imprint","INTERSECT",VERTEX,{"derivedFrom":[sQuery(id+"F0.wireOp",EDGE,"E8"),subQ1,subQ0]});Q139=makeQuery(id+"F0.imprint","IMPRINT",FACE,{"disambiguationData":[TD([[makeQuery(id+"F0.imprint","IMPRINT",EDGE,{"disambiguationData":[TD([[subQ2,-1.0]])],"derivedFrom":subQ1}),-1.0]])]});}
            var Q140;
            {var subQ0=sQuery(id+"F0.wireOp",EDGE,"E21");var subQ1=sQuery(id+"F0.wireOp",EDGE,"E8");var subQ2=makeQuery(id+"F0.imprint","INTERSECT",VERTEX,{"derivedFrom":[subQ1,subQ0,sQuery(id+"F0.wireOp",EDGE,"E38")]});Q140=makeQuery(id+"F0.imprint","IMPRINT",FACE,{"disambiguationData":[TD([[makeQuery(id+"F0.imprint","IMPRINT",EDGE,{"disambiguationData":[TD([[subQ2,-1.0]])],"derivedFrom":subQ1}),-1.0]])]});}
            var Q141;
            {var subQ0=sQuery(id+"F0.wireOp",EDGE,"E34");var subQ1=sQuery(id+"F0.wireOp",EDGE,"E6");var subQ2=makeQuery(id+"F0.imprint","INTERSECT",VERTEX,{"derivedFrom":[subQ1,sQuery(id+"F0.wireOp",EDGE,"E14"),subQ0]});Q141=makeQuery(id+"F0.imprint","IMPRINT",FACE,{"disambiguationData":[TD([[makeQuery(id+"F0.imprint","IMPRINT",EDGE,{"disambiguationData":[TD([[subQ2,-1.0]])],"derivedFrom":subQ1}),-1.0]])]});}
            var Q142;
            {var subQ0=sQuery(id+"F0.wireOp",EDGE,"E34");var subQ1=sQuery(id+"F0.wireOp",EDGE,"E14");var subQ2=makeQuery(id+"F0.imprint","INTERSECT",VERTEX,{"derivedFrom":[sQuery(id+"F0.wireOp",EDGE,"E6"),subQ1,subQ0]});Q142=makeQuery(id+"F0.imprint","IMPRINT",FACE,{"disambiguationData":[TD([[makeQuery(id+"F0.imprint","IMPRINT",EDGE,{"disambiguationData":[TD([[subQ2,1.0]])],"derivedFrom":subQ1}),-1.0]])]});}
            var Q143;
            {var subQ0=sQuery(id+"F0.wireOp",EDGE,"E34");var subQ1=sQuery(id+"F0.wireOp",EDGE,"E15");var subQ2=makeQuery(id+"F0.imprint","INTERSECT",VERTEX,{"derivedFrom":[sQuery(id+"F0.wireOp",EDGE,"E6"),subQ1,subQ0]});Q143=makeQuery(id+"F0.imprint","IMPRINT",FACE,{"disambiguationData":[TD([[makeQuery(id+"F0.imprint","IMPRINT",EDGE,{"disambiguationData":[TD([[subQ2,-1.0]])],"derivedFrom":subQ1}),-1.0]])]});}
            var Q144;
            {var subQ0=sQuery(id+"F0.wireOp",EDGE,"E24");var subQ1=sQuery(id+"F0.wireOp",EDGE,"E6");var subQ2=makeQuery(id+"F0.imprint","INTERSECT",VERTEX,{"derivedFrom":[subQ1,subQ0]});Q144=makeQuery(id+"F0.imprint","IMPRINT",FACE,{"disambiguationData":[TD([[makeQuery(id+"F0.imprint","IMPRINT",EDGE,{"disambiguationData":[TD([[subQ2,-1.0]])],"derivedFrom":subQ1}),1.0]])]});}
            var Q145;
            {var subQ0=sQuery(id+"F0.wireOp",EDGE,"E21");var subQ1=sQuery(id+"F0.wireOp",EDGE,"E6");var subQ2=makeQuery(id+"F0.imprint","INTERSECT",VERTEX,{"derivedFrom":[subQ1,subQ0]});Q145=makeQuery(id+"F0.imprint","IMPRINT",FACE,{"disambiguationData":[TD([[makeQuery(id+"F0.imprint","IMPRINT",EDGE,{"disambiguationData":[TD([[subQ2,-1.0]])],"derivedFrom":subQ0}),1.0]])]});}
            var Q146;
            {var subQ0=sQuery(id+"F0.wireOp",EDGE,"E21");var subQ1=sQuery(id+"F0.wireOp",EDGE,"E14");var subQ2=makeQuery(id+"F0.imprint","INTERSECT",VERTEX,{"derivedFrom":[subQ1,subQ0]});Q146=makeQuery(id+"F0.imprint","IMPRINT",FACE,{"disambiguationData":[TD([[makeQuery(id+"F0.imprint","IMPRINT",EDGE,{"disambiguationData":[TD([[subQ2,-1.0]])],"derivedFrom":subQ1}),1.0]])]});}
            var Q147;
            {var subQ0=sQuery(id+"F0.wireOp",EDGE,"E29");var subQ1=sQuery(id+"F0.wireOp",EDGE,"E8");var subQ2=makeQuery(id+"F0.imprint","INTERSECT",VERTEX,{"derivedFrom":[subQ1,subQ0]});Q147=makeQuery(id+"F0.imprint","IMPRINT",FACE,{"disambiguationData":[TD([[makeQuery(id+"F0.imprint","IMPRINT",EDGE,{"disambiguationData":[TD([[subQ2,1.0]])],"derivedFrom":subQ0}),1.0]])]});}
            var Q148;
            {var subQ0=sQuery(id+"F0.wireOp",EDGE,"E29");var subQ1=sQuery(id+"F0.wireOp",EDGE,"E8");var subQ2=makeQuery(id+"F0.imprint","INTERSECT",VERTEX,{"derivedFrom":[subQ1,subQ0]});Q148=makeQuery(id+"F0.imprint","IMPRINT",FACE,{"disambiguationData":[TD([[makeQuery(id+"F0.imprint","IMPRINT",EDGE,{"disambiguationData":[TD([[subQ2,-1.0]])],"derivedFrom":subQ1}),1.0]])]});}
            var Q149;
            {var subQ0=sQuery(id+"F0.wireOp",EDGE,"E20");var subQ1=sQuery(id+"F0.wireOp",EDGE,"E8");var subQ2=makeQuery(id+"F0.imprint","INTERSECT",VERTEX,{"derivedFrom":[subQ1,subQ0]});Q149=makeQuery(id+"F0.imprint","IMPRINT",FACE,{"disambiguationData":[TD([[makeQuery(id+"F0.imprint","IMPRINT",EDGE,{"disambiguationData":[TD([[subQ2,-1.0]])],"derivedFrom":subQ0}),1.0]])]});}
            var Q150;
            {var subQ0=sQuery(id+"F0.wireOp",EDGE,"E20");var subQ1=sQuery(id+"F0.wireOp",EDGE,"E13");var subQ2=makeQuery(id+"F0.imprint","INTERSECT",VERTEX,{"derivedFrom":[subQ1,subQ0]});Q150=makeQuery(id+"F0.imprint","IMPRINT",FACE,{"disambiguationData":[TD([[makeQuery(id+"F0.imprint","IMPRINT",EDGE,{"disambiguationData":[TD([[subQ2,-1.0]])],"derivedFrom":subQ1}),1.0]])]});}
            var Q151;
            {var subQ0=sQuery(id+"F0.wireOp",EDGE,"E28");var subQ1=sQuery(id+"F0.wireOp",EDGE,"E7");var subQ2=makeQuery(id+"F0.imprint","INTERSECT",VERTEX,{"derivedFrom":[subQ1,subQ0]});Q151=makeQuery(id+"F0.imprint","IMPRINT",FACE,{"disambiguationData":[TD([[makeQuery(id+"F0.imprint","IMPRINT",EDGE,{"disambiguationData":[TD([[subQ2,1.0]])],"derivedFrom":subQ0}),1.0]])]});}
            var Q152;
            {var subQ0=sQuery(id+"F0.wireOp",EDGE,"E28");var subQ1=sQuery(id+"F0.wireOp",EDGE,"E7");var subQ2=makeQuery(id+"F0.imprint","INTERSECT",VERTEX,{"derivedFrom":[subQ1,subQ0]});Q152=makeQuery(id+"F0.imprint","IMPRINT",FACE,{"disambiguationData":[TD([[makeQuery(id+"F0.imprint","IMPRINT",EDGE,{"disambiguationData":[TD([[subQ2,-1.0]])],"derivedFrom":subQ1}),1.0]])]});}
            var Q153;
            {var subQ0=sQuery(id+"F0.wireOp",EDGE,"E19");var subQ1=sQuery(id+"F0.wireOp",EDGE,"E7");var subQ2=makeQuery(id+"F0.imprint","INTERSECT",VERTEX,{"derivedFrom":[subQ1,subQ0]});Q153=makeQuery(id+"F0.imprint","IMPRINT",FACE,{"disambiguationData":[TD([[makeQuery(id+"F0.imprint","IMPRINT",EDGE,{"disambiguationData":[TD([[subQ2,-1.0]])],"derivedFrom":subQ0}),1.0]])]});}
            var Q154;
            {var subQ0=sQuery(id+"F0.wireOp",EDGE,"E19");var subQ1=sQuery(id+"F0.wireOp",EDGE,"E12");var subQ2=makeQuery(id+"F0.imprint","INTERSECT",VERTEX,{"derivedFrom":[subQ1,subQ0]});Q154=makeQuery(id+"F0.imprint","IMPRINT",FACE,{"disambiguationData":[TD([[makeQuery(id+"F0.imprint","IMPRINT",EDGE,{"disambiguationData":[TD([[subQ2,-1.0]])],"derivedFrom":subQ1}),1.0]])]});}
            var Q155;
            {var subQ0=sQuery(id+"F0.wireOp",EDGE,"E27");var subQ1=sQuery(id+"F0.wireOp",EDGE,"E5");var subQ2=makeQuery(id+"F0.imprint","INTERSECT",VERTEX,{"derivedFrom":[subQ1,subQ0]});Q155=makeQuery(id+"F0.imprint","IMPRINT",FACE,{"disambiguationData":[TD([[makeQuery(id+"F0.imprint","IMPRINT",EDGE,{"disambiguationData":[TD([[subQ2,1.0]])],"derivedFrom":subQ0}),1.0]])]});}
            var Q156;
            {var subQ0=sQuery(id+"F0.wireOp",EDGE,"E27");var subQ1=sQuery(id+"F0.wireOp",EDGE,"E5");var subQ2=makeQuery(id+"F0.imprint","INTERSECT",VERTEX,{"derivedFrom":[subQ1,subQ0]});Q156=makeQuery(id+"F0.imprint","IMPRINT",FACE,{"disambiguationData":[TD([[makeQuery(id+"F0.imprint","IMPRINT",EDGE,{"disambiguationData":[TD([[subQ2,-1.0]])],"derivedFrom":subQ1}),1.0]])]});}
            var Q157;
            {var subQ0=sQuery(id+"F0.wireOp",EDGE,"E18");var subQ1=sQuery(id+"F0.wireOp",EDGE,"E5");var subQ2=makeQuery(id+"F0.imprint","INTERSECT",VERTEX,{"derivedFrom":[subQ1,subQ0]});Q157=makeQuery(id+"F0.imprint","IMPRINT",FACE,{"disambiguationData":[TD([[makeQuery(id+"F0.imprint","IMPRINT",EDGE,{"disambiguationData":[TD([[subQ2,-1.0]])],"derivedFrom":subQ0}),1.0]])]});}
            var Q158;
            {var subQ0=sQuery(id+"F0.wireOp",EDGE,"E18");var subQ1=sQuery(id+"F0.wireOp",EDGE,"E11");var subQ2=makeQuery(id+"F0.imprint","INTERSECT",VERTEX,{"derivedFrom":[subQ1,subQ0]});Q158=makeQuery(id+"F0.imprint","IMPRINT",FACE,{"disambiguationData":[TD([[makeQuery(id+"F0.imprint","IMPRINT",EDGE,{"disambiguationData":[TD([[subQ2,-1.0]])],"derivedFrom":subQ1}),1.0]])]});}
            var Q159;
            {var subQ0=sQuery(id+"F0.wireOp",EDGE,"E26");var subQ1=sQuery(id+"F0.wireOp",EDGE,"E3");var subQ2=makeQuery(id+"F0.imprint","INTERSECT",VERTEX,{"derivedFrom":[subQ1,subQ0]});Q159=makeQuery(id+"F0.imprint","IMPRINT",FACE,{"disambiguationData":[TD([[makeQuery(id+"F0.imprint","IMPRINT",EDGE,{"disambiguationData":[TD([[subQ2,1.0]])],"derivedFrom":subQ0}),1.0]])]});}
            var Q160;
            {var subQ0=sQuery(id+"F0.wireOp",EDGE,"E17");var subQ1=sQuery(id+"F0.wireOp",EDGE,"E3");var subQ2=makeQuery(id+"F0.imprint","INTERSECT",VERTEX,{"derivedFrom":[subQ1,subQ0]});Q160=makeQuery(id+"F0.imprint","IMPRINT",FACE,{"disambiguationData":[TD([[makeQuery(id+"F0.imprint","IMPRINT",EDGE,{"disambiguationData":[TD([[subQ2,1.0]])],"derivedFrom":subQ1}),1.0]])]});}
            var Q161;
            {var subQ0=sQuery(id+"F0.wireOp",EDGE,"E17");var subQ1=sQuery(id+"F0.wireOp",EDGE,"E3");var subQ2=makeQuery(id+"F0.imprint","INTERSECT",VERTEX,{"derivedFrom":[subQ1,subQ0]});Q161=makeQuery(id+"F0.imprint","IMPRINT",FACE,{"disambiguationData":[TD([[makeQuery(id+"F0.imprint","IMPRINT",EDGE,{"disambiguationData":[TD([[subQ2,-1.0]])],"derivedFrom":subQ0}),1.0]])]});}
            var Q162;
            {var subQ0=sQuery(id+"F0.wireOp",EDGE,"E17");var subQ1=sQuery(id+"F0.wireOp",EDGE,"E10");var subQ2=makeQuery(id+"F0.imprint","INTERSECT",VERTEX,{"derivedFrom":[subQ1,subQ0]});Q162=makeQuery(id+"F0.imprint","IMPRINT",FACE,{"disambiguationData":[TD([[makeQuery(id+"F0.imprint","IMPRINT",EDGE,{"disambiguationData":[TD([[subQ2,-1.0]])],"derivedFrom":subQ1}),1.0]])]});}
            var Q163;
            {var subQ0=sQuery(id+"F0.wireOp",EDGE,"E25");var subQ1=sQuery(id+"F0.wireOp",EDGE,"E4");var subQ2=makeQuery(id+"F0.imprint","INTERSECT",VERTEX,{"derivedFrom":[subQ1,subQ0]});Q163=makeQuery(id+"F0.imprint","IMPRINT",FACE,{"disambiguationData":[TD([[makeQuery(id+"F0.imprint","IMPRINT",EDGE,{"disambiguationData":[TD([[subQ2,1.0]])],"derivedFrom":subQ0}),1.0]])]});}
            var Q164;
            {var subQ0=sQuery(id+"F0.wireOp",EDGE,"E25");var subQ1=sQuery(id+"F0.wireOp",EDGE,"E4");var subQ2=makeQuery(id+"F0.imprint","INTERSECT",VERTEX,{"derivedFrom":[subQ1,subQ0]});Q164=makeQuery(id+"F0.imprint","IMPRINT",FACE,{"disambiguationData":[TD([[makeQuery(id+"F0.imprint","IMPRINT",EDGE,{"disambiguationData":[TD([[subQ2,-1.0]])],"derivedFrom":subQ1}),1.0]])]});}
            var Q165;
            {var subQ0=sQuery(id+"F0.wireOp",EDGE,"E22");var subQ1=sQuery(id+"F0.wireOp",EDGE,"E4");var subQ2=makeQuery(id+"F0.imprint","INTERSECT",VERTEX,{"derivedFrom":[subQ1,subQ0]});Q165=makeQuery(id+"F0.imprint","IMPRINT",FACE,{"disambiguationData":[TD([[makeQuery(id+"F0.imprint","IMPRINT",EDGE,{"disambiguationData":[TD([[subQ2,-1.0]])],"derivedFrom":subQ0}),1.0]])]});}
            var Q166;
            {var subQ0=sQuery(id+"F0.wireOp",EDGE,"E22");var subQ1=sQuery(id+"F0.wireOp",EDGE,"E15");var subQ2=makeQuery(id+"F0.imprint","INTERSECT",VERTEX,{"derivedFrom":[subQ1,subQ0]});Q166=makeQuery(id+"F0.imprint","IMPRINT",FACE,{"disambiguationData":[TD([[makeQuery(id+"F0.imprint","IMPRINT",EDGE,{"disambiguationData":[TD([[subQ2,-1.0]])],"derivedFrom":subQ1}),1.0]])]});}
            var Q167;
            {var subQ0=sQuery(id+"F0.wireOp",EDGE,"E24");var subQ1=sQuery(id+"F0.wireOp",EDGE,"E6");var subQ2=makeQuery(id+"F0.imprint","INTERSECT",VERTEX,{"derivedFrom":[subQ1,subQ0]});Q167=makeQuery(id+"F0.imprint","IMPRINT",FACE,{"disambiguationData":[TD([[makeQuery(id+"F0.imprint","IMPRINT",EDGE,{"disambiguationData":[TD([[subQ2,1.0]])],"derivedFrom":subQ0}),1.0]])]});}
            var Q168;
            {var subQ0=sQuery(id+"F0.wireOp",EDGE,"E24");var subQ1=sQuery(id+"F0.wireOp",EDGE,"E6");var subQ2=makeQuery(id+"F0.imprint","INTERSECT",VERTEX,{"derivedFrom":[subQ1,subQ0]});Q168=makeQuery(id+"F0.imprint","IMPRINT",FACE,{"disambiguationData":[TD([[makeQuery(id+"F0.imprint","IMPRINT",EDGE,{"disambiguationData":[TD([[subQ2,1.0]])],"derivedFrom":subQ0}),1.0]])]});}
            var Q169;
            {var subQ0=sQuery(id+"F0.wireOp",EDGE,"E22");var subQ1=sQuery(id+"F0.wireOp",EDGE,"E15");var subQ2=makeQuery(id+"F0.imprint","INTERSECT",VERTEX,{"derivedFrom":[subQ1,subQ0]});Q169=makeQuery(id+"F0.imprint","IMPRINT",FACE,{"disambiguationData":[TD([[makeQuery(id+"F0.imprint","IMPRINT",EDGE,{"disambiguationData":[TD([[subQ2,-1.0]])],"derivedFrom":subQ1}),1.0]])]});}
            var Q170;
            {var subQ0=sQuery(id+"F0.wireOp",EDGE,"E22");var subQ1=sQuery(id+"F0.wireOp",EDGE,"E4");var subQ2=makeQuery(id+"F0.imprint","INTERSECT",VERTEX,{"derivedFrom":[subQ1,subQ0]});Q170=makeQuery(id+"F0.imprint","IMPRINT",FACE,{"disambiguationData":[TD([[makeQuery(id+"F0.imprint","IMPRINT",EDGE,{"disambiguationData":[TD([[subQ2,-1.0]])],"derivedFrom":subQ0}),1.0]])]});}
            var Q171;
            {var subQ0=sQuery(id+"F0.wireOp",EDGE,"E25");var subQ1=sQuery(id+"F0.wireOp",EDGE,"E4");var subQ2=makeQuery(id+"F0.imprint","INTERSECT",VERTEX,{"derivedFrom":[subQ1,subQ0]});Q171=makeQuery(id+"F0.imprint","IMPRINT",FACE,{"disambiguationData":[TD([[makeQuery(id+"F0.imprint","IMPRINT",EDGE,{"disambiguationData":[TD([[subQ2,-1.0]])],"derivedFrom":subQ1}),1.0]])]});}
            var Q172;
            {var subQ0=sQuery(id+"F0.wireOp",EDGE,"E25");var subQ1=sQuery(id+"F0.wireOp",EDGE,"E4");var subQ2=makeQuery(id+"F0.imprint","INTERSECT",VERTEX,{"derivedFrom":[subQ1,subQ0]});Q172=makeQuery(id+"F0.imprint","IMPRINT",FACE,{"disambiguationData":[TD([[makeQuery(id+"F0.imprint","IMPRINT",EDGE,{"disambiguationData":[TD([[subQ2,1.0]])],"derivedFrom":subQ0}),1.0]])]});}
            var Q173;
            {var subQ0=sQuery(id+"F0.wireOp",EDGE,"E19");var subQ1=sQuery(id+"F0.wireOp",EDGE,"E5");var subQ2=makeQuery(id+"F0.imprint","INTERSECT",VERTEX,{"derivedFrom":[subQ1,subQ0,sQuery(id+"F0.wireOp",EDGE,"E38")]});Q173=makeQuery(id+"F0.imprint","IMPRINT",FACE,{"disambiguationData":[TD([[makeQuery(id+"F0.imprint","IMPRINT",EDGE,{"disambiguationData":[TD([[subQ2,-1.0]])],"derivedFrom":subQ1}),-1.0]])]});}
            extrude(context, id + "F5", {"entities" : qUnion([Q0, Q1, Q2, Q3, Q4, Q5, Q6, Q7, Q8, Q9, Q10, Q11, Q12, Q13, Q14, Q15, Q16, Q17, Q18, Q19, Q20, Q21, Q22, Q23, Q24, Q25, Q26, Q27, Q28, Q29, Q30, Q31, Q32, Q33, Q34, Q35, Q36, Q37, Q38, Q39, Q40, Q41, Q42, Q43, Q44, Q45, Q46, Q47, Q48, Q49, Q50, Q51, Q52, Q53, Q54, Q55, Q56, Q57, Q58, Q59, Q60, Q61, Q62, Q63, Q64, Q65, Q66, Q67, Q68, Q69, Q70, Q71, Q72, Q73, Q74, Q75, Q76, Q77, Q78, Q79, Q80, Q81, Q82, Q83, Q84, Q85, Q86, Q87, Q88, Q89, Q90, Q91, Q92, Q93, Q94, Q95, Q96, Q97, Q98, Q99, Q100, Q101, Q102, Q103, Q104, Q105, Q106, Q107, Q108, Q109, Q110, Q111, Q112, Q113, Q114, Q115, Q116, Q117, Q118, Q119, Q120, Q121, Q122, Q123, Q124, Q125, Q126, Q127, Q128, Q129, Q130, Q131, Q132, Q133, Q134, Q135, Q136, Q137, Q138, Q139, Q140, Q141, Q142, Q143, Q144, Q145, Q146, Q147, Q148, Q149, Q150, Q151, Q152, Q153, Q154, Q155, Q156, Q157, Q158, Q159, Q160, Q161, Q162, Q163, Q164, Q165, Q166, Q167, Q168, Q169, Q170, Q171, Q172, Q173]), "depth" : 12 * mm, "hasDraft" : true, "draftAngle" : 6 * degree, "draftPullDirection" : true});
        }
        {
            var Q0;
            Q0=qCreatedBy(makeId("Top.planeOp"),FACE);
            cPlane(context, id + "F6", {"entities" : qUnion([Q0]), "cplaneType" : CPlaneType.OFFSET, "offset" : 0 * mm, "width" : 150 * mm, "height" : 150 * mm});
        }
        {
            var Q0;
            Q0=qCreatedBy(id+"F6.planeOp",FACE);
            var sketch = newSketch(context, id + "F7", { "sketchPlane" : qUnion([Q0])});
            skCircle(sketch, "E152", {"center": v(0, 0) * mm, "radius": 30 * mm});
            skSolve(sketch);
        }
        {
            var Q0;
            Q0=qCreatedBy(makeId("Front.planeOp"),FACE);
            var sketch = newSketch(context, id + "F8", { "sketchPlane" : qUnion([Q0])});
            skLineSegment(sketch, "E153", {"start": v(0, 30) * mm, "end": v(0, -30) * mm, "construction": true});
            skArc(sketch, "E154", {"start": v(30, 0) * mm, "mid": v(0, 30) * mm, "end": v(-30, 0) * mm});
            skSolve(sketch);
        }
        {
            var Q0;
            Q0=qCreatedBy(makeId("Top.planeOp"),FACE);
            var sketch = newSketch(context, id + "F9", { "sketchPlane" : qUnion([Q0])});
            skCircle(sketch, "E155.0", {"center": v(0, 0) * mm, "radius": 30 * mm});
            skSolve(sketch);
        }
        {
            var Q0;
            Q0 = qSketchRegion(id + "F9", true);
            extrude(context, id + "F10", {"entities" : qUnion([Q0]), "oppositeDirection" : true, "depth" : 0.25 * mm});
        }
        {
            var Q0;
            Q0=qCreatedBy(makeId("Top.planeOp"),FACE);
            var sketch = newSketch(context, id + "F11", { "sketchPlane" : qUnion([Q0])});
            skCircle(sketch, "E156.0", {"center": v(0, 0) * mm, "radius": 30 * mm});
            skCircle(sketch, "E157", {"center": v(0, 0) * mm, "radius": 29 * mm});
            skCircle(sketch, "E158.0", {"center": v(0, 0) * mm, "radius": 28.98 * mm});
            skSolve(sketch);
        }
        {
            var Q0;
            Q0=makeQuery(id+"F10.opExtrude","CAP_FACE",FACE,{"disambiguationData":[OSD([sQuery(id+"F9.wireOp",EDGE,"E155.0")])],"isStart":false});
            cPlane(context, id + "F12", {"entities" : qUnion([Q0]), "cplaneType" : CPlaneType.OFFSET, "offset" : 0 * mm, "width" : 150 * mm, "height" : 150 * mm});
        }
        {
            var Q0;
            Q0=qCreatedBy(makeId("Top.planeOp"),FACE);
            cPlane(context, id + "F13", {"entities" : qUnion([Q0]), "cplaneType" : CPlaneType.OFFSET, "offset" : 20 * mm, "oppositeDirection" : true, "width" : 150 * mm, "height" : 150 * mm});
        }
        {
            var Q0;
            Q0=makeQuery(id+"F3.opExtrude","SWEPT_BODY",BODY,{"disambiguationData":[OSD([sQuery(id+"F2.wireOp",EDGE,"E95.0.0"),sQuery(id+"F2.wireOp",EDGE,"E96.0.0"),sQuery(id+"F2.wireOp",EDGE,"E139.0.1"),sQuery(id+"F2.wireOp",EDGE,"E140.0.0")])]});
            var Q1;
            Q1=makeQuery(id+"F3.opExtrude","SWEPT_BODY",BODY,{"disambiguationData":[OSD([sQuery(id+"F2.wireOp",EDGE,"E95.0.1"),sQuery(id+"F2.wireOp",EDGE,"E118.0.0"),sQuery(id+"F2.wireOp",EDGE,"E140.0.1"),sQuery(id+"F2.wireOp",EDGE,"E141.0.1")])]});
            var Q2;
            Q2=makeQuery(id+"F3.opExtrude","SWEPT_BODY",BODY,{"disambiguationData":[OSD([sQuery(id+"F2.wireOp",EDGE,"E96.0.2"),sQuery(id+"F2.wireOp",EDGE,"E97.0.1"),sQuery(id+"F2.wireOp",EDGE,"E138.0.1"),sQuery(id+"F2.wireOp",EDGE,"E139.0.0")])]});
            var Q3;
            Q3=makeQuery(id+"F3.opExtrude","SWEPT_BODY",BODY,{"disambiguationData":[OSD([sQuery(id+"F2.wireOp",EDGE,"E97.0.0"),sQuery(id+"F2.wireOp",EDGE,"E98.0.0"),sQuery(id+"F2.wireOp",EDGE,"E137.0.0"),sQuery(id+"F2.wireOp",EDGE,"E138.0.0")])]});
            var Q4;
            Q4=makeQuery(id+"F3.opExtrude","SWEPT_BODY",BODY,{"disambiguationData":[OSD([sQuery(id+"F2.wireOp",EDGE,"E98.0.2"),sQuery(id+"F2.wireOp",EDGE,"E99.0.0"),sQuery(id+"F2.wireOp",EDGE,"E136.0.0"),sQuery(id+"F2.wireOp",EDGE,"E137.0.1")])]});
            var Q5;
            Q5=makeQuery(id+"F3.opExtrude","SWEPT_BODY",BODY,{"disambiguationData":[OSD([sQuery(id+"F2.wireOp",EDGE,"E99.0.2"),sQuery(id+"F2.wireOp",EDGE,"E100.0.0"),sQuery(id+"F2.wireOp",EDGE,"E135.0.0"),sQuery(id+"F2.wireOp",EDGE,"E136.0.1")])]});
            var Q6;
            Q6=makeQuery(id+"F3.opExtrude","SWEPT_BODY",BODY,{"disambiguationData":[OSD([sQuery(id+"F2.wireOp",EDGE,"E100.0.2"),sQuery(id+"F2.wireOp",EDGE,"E101.0.0"),sQuery(id+"F2.wireOp",EDGE,"E134.0.1"),sQuery(id+"F2.wireOp",EDGE,"E135.0.1")])]});
            var Q7;
            Q7=makeQuery(id+"F3.opExtrude","SWEPT_BODY",BODY,{"disambiguationData":[OSD([sQuery(id+"F2.wireOp",EDGE,"E101.0.2"),sQuery(id+"F2.wireOp",EDGE,"E102.0.1"),sQuery(id+"F2.wireOp",EDGE,"E133.0.1"),sQuery(id+"F2.wireOp",EDGE,"E134.0.0")])]});
            var Q8;
            Q8=makeQuery(id+"F3.opExtrude","SWEPT_BODY",BODY,{"disambiguationData":[OSD([sQuery(id+"F2.wireOp",EDGE,"E102.0.0"),sQuery(id+"F2.wireOp",EDGE,"E103.0.0"),sQuery(id+"F2.wireOp",EDGE,"E132.0.0"),sQuery(id+"F2.wireOp",EDGE,"E133.0.0")])]});
            var Q9;
            Q9=makeQuery(id+"F3.opExtrude","SWEPT_BODY",BODY,{"disambiguationData":[OSD([sQuery(id+"F2.wireOp",EDGE,"E103.0.2"),sQuery(id+"F2.wireOp",EDGE,"E104.0.0"),sQuery(id+"F2.wireOp",EDGE,"E131.0.0"),sQuery(id+"F2.wireOp",EDGE,"E132.0.1")])]});
            var Q10;
            Q10=makeQuery(id+"F3.opExtrude","SWEPT_BODY",BODY,{"disambiguationData":[OSD([sQuery(id+"F2.wireOp",EDGE,"E104.0.2"),sQuery(id+"F2.wireOp",EDGE,"E105.0.1"),sQuery(id+"F2.wireOp",EDGE,"E130.0.1"),sQuery(id+"F2.wireOp",EDGE,"E131.0.1")])]});
            var Q11;
            Q11=makeQuery(id+"F3.opExtrude","SWEPT_BODY",BODY,{"disambiguationData":[OSD([sQuery(id+"F2.wireOp",EDGE,"E105.0.0"),sQuery(id+"F2.wireOp",EDGE,"E106.0.0"),sQuery(id+"F2.wireOp",EDGE,"E129.0.0"),sQuery(id+"F2.wireOp",EDGE,"E130.0.0")])]});
            var Q12;
            Q12=makeQuery(id+"F3.opExtrude","SWEPT_BODY",BODY,{"disambiguationData":[OSD([sQuery(id+"F2.wireOp",EDGE,"E106.0.2"),sQuery(id+"F2.wireOp",EDGE,"E107.0.0"),sQuery(id+"F2.wireOp",EDGE,"E128.0.0"),sQuery(id+"F2.wireOp",EDGE,"E129.0.1")])]});
            var Q13;
            Q13=makeQuery(id+"F3.opExtrude","SWEPT_BODY",BODY,{"disambiguationData":[OSD([sQuery(id+"F2.wireOp",EDGE,"E107.0.2"),sQuery(id+"F2.wireOp",EDGE,"E108.0.0"),sQuery(id+"F2.wireOp",EDGE,"E127.0.0"),sQuery(id+"F2.wireOp",EDGE,"E128.0.1")])]});
            var Q14;
            Q14=makeQuery(id+"F3.opExtrude","SWEPT_BODY",BODY,{"disambiguationData":[OSD([sQuery(id+"F2.wireOp",EDGE,"E108.0.2"),sQuery(id+"F2.wireOp",EDGE,"E109.0.0"),sQuery(id+"F2.wireOp",EDGE,"E126.0.1"),sQuery(id+"F2.wireOp",EDGE,"E127.0.1")])]});
            var Q15;
            Q15=makeQuery(id+"F3.opExtrude","SWEPT_BODY",BODY,{"disambiguationData":[OSD([sQuery(id+"F2.wireOp",EDGE,"E109.0.2"),sQuery(id+"F2.wireOp",EDGE,"E110.0.1"),sQuery(id+"F2.wireOp",EDGE,"E125.0.1"),sQuery(id+"F2.wireOp",EDGE,"E126.0.0")])]});
            var Q16;
            Q16=makeQuery(id+"F3.opExtrude","SWEPT_BODY",BODY,{"disambiguationData":[OSD([sQuery(id+"F2.wireOp",EDGE,"E110.0.0"),sQuery(id+"F2.wireOp",EDGE,"E111.0.0"),sQuery(id+"F2.wireOp",EDGE,"E124.0.1"),sQuery(id+"F2.wireOp",EDGE,"E125.0.0")])]});
            var Q17;
            Q17=makeQuery(id+"F3.opExtrude","SWEPT_BODY",BODY,{"disambiguationData":[OSD([sQuery(id+"F2.wireOp",EDGE,"E111.0.2"),sQuery(id+"F2.wireOp",EDGE,"E112.0.1"),sQuery(id+"F2.wireOp",EDGE,"E123.0.1"),sQuery(id+"F2.wireOp",EDGE,"E124.0.0")])]});
            var Q18;
            Q18=makeQuery(id+"F3.opExtrude","SWEPT_BODY",BODY,{"disambiguationData":[OSD([sQuery(id+"F2.wireOp",EDGE,"E112.0.0"),sQuery(id+"F2.wireOp",EDGE,"E113.0.1"),sQuery(id+"F2.wireOp",EDGE,"E122.0.1"),sQuery(id+"F2.wireOp",EDGE,"E123.0.0")])]});
            var Q19;
            Q19=makeQuery(id+"F3.opExtrude","SWEPT_BODY",BODY,{"disambiguationData":[OSD([sQuery(id+"F2.wireOp",EDGE,"E113.0.0"),sQuery(id+"F2.wireOp",EDGE,"E114.0.0"),sQuery(id+"F2.wireOp",EDGE,"E121.0.1"),sQuery(id+"F2.wireOp",EDGE,"E122.0.0")])]});
            var Q20;
            Q20=makeQuery(id+"F3.opExtrude","SWEPT_BODY",BODY,{"disambiguationData":[OSD([sQuery(id+"F2.wireOp",EDGE,"E114.0.2"),sQuery(id+"F2.wireOp",EDGE,"E115.0.0"),sQuery(id+"F2.wireOp",EDGE,"E120.0.0"),sQuery(id+"F2.wireOp",EDGE,"E121.0.0")])]});
            var Q21;
            Q21=makeQuery(id+"F3.opExtrude","SWEPT_BODY",BODY,{"disambiguationData":[OSD([sQuery(id+"F2.wireOp",EDGE,"E115.0.2"),sQuery(id+"F2.wireOp",EDGE,"E116.0.0"),sQuery(id+"F2.wireOp",EDGE,"E120.0.1"),sQuery(id+"F2.wireOp",EDGE,"E119.0.0")])]});
            var Q22;
            Q22=makeQuery(id+"F3.opExtrude","SWEPT_BODY",BODY,{"disambiguationData":[OSD([sQuery(id+"F2.wireOp",EDGE,"E116.0.2"),sQuery(id+"F2.wireOp",EDGE,"E117.0.0"),sQuery(id+"F2.wireOp",EDGE,"E142.0.0"),sQuery(id+"F2.wireOp",EDGE,"E119.0.1")])]});
            var Q23;
            Q23=makeQuery(id+"F3.opExtrude","SWEPT_BODY",BODY,{"disambiguationData":[OSD([sQuery(id+"F2.wireOp",EDGE,"E117.0.2"),sQuery(id+"F2.wireOp",EDGE,"E118.0.1"),sQuery(id+"F2.wireOp",EDGE,"E141.0.0"),sQuery(id+"F2.wireOp",EDGE,"E142.0.1")])]});
            var Q24;
            Q24=makeQuery(id+"F4.opExtrude","SWEPT_BODY",BODY,{"disambiguationData":[OSD([sQuery(id+"F0.wireOp",EDGE,"E0"),sQuery(id+"F0.wireOp",EDGE,"E5"),sQuery(id+"F0.wireOp",EDGE,"E22")])]});
            var Q25;
            Q25=makeQuery(id+"F4.opExtrude","SWEPT_BODY",BODY,{"disambiguationData":[OSD([sQuery(id+"F0.wireOp",EDGE,"E0"),sQuery(id+"F0.wireOp",EDGE,"E15"),sQuery(id+"F0.wireOp",EDGE,"E18")])]});
            var Q26;
            Q26=makeQuery(id+"F4.opExtrude","SWEPT_BODY",BODY,{"disambiguationData":[OSD([sQuery(id+"F0.wireOp",EDGE,"E0"),sQuery(id+"F0.wireOp",EDGE,"E11"),sQuery(id+"F0.wireOp",EDGE,"E24")])]});
            var Q27;
            Q27=makeQuery(id+"F4.opExtrude","SWEPT_BODY",BODY,{"disambiguationData":[OSD([sQuery(id+"F0.wireOp",EDGE,"E0"),sQuery(id+"F0.wireOp",EDGE,"E6"),sQuery(id+"F0.wireOp",EDGE,"E26")])]});
            var Q28;
            Q28=makeQuery(id+"F4.opExtrude","SWEPT_BODY",BODY,{"disambiguationData":[OSD([sQuery(id+"F0.wireOp",EDGE,"E0"),sQuery(id+"F0.wireOp",EDGE,"E3"),sQuery(id+"F0.wireOp",EDGE,"E21")])]});
            var Q29;
            Q29=makeQuery(id+"F4.opExtrude","SWEPT_BODY",BODY,{"disambiguationData":[OSD([sQuery(id+"F0.wireOp",EDGE,"E0"),sQuery(id+"F0.wireOp",EDGE,"E14"),sQuery(id+"F0.wireOp",EDGE,"E17")])]});
            var Q30;
            Q30=makeQuery(id+"F4.opExtrude","SWEPT_BODY",BODY,{"disambiguationData":[OSD([sQuery(id+"F0.wireOp",EDGE,"E0"),sQuery(id+"F0.wireOp",EDGE,"E10"),sQuery(id+"F0.wireOp",EDGE,"E29")])]});
            var Q31;
            Q31=makeQuery(id+"F4.opExtrude","SWEPT_BODY",BODY,{"disambiguationData":[OSD([sQuery(id+"F0.wireOp",EDGE,"E0"),sQuery(id+"F0.wireOp",EDGE,"E8"),sQuery(id+"F0.wireOp",EDGE,"E25")])]});
            var Q32;
            Q32=makeQuery(id+"F4.opExtrude","SWEPT_BODY",BODY,{"disambiguationData":[OSD([sQuery(id+"F0.wireOp",EDGE,"E0"),sQuery(id+"F0.wireOp",EDGE,"E4"),sQuery(id+"F0.wireOp",EDGE,"E20")])]});
            var Q33;
            Q33=makeQuery(id+"F4.opExtrude","SWEPT_BODY",BODY,{"disambiguationData":[OSD([sQuery(id+"F0.wireOp",EDGE,"E0"),sQuery(id+"F0.wireOp",EDGE,"E13"),sQuery(id+"F0.wireOp",EDGE,"E22")])]});
            var Q34;
            Q34=makeQuery(id+"F4.opExtrude","SWEPT_BODY",BODY,{"disambiguationData":[OSD([sQuery(id+"F0.wireOp",EDGE,"E0"),sQuery(id+"F0.wireOp",EDGE,"E15"),sQuery(id+"F0.wireOp",EDGE,"E28")])]});
            var Q35;
            Q35=makeQuery(id+"F4.opExtrude","SWEPT_BODY",BODY,{"disambiguationData":[OSD([sQuery(id+"F0.wireOp",EDGE,"E0"),sQuery(id+"F0.wireOp",EDGE,"E7"),sQuery(id+"F0.wireOp",EDGE,"E24")])]});
            var Q36;
            Q36=makeQuery(id+"F4.opExtrude","SWEPT_BODY",BODY,{"disambiguationData":[OSD([sQuery(id+"F0.wireOp",EDGE,"E0"),sQuery(id+"F0.wireOp",EDGE,"E6"),sQuery(id+"F0.wireOp",EDGE,"E19")])]});
            var Q37;
            Q37=makeQuery(id+"F4.opExtrude","SWEPT_BODY",BODY,{"disambiguationData":[OSD([sQuery(id+"F0.wireOp",EDGE,"E0"),sQuery(id+"F0.wireOp",EDGE,"E12"),sQuery(id+"F0.wireOp",EDGE,"E21")])]});
            var Q38;
            Q38=makeQuery(id+"F4.opExtrude","SWEPT_BODY",BODY,{"disambiguationData":[OSD([sQuery(id+"F0.wireOp",EDGE,"E0"),sQuery(id+"F0.wireOp",EDGE,"E14"),sQuery(id+"F0.wireOp",EDGE,"E27")])]});
            var Q39;
            Q39=makeQuery(id+"F4.opExtrude","SWEPT_BODY",BODY,{"disambiguationData":[OSD([sQuery(id+"F0.wireOp",EDGE,"E0"),sQuery(id+"F0.wireOp",EDGE,"E5"),sQuery(id+"F0.wireOp",EDGE,"E29")])]});
            var Q40;
            Q40=makeQuery(id+"F4.opExtrude","SWEPT_BODY",BODY,{"disambiguationData":[OSD([sQuery(id+"F0.wireOp",EDGE,"E0"),sQuery(id+"F0.wireOp",EDGE,"E8"),sQuery(id+"F0.wireOp",EDGE,"E18")])]});
            var Q41;
            Q41=makeQuery(id+"F4.opExtrude","SWEPT_BODY",BODY,{"disambiguationData":[OSD([sQuery(id+"F0.wireOp",EDGE,"E0"),sQuery(id+"F0.wireOp",EDGE,"E11"),sQuery(id+"F0.wireOp",EDGE,"E20")])]});
            var Q42;
            Q42=makeQuery(id+"F4.opExtrude","SWEPT_BODY",BODY,{"disambiguationData":[OSD([sQuery(id+"F0.wireOp",EDGE,"E0"),sQuery(id+"F0.wireOp",EDGE,"E13"),sQuery(id+"F0.wireOp",EDGE,"E26")])]});
            var Q43;
            Q43=makeQuery(id+"F4.opExtrude","SWEPT_BODY",BODY,{"disambiguationData":[OSD([sQuery(id+"F0.wireOp",EDGE,"E0"),sQuery(id+"F0.wireOp",EDGE,"E3"),sQuery(id+"F0.wireOp",EDGE,"E28")])]});
            var Q44;
            Q44=makeQuery(id+"F4.opExtrude","SWEPT_BODY",BODY,{"disambiguationData":[OSD([sQuery(id+"F0.wireOp",EDGE,"E0"),sQuery(id+"F0.wireOp",EDGE,"E7"),sQuery(id+"F0.wireOp",EDGE,"E17")])]});
            var Q45;
            Q45=makeQuery(id+"F4.opExtrude","SWEPT_BODY",BODY,{"disambiguationData":[OSD([sQuery(id+"F0.wireOp",EDGE,"E0"),sQuery(id+"F0.wireOp",EDGE,"E10"),sQuery(id+"F0.wireOp",EDGE,"E19")])]});
            var Q46;
            Q46=makeQuery(id+"F4.opExtrude","SWEPT_BODY",BODY,{"disambiguationData":[OSD([sQuery(id+"F0.wireOp",EDGE,"E0"),sQuery(id+"F0.wireOp",EDGE,"E12"),sQuery(id+"F0.wireOp",EDGE,"E25")])]});
            var Q47;
            Q47=makeQuery(id+"F4.opExtrude","SWEPT_BODY",BODY,{"disambiguationData":[OSD([sQuery(id+"F0.wireOp",EDGE,"E0"),sQuery(id+"F0.wireOp",EDGE,"E4"),sQuery(id+"F0.wireOp",EDGE,"E27")])]});
            var Q48;
            Q48=makeQuery(id+"F4.opExtrude","SWEPT_BODY",BODY,{"disambiguationData":[OSD([sQuery(id+"F0.wireOp",EDGE,"E3"),sQuery(id+"F0.wireOp",EDGE,"E14"),sQuery(id+"F0.wireOp",EDGE,"E42")])]});
            var Q49;
            Q49=makeQuery(id+"F4.opExtrude","SWEPT_BODY",BODY,{"disambiguationData":[OSD([sQuery(id+"F0.wireOp",EDGE,"E3"),sQuery(id+"F0.wireOp",EDGE,"E13"),sQuery(id+"F0.wireOp",EDGE,"E42")])]});
            var Q50;
            Q50=makeQuery(id+"F4.opExtrude","SWEPT_BODY",BODY,{"disambiguationData":[OSD([sQuery(id+"F0.wireOp",EDGE,"E4"),sQuery(id+"F0.wireOp",EDGE,"E13"),sQuery(id+"F0.wireOp",EDGE,"E42")])]});
            var Q51;
            Q51=makeQuery(id+"F4.opExtrude","SWEPT_BODY",BODY,{"disambiguationData":[OSD([sQuery(id+"F0.wireOp",EDGE,"E4"),sQuery(id+"F0.wireOp",EDGE,"E12"),sQuery(id+"F0.wireOp",EDGE,"E42")])]});
            var Q52;
            Q52=makeQuery(id+"F4.opExtrude","SWEPT_BODY",BODY,{"disambiguationData":[OSD([sQuery(id+"F0.wireOp",EDGE,"E5"),sQuery(id+"F0.wireOp",EDGE,"E15"),sQuery(id+"F0.wireOp",EDGE,"E42")])]});
            var Q53;
            Q53=makeQuery(id+"F4.opExtrude","SWEPT_BODY",BODY,{"disambiguationData":[OSD([sQuery(id+"F0.wireOp",EDGE,"E5"),sQuery(id+"F0.wireOp",EDGE,"E14"),sQuery(id+"F0.wireOp",EDGE,"E42")])]});
            var Q54;
            Q54=makeQuery(id+"F4.opExtrude","SWEPT_BODY",BODY,{"disambiguationData":[OSD([sQuery(id+"F0.wireOp",EDGE,"E6"),sQuery(id+"F0.wireOp",EDGE,"E12"),sQuery(id+"F0.wireOp",EDGE,"E42")])]});
            var Q55;
            Q55=makeQuery(id+"F4.opExtrude","SWEPT_BODY",BODY,{"disambiguationData":[OSD([sQuery(id+"F0.wireOp",EDGE,"E6"),sQuery(id+"F0.wireOp",EDGE,"E11"),sQuery(id+"F0.wireOp",EDGE,"E42")])]});
            var Q56;
            Q56=makeQuery(id+"F4.opExtrude","SWEPT_BODY",BODY,{"disambiguationData":[OSD([sQuery(id+"F0.wireOp",EDGE,"E7"),sQuery(id+"F0.wireOp",EDGE,"E10"),sQuery(id+"F0.wireOp",EDGE,"E42")])]});
            var Q57;
            Q57=makeQuery(id+"F4.opExtrude","SWEPT_BODY",BODY,{"disambiguationData":[OSD([sQuery(id+"F0.wireOp",EDGE,"E7"),sQuery(id+"F0.wireOp",EDGE,"E15"),sQuery(id+"F0.wireOp",EDGE,"E42")])]});
            var Q58;
            Q58=makeQuery(id+"F4.opExtrude","SWEPT_BODY",BODY,{"disambiguationData":[OSD([sQuery(id+"F0.wireOp",EDGE,"E8"),sQuery(id+"F0.wireOp",EDGE,"E10"),sQuery(id+"F0.wireOp",EDGE,"E42")])]});
            var Q59;
            Q59=makeQuery(id+"F4.opExtrude","SWEPT_BODY",BODY,{"disambiguationData":[OSD([sQuery(id+"F0.wireOp",EDGE,"E8"),sQuery(id+"F0.wireOp",EDGE,"E11"),sQuery(id+"F0.wireOp",EDGE,"E42")])]});
            var Q60;
            Q60=makeQuery(id+"F4.opExtrude","SWEPT_BODY",BODY,{"disambiguationData":[OSD([sQuery(id+"F0.wireOp",EDGE,"E17"),sQuery(id+"F0.wireOp",EDGE,"E29"),sQuery(id+"F0.wireOp",EDGE,"E42")])]});
            var Q61;
            Q61=makeQuery(id+"F4.opExtrude","SWEPT_BODY",BODY,{"disambiguationData":[OSD([sQuery(id+"F0.wireOp",EDGE,"E17"),sQuery(id+"F0.wireOp",EDGE,"E28"),sQuery(id+"F0.wireOp",EDGE,"E42")])]});
            var Q62;
            Q62=makeQuery(id+"F4.opExtrude","SWEPT_BODY",BODY,{"disambiguationData":[OSD([sQuery(id+"F0.wireOp",EDGE,"E18"),sQuery(id+"F0.wireOp",EDGE,"E24"),sQuery(id+"F0.wireOp",EDGE,"E42")])]});
            var Q63;
            Q63=makeQuery(id+"F4.opExtrude","SWEPT_BODY",BODY,{"disambiguationData":[OSD([sQuery(id+"F0.wireOp",EDGE,"E18"),sQuery(id+"F0.wireOp",EDGE,"E29"),sQuery(id+"F0.wireOp",EDGE,"E42")])]});
            var Q64;
            Q64=makeQuery(id+"F4.opExtrude","SWEPT_BODY",BODY,{"disambiguationData":[OSD([sQuery(id+"F0.wireOp",EDGE,"E19"),sQuery(id+"F0.wireOp",EDGE,"E25"),sQuery(id+"F0.wireOp",EDGE,"E42")])]});
            var Q65;
            Q65=makeQuery(id+"F4.opExtrude","SWEPT_BODY",BODY,{"disambiguationData":[OSD([sQuery(id+"F0.wireOp",EDGE,"E19"),sQuery(id+"F0.wireOp",EDGE,"E24"),sQuery(id+"F0.wireOp",EDGE,"E42")])]});
            var Q66;
            Q66=makeQuery(id+"F4.opExtrude","SWEPT_BODY",BODY,{"disambiguationData":[OSD([sQuery(id+"F0.wireOp",EDGE,"E20"),sQuery(id+"F0.wireOp",EDGE,"E25"),sQuery(id+"F0.wireOp",EDGE,"E42")])]});
            var Q67;
            Q67=makeQuery(id+"F4.opExtrude","SWEPT_BODY",BODY,{"disambiguationData":[OSD([sQuery(id+"F0.wireOp",EDGE,"E20"),sQuery(id+"F0.wireOp",EDGE,"E26"),sQuery(id+"F0.wireOp",EDGE,"E42")])]});
            var Q68;
            Q68=makeQuery(id+"F4.opExtrude","SWEPT_BODY",BODY,{"disambiguationData":[OSD([sQuery(id+"F0.wireOp",EDGE,"E21"),sQuery(id+"F0.wireOp",EDGE,"E27"),sQuery(id+"F0.wireOp",EDGE,"E42")])]});
            var Q69;
            Q69=makeQuery(id+"F4.opExtrude","SWEPT_BODY",BODY,{"disambiguationData":[OSD([sQuery(id+"F0.wireOp",EDGE,"E21"),sQuery(id+"F0.wireOp",EDGE,"E26"),sQuery(id+"F0.wireOp",EDGE,"E42")])]});
            var Q70;
            Q70=makeQuery(id+"F4.opExtrude","SWEPT_BODY",BODY,{"disambiguationData":[OSD([sQuery(id+"F0.wireOp",EDGE,"E22"),sQuery(id+"F0.wireOp",EDGE,"E28"),sQuery(id+"F0.wireOp",EDGE,"E42")])]});
            var Q71;
            Q71=makeQuery(id+"F4.opExtrude","SWEPT_BODY",BODY,{"disambiguationData":[OSD([sQuery(id+"F0.wireOp",EDGE,"E22"),sQuery(id+"F0.wireOp",EDGE,"E27"),sQuery(id+"F0.wireOp",EDGE,"E42")])]});
            var Q72;
            Q72=makeQuery(id+"F5.opExtrude","SWEPT_BODY",BODY,{"disambiguationData":[OSD([sQuery(id+"F0.wireOp",EDGE,"E3"),sQuery(id+"F0.wireOp",EDGE,"E10"),sQuery(id+"F0.wireOp",EDGE,"E17")])]});
            var Q73;
            Q73=makeQuery(id+"F5.opExtrude","SWEPT_BODY",BODY,{"disambiguationData":[OSD([sQuery(id+"F0.wireOp",EDGE,"E3"),sQuery(id+"F0.wireOp",EDGE,"E25"),sQuery(id+"F0.wireOp",EDGE,"E34")])]});
            var Q74;
            Q74=makeQuery(id+"F5.opExtrude","SWEPT_BODY",BODY,{"disambiguationData":[OSD([sQuery(id+"F0.wireOp",EDGE,"E3"),sQuery(id+"F0.wireOp",EDGE,"E4"),sQuery(id+"F0.wireOp",EDGE,"E38")])]});
            var Q75;
            Q75=makeQuery(id+"F5.opExtrude","SWEPT_BODY",BODY,{"disambiguationData":[OSD([sQuery(id+"F0.wireOp",EDGE,"E3"),sQuery(id+"F0.wireOp",EDGE,"E22"),sQuery(id+"F0.wireOp",EDGE,"E40")])]});
            var Q76;
            Q76=makeQuery(id+"F5.opExtrude","SWEPT_BODY",BODY,{"disambiguationData":[OSD([sQuery(id+"F0.wireOp",EDGE,"E3"),sQuery(id+"F0.wireOp",EDGE,"E15"),sQuery(id+"F0.wireOp",EDGE,"E36")])]});
            var Q77;
            Q77=makeQuery(id+"F5.opExtrude","SWEPT_BODY",BODY,{"disambiguationData":[OSD([sQuery(id+"F0.wireOp",EDGE,"E3"),sQuery(id+"F0.wireOp",EDGE,"E24"),sQuery(id+"F0.wireOp",EDGE,"E32")])]});
            var Q78;
            Q78=makeQuery(id+"F5.opExtrude","SWEPT_BODY",BODY,{"disambiguationData":[OSD([sQuery(id+"F0.wireOp",EDGE,"E3"),sQuery(id+"F0.wireOp",EDGE,"E6"),sQuery(id+"F0.wireOp",EDGE,"E30")])]});
            var Q79;
            Q79=makeQuery(id+"F5.opExtrude","SWEPT_BODY",BODY,{"disambiguationData":[OSD([sQuery(id+"F0.wireOp",EDGE,"E3"),sQuery(id+"F0.wireOp",EDGE,"E7"),sQuery(id+"F0.wireOp",EDGE,"E30")])]});
            var Q80;
            Q80=makeQuery(id+"F5.opExtrude","SWEPT_BODY",BODY,{"disambiguationData":[OSD([sQuery(id+"F0.wireOp",EDGE,"E3"),sQuery(id+"F0.wireOp",EDGE,"E19"),sQuery(id+"F0.wireOp",EDGE,"E32")])]});
            var Q81;
            Q81=makeQuery(id+"F5.opExtrude","SWEPT_BODY",BODY,{"disambiguationData":[OSD([sQuery(id+"F0.wireOp",EDGE,"E3"),sQuery(id+"F0.wireOp",EDGE,"E12"),sQuery(id+"F0.wireOp",EDGE,"E36")])]});
            var Q82;
            Q82=makeQuery(id+"F5.opExtrude","SWEPT_BODY",BODY,{"disambiguationData":[OSD([sQuery(id+"F0.wireOp",EDGE,"E3"),sQuery(id+"F0.wireOp",EDGE,"E27"),sQuery(id+"F0.wireOp",EDGE,"E40")])]});
            var Q83;
            Q83=makeQuery(id+"F5.opExtrude","SWEPT_BODY",BODY,{"disambiguationData":[OSD([sQuery(id+"F0.wireOp",EDGE,"E3"),sQuery(id+"F0.wireOp",EDGE,"E5"),sQuery(id+"F0.wireOp",EDGE,"E38")])]});
            var Q84;
            Q84=makeQuery(id+"F5.opExtrude","SWEPT_BODY",BODY,{"disambiguationData":[OSD([sQuery(id+"F0.wireOp",EDGE,"E3"),sQuery(id+"F0.wireOp",EDGE,"E18"),sQuery(id+"F0.wireOp",EDGE,"E34")])]});
            var Q85;
            Q85=makeQuery(id+"F5.opExtrude","SWEPT_BODY",BODY,{"disambiguationData":[OSD([sQuery(id+"F0.wireOp",EDGE,"E3"),sQuery(id+"F0.wireOp",EDGE,"E11"),sQuery(id+"F0.wireOp",EDGE,"E26")])]});
            var Q86;
            Q86=makeQuery(id+"F5.opExtrude","SWEPT_BODY",BODY,{"disambiguationData":[OSD([sQuery(id+"F0.wireOp",EDGE,"E3"),sQuery(id+"F0.wireOp",EDGE,"E17"),sQuery(id+"F0.wireOp",EDGE,"E26")])]});
            var Q87;
            Q87=makeQuery(id+"F5.opExtrude","SWEPT_BODY",BODY,{"disambiguationData":[OSD([sQuery(id+"F0.wireOp",EDGE,"E4"),sQuery(id+"F0.wireOp",EDGE,"E17"),sQuery(id+"F0.wireOp",EDGE,"E34")])]});
            var Q88;
            Q88=makeQuery(id+"F5.opExtrude","SWEPT_BODY",BODY,{"disambiguationData":[OSD([sQuery(id+"F0.wireOp",EDGE,"E4"),sQuery(id+"F0.wireOp",EDGE,"E10"),sQuery(id+"F0.wireOp",EDGE,"E25")])]});
            var Q89;
            Q89=makeQuery(id+"F5.opExtrude","SWEPT_BODY",BODY,{"disambiguationData":[OSD([sQuery(id+"F0.wireOp",EDGE,"E4"),sQuery(id+"F0.wireOp",EDGE,"E22"),sQuery(id+"F0.wireOp",EDGE,"E25")])]});
            var Q90;
            Q90=makeQuery(id+"F5.opExtrude","SWEPT_BODY",BODY,{"disambiguationData":[OSD([sQuery(id+"F0.wireOp",EDGE,"E4"),sQuery(id+"F0.wireOp",EDGE,"E15"),sQuery(id+"F0.wireOp",EDGE,"E22")])]});
            var Q91;
            Q91=makeQuery(id+"F5.opExtrude","SWEPT_BODY",BODY,{"disambiguationData":[OSD([sQuery(id+"F0.wireOp",EDGE,"E4"),sQuery(id+"F0.wireOp",EDGE,"E24"),sQuery(id+"F0.wireOp",EDGE,"E34")])]});
            var Q92;
            Q92=makeQuery(id+"F5.opExtrude","SWEPT_BODY",BODY,{"disambiguationData":[OSD([sQuery(id+"F0.wireOp",EDGE,"E4"),sQuery(id+"F0.wireOp",EDGE,"E6"),sQuery(id+"F0.wireOp",EDGE,"E38")])]});
            var Q93;
            Q93=makeQuery(id+"F5.opExtrude","SWEPT_BODY",BODY,{"disambiguationData":[OSD([sQuery(id+"F0.wireOp",EDGE,"E4"),sQuery(id+"F0.wireOp",EDGE,"E21"),sQuery(id+"F0.wireOp",EDGE,"E40")])]});
            var Q94;
            Q94=makeQuery(id+"F5.opExtrude","SWEPT_BODY",BODY,{"disambiguationData":[OSD([sQuery(id+"F0.wireOp",EDGE,"E4"),sQuery(id+"F0.wireOp",EDGE,"E14"),sQuery(id+"F0.wireOp",EDGE,"E36")])]});
            var Q95;
            Q95=makeQuery(id+"F5.opExtrude","SWEPT_BODY",BODY,{"disambiguationData":[OSD([sQuery(id+"F0.wireOp",EDGE,"E4"),sQuery(id+"F0.wireOp",EDGE,"E29"),sQuery(id+"F0.wireOp",EDGE,"E32")])]});
            var Q96;
            Q96=makeQuery(id+"F5.opExtrude","SWEPT_BODY",BODY,{"disambiguationData":[OSD([sQuery(id+"F0.wireOp",EDGE,"E4"),sQuery(id+"F0.wireOp",EDGE,"E8"),sQuery(id+"F0.wireOp",EDGE,"E30")])]});
            var Q97;
            Q97=makeQuery(id+"F5.opExtrude","SWEPT_BODY",BODY,{"disambiguationData":[OSD([sQuery(id+"F0.wireOp",EDGE,"E4"),sQuery(id+"F0.wireOp",EDGE,"E5"),sQuery(id+"F0.wireOp",EDGE,"E30")])]});
            var Q98;
            Q98=makeQuery(id+"F5.opExtrude","SWEPT_BODY",BODY,{"disambiguationData":[OSD([sQuery(id+"F0.wireOp",EDGE,"E4"),sQuery(id+"F0.wireOp",EDGE,"E18"),sQuery(id+"F0.wireOp",EDGE,"E32")])]});
            var Q99;
            Q99=makeQuery(id+"F5.opExtrude","SWEPT_BODY",BODY,{"disambiguationData":[OSD([sQuery(id+"F0.wireOp",EDGE,"E4"),sQuery(id+"F0.wireOp",EDGE,"E11"),sQuery(id+"F0.wireOp",EDGE,"E36")])]});
            var Q100;
            Q100=makeQuery(id+"F5.opExtrude","SWEPT_BODY",BODY,{"disambiguationData":[OSD([sQuery(id+"F0.wireOp",EDGE,"E4"),sQuery(id+"F0.wireOp",EDGE,"E26"),sQuery(id+"F0.wireOp",EDGE,"E40")])]});
            var Q101;
            Q101=makeQuery(id+"F5.opExtrude","SWEPT_BODY",BODY,{"disambiguationData":[OSD([sQuery(id+"F0.wireOp",EDGE,"E5"),sQuery(id+"F0.wireOp",EDGE,"E17"),sQuery(id+"F0.wireOp",EDGE,"E40")])]});
            var Q102;
            Q102=makeQuery(id+"F5.opExtrude","SWEPT_BODY",BODY,{"disambiguationData":[OSD([sQuery(id+"F0.wireOp",EDGE,"E5"),sQuery(id+"F0.wireOp",EDGE,"E10"),sQuery(id+"F0.wireOp",EDGE,"E36")])]});
            var Q103;
            Q103=makeQuery(id+"F5.opExtrude","SWEPT_BODY",BODY,{"disambiguationData":[OSD([sQuery(id+"F0.wireOp",EDGE,"E5"),sQuery(id+"F0.wireOp",EDGE,"E25"),sQuery(id+"F0.wireOp",EDGE,"E32")])]});
            var Q104;
            Q104=makeQuery(id+"F5.opExtrude","SWEPT_BODY",BODY,{"disambiguationData":[OSD([sQuery(id+"F0.wireOp",EDGE,"E5"),sQuery(id+"F0.wireOp",EDGE,"E8"),sQuery(id+"F0.wireOp",EDGE,"E30")])]});
            var Q105;
            Q105=makeQuery(id+"F5.opExtrude","SWEPT_BODY",BODY,{"disambiguationData":[OSD([sQuery(id+"F0.wireOp",EDGE,"E5"),sQuery(id+"F0.wireOp",EDGE,"E20"),sQuery(id+"F0.wireOp",EDGE,"E32")])]});
            var Q106;
            Q106=makeQuery(id+"F5.opExtrude","SWEPT_BODY",BODY,{"disambiguationData":[OSD([sQuery(id+"F0.wireOp",EDGE,"E5"),sQuery(id+"F0.wireOp",EDGE,"E13"),sQuery(id+"F0.wireOp",EDGE,"E36")])]});
            var Q107;
            Q107=makeQuery(id+"F5.opExtrude","SWEPT_BODY",BODY,{"disambiguationData":[OSD([sQuery(id+"F0.wireOp",EDGE,"E5"),sQuery(id+"F0.wireOp",EDGE,"E28"),sQuery(id+"F0.wireOp",EDGE,"E40")])]});
            var Q108;
            Q108=makeQuery(id+"F5.opExtrude","SWEPT_BODY",BODY,{"disambiguationData":[OSD([sQuery(id+"F0.wireOp",EDGE,"E5"),sQuery(id+"F0.wireOp",EDGE,"E7"),sQuery(id+"F0.wireOp",EDGE,"E38")])]});
            var Q109;
            Q109=makeQuery(id+"F5.opExtrude","SWEPT_BODY",BODY,{"disambiguationData":[OSD([sQuery(id+"F0.wireOp",EDGE,"E5"),sQuery(id+"F0.wireOp",EDGE,"E19"),sQuery(id+"F0.wireOp",EDGE,"E34")])]});
            var Q110;
            Q110=makeQuery(id+"F5.opExtrude","SWEPT_BODY",BODY,{"disambiguationData":[OSD([sQuery(id+"F0.wireOp",EDGE,"E5"),sQuery(id+"F0.wireOp",EDGE,"E12"),sQuery(id+"F0.wireOp",EDGE,"E27")])]});
            var Q111;
            Q111=makeQuery(id+"F5.opExtrude","SWEPT_BODY",BODY,{"disambiguationData":[OSD([sQuery(id+"F0.wireOp",EDGE,"E5"),sQuery(id+"F0.wireOp",EDGE,"E18"),sQuery(id+"F0.wireOp",EDGE,"E27")])]});
            var Q112;
            Q112=makeQuery(id+"F5.opExtrude","SWEPT_BODY",BODY,{"disambiguationData":[OSD([sQuery(id+"F0.wireOp",EDGE,"E5"),sQuery(id+"F0.wireOp",EDGE,"E11"),sQuery(id+"F0.wireOp",EDGE,"E18")])]});
            var Q113;
            Q113=makeQuery(id+"F5.opExtrude","SWEPT_BODY",BODY,{"disambiguationData":[OSD([sQuery(id+"F0.wireOp",EDGE,"E5"),sQuery(id+"F0.wireOp",EDGE,"E26"),sQuery(id+"F0.wireOp",EDGE,"E34")])]});
            var Q114;
            Q114=makeQuery(id+"F5.opExtrude","SWEPT_BODY",BODY,{"disambiguationData":[OSD([sQuery(id+"F0.wireOp",EDGE,"E6"),sQuery(id+"F0.wireOp",EDGE,"E17"),sQuery(id+"F0.wireOp",EDGE,"E32")])]});
            var Q115;
            Q115=makeQuery(id+"F5.opExtrude","SWEPT_BODY",BODY,{"disambiguationData":[OSD([sQuery(id+"F0.wireOp",EDGE,"E6"),sQuery(id+"F0.wireOp",EDGE,"E10"),sQuery(id+"F0.wireOp",EDGE,"E36")])]});
            var Q116;
            Q116=makeQuery(id+"F5.opExtrude","SWEPT_BODY",BODY,{"disambiguationData":[OSD([sQuery(id+"F0.wireOp",EDGE,"E6"),sQuery(id+"F0.wireOp",EDGE,"E25"),sQuery(id+"F0.wireOp",EDGE,"E40")])]});
            var Q117;
            Q117=makeQuery(id+"F5.opExtrude","SWEPT_BODY",BODY,{"disambiguationData":[OSD([sQuery(id+"F0.wireOp",EDGE,"E6"),sQuery(id+"F0.wireOp",EDGE,"E22"),sQuery(id+"F0.wireOp",EDGE,"E34")])]});
            var Q118;
            Q118=makeQuery(id+"F5.opExtrude","SWEPT_BODY",BODY,{"disambiguationData":[OSD([sQuery(id+"F0.wireOp",EDGE,"E6"),sQuery(id+"F0.wireOp",EDGE,"E15"),sQuery(id+"F0.wireOp",EDGE,"E24")])]});
            var Q119;
            Q119=makeQuery(id+"F5.opExtrude","SWEPT_BODY",BODY,{"disambiguationData":[OSD([sQuery(id+"F0.wireOp",EDGE,"E6"),sQuery(id+"F0.wireOp",EDGE,"E21"),sQuery(id+"F0.wireOp",EDGE,"E24")])]});
            var Q120;
            Q120=makeQuery(id+"F5.opExtrude","SWEPT_BODY",BODY,{"disambiguationData":[OSD([sQuery(id+"F0.wireOp",EDGE,"E6"),sQuery(id+"F0.wireOp",EDGE,"E14"),sQuery(id+"F0.wireOp",EDGE,"E21")])]});
            var Q121;
            Q121=makeQuery(id+"F5.opExtrude","SWEPT_BODY",BODY,{"disambiguationData":[OSD([sQuery(id+"F0.wireOp",EDGE,"E6"),sQuery(id+"F0.wireOp",EDGE,"E29"),sQuery(id+"F0.wireOp",EDGE,"E34")])]});
            var Q122;
            Q122=makeQuery(id+"F5.opExtrude","SWEPT_BODY",BODY,{"disambiguationData":[OSD([sQuery(id+"F0.wireOp",EDGE,"E6"),sQuery(id+"F0.wireOp",EDGE,"E8"),sQuery(id+"F0.wireOp",EDGE,"E38")])]});
            var Q123;
            Q123=makeQuery(id+"F5.opExtrude","SWEPT_BODY",BODY,{"disambiguationData":[OSD([sQuery(id+"F0.wireOp",EDGE,"E6"),sQuery(id+"F0.wireOp",EDGE,"E20"),sQuery(id+"F0.wireOp",EDGE,"E40")])]});
            var Q124;
            Q124=makeQuery(id+"F5.opExtrude","SWEPT_BODY",BODY,{"disambiguationData":[OSD([sQuery(id+"F0.wireOp",EDGE,"E6"),sQuery(id+"F0.wireOp",EDGE,"E13"),sQuery(id+"F0.wireOp",EDGE,"E36")])]});
            var Q125;
            Q125=makeQuery(id+"F5.opExtrude","SWEPT_BODY",BODY,{"disambiguationData":[OSD([sQuery(id+"F0.wireOp",EDGE,"E6"),sQuery(id+"F0.wireOp",EDGE,"E28"),sQuery(id+"F0.wireOp",EDGE,"E32")])]});
            var Q126;
            Q126=makeQuery(id+"F5.opExtrude","SWEPT_BODY",BODY,{"disambiguationData":[OSD([sQuery(id+"F0.wireOp",EDGE,"E6"),sQuery(id+"F0.wireOp",EDGE,"E7"),sQuery(id+"F0.wireOp",EDGE,"E30")])]});
            var Q127;
            Q127=makeQuery(id+"F5.opExtrude","SWEPT_BODY",BODY,{"disambiguationData":[OSD([sQuery(id+"F0.wireOp",EDGE,"E7"),sQuery(id+"F0.wireOp",EDGE,"E21"),sQuery(id+"F0.wireOp",EDGE,"E32")])]});
            var Q128;
            Q128=makeQuery(id+"F5.opExtrude","SWEPT_BODY",BODY,{"disambiguationData":[OSD([sQuery(id+"F0.wireOp",EDGE,"E7"),sQuery(id+"F0.wireOp",EDGE,"E14"),sQuery(id+"F0.wireOp",EDGE,"E36")])]});
            var Q129;
            Q129=makeQuery(id+"F5.opExtrude","SWEPT_BODY",BODY,{"disambiguationData":[OSD([sQuery(id+"F0.wireOp",EDGE,"E7"),sQuery(id+"F0.wireOp",EDGE,"E29"),sQuery(id+"F0.wireOp",EDGE,"E40")])]});
            var Q130;
            Q130=makeQuery(id+"F5.opExtrude","SWEPT_BODY",BODY,{"disambiguationData":[OSD([sQuery(id+"F0.wireOp",EDGE,"E7"),sQuery(id+"F0.wireOp",EDGE,"E8"),sQuery(id+"F0.wireOp",EDGE,"E38")])]});
            var Q131;
            Q131=makeQuery(id+"F5.opExtrude","SWEPT_BODY",BODY,{"disambiguationData":[OSD([sQuery(id+"F0.wireOp",EDGE,"E7"),sQuery(id+"F0.wireOp",EDGE,"E20"),sQuery(id+"F0.wireOp",EDGE,"E34")])]});
            var Q132;
            Q132=makeQuery(id+"F5.opExtrude","SWEPT_BODY",BODY,{"disambiguationData":[OSD([sQuery(id+"F0.wireOp",EDGE,"E7"),sQuery(id+"F0.wireOp",EDGE,"E13"),sQuery(id+"F0.wireOp",EDGE,"E28")])]});
            var Q133;
            Q133=makeQuery(id+"F5.opExtrude","SWEPT_BODY",BODY,{"disambiguationData":[OSD([sQuery(id+"F0.wireOp",EDGE,"E7"),sQuery(id+"F0.wireOp",EDGE,"E19"),sQuery(id+"F0.wireOp",EDGE,"E28")])]});
            var Q134;
            Q134=makeQuery(id+"F5.opExtrude","SWEPT_BODY",BODY,{"disambiguationData":[OSD([sQuery(id+"F0.wireOp",EDGE,"E7"),sQuery(id+"F0.wireOp",EDGE,"E12"),sQuery(id+"F0.wireOp",EDGE,"E19")])]});
            var Q135;
            Q135=makeQuery(id+"F5.opExtrude","SWEPT_BODY",BODY,{"disambiguationData":[OSD([sQuery(id+"F0.wireOp",EDGE,"E7"),sQuery(id+"F0.wireOp",EDGE,"E27"),sQuery(id+"F0.wireOp",EDGE,"E34")])]});
            var Q136;
            Q136=makeQuery(id+"F5.opExtrude","SWEPT_BODY",BODY,{"disambiguationData":[OSD([sQuery(id+"F0.wireOp",EDGE,"E7"),sQuery(id+"F0.wireOp",EDGE,"E18"),sQuery(id+"F0.wireOp",EDGE,"E40")])]});
            var Q137;
            Q137=makeQuery(id+"F5.opExtrude","SWEPT_BODY",BODY,{"disambiguationData":[OSD([sQuery(id+"F0.wireOp",EDGE,"E7"),sQuery(id+"F0.wireOp",EDGE,"E11"),sQuery(id+"F0.wireOp",EDGE,"E36")])]});
            var Q138;
            Q138=makeQuery(id+"F5.opExtrude","SWEPT_BODY",BODY,{"disambiguationData":[OSD([sQuery(id+"F0.wireOp",EDGE,"E7"),sQuery(id+"F0.wireOp",EDGE,"E26"),sQuery(id+"F0.wireOp",EDGE,"E32")])]});
            var Q139;
            Q139=makeQuery(id+"F5.opExtrude","SWEPT_BODY",BODY,{"disambiguationData":[OSD([sQuery(id+"F0.wireOp",EDGE,"E8"),sQuery(id+"F0.wireOp",EDGE,"E22"),sQuery(id+"F0.wireOp",EDGE,"E32")])]});
            var Q140;
            Q140=makeQuery(id+"F5.opExtrude","SWEPT_BODY",BODY,{"disambiguationData":[OSD([sQuery(id+"F0.wireOp",EDGE,"E8"),sQuery(id+"F0.wireOp",EDGE,"E15"),sQuery(id+"F0.wireOp",EDGE,"E36")])]});
            var Q141;
            Q141=makeQuery(id+"F5.opExtrude","SWEPT_BODY",BODY,{"disambiguationData":[OSD([sQuery(id+"F0.wireOp",EDGE,"E8"),sQuery(id+"F0.wireOp",EDGE,"E24"),sQuery(id+"F0.wireOp",EDGE,"E40")])]});
            var Q142;
            Q142=makeQuery(id+"F5.opExtrude","SWEPT_BODY",BODY,{"disambiguationData":[OSD([sQuery(id+"F0.wireOp",EDGE,"E8"),sQuery(id+"F0.wireOp",EDGE,"E21"),sQuery(id+"F0.wireOp",EDGE,"E34")])]});
            var Q143;
            Q143=makeQuery(id+"F5.opExtrude","SWEPT_BODY",BODY,{"disambiguationData":[OSD([sQuery(id+"F0.wireOp",EDGE,"E8"),sQuery(id+"F0.wireOp",EDGE,"E14"),sQuery(id+"F0.wireOp",EDGE,"E29")])]});
            var Q144;
            Q144=makeQuery(id+"F5.opExtrude","SWEPT_BODY",BODY,{"disambiguationData":[OSD([sQuery(id+"F0.wireOp",EDGE,"E8"),sQuery(id+"F0.wireOp",EDGE,"E20"),sQuery(id+"F0.wireOp",EDGE,"E29")])]});
            var Q145;
            Q145=makeQuery(id+"F5.opExtrude","SWEPT_BODY",BODY,{"disambiguationData":[OSD([sQuery(id+"F0.wireOp",EDGE,"E8"),sQuery(id+"F0.wireOp",EDGE,"E13"),sQuery(id+"F0.wireOp",EDGE,"E20")])]});
            var Q146;
            Q146=makeQuery(id+"F5.opExtrude","SWEPT_BODY",BODY,{"disambiguationData":[OSD([sQuery(id+"F0.wireOp",EDGE,"E8"),sQuery(id+"F0.wireOp",EDGE,"E28"),sQuery(id+"F0.wireOp",EDGE,"E34")])]});
            var Q147;
            Q147=makeQuery(id+"F5.opExtrude","SWEPT_BODY",BODY,{"disambiguationData":[OSD([sQuery(id+"F0.wireOp",EDGE,"E8"),sQuery(id+"F0.wireOp",EDGE,"E19"),sQuery(id+"F0.wireOp",EDGE,"E40")])]});
            var Q148;
            Q148=makeQuery(id+"F5.opExtrude","SWEPT_BODY",BODY,{"disambiguationData":[OSD([sQuery(id+"F0.wireOp",EDGE,"E8"),sQuery(id+"F0.wireOp",EDGE,"E12"),sQuery(id+"F0.wireOp",EDGE,"E36")])]});
            var Q149;
            Q149=makeQuery(id+"F5.opExtrude","SWEPT_BODY",BODY,{"disambiguationData":[OSD([sQuery(id+"F0.wireOp",EDGE,"E8"),sQuery(id+"F0.wireOp",EDGE,"E27"),sQuery(id+"F0.wireOp",EDGE,"E32")])]});
            var Q150;
            Q150=makeQuery(id+"F5.opExtrude","SWEPT_BODY",BODY,{"disambiguationData":[OSD([sQuery(id+"F0.wireOp",EDGE,"E10"),sQuery(id+"F0.wireOp",EDGE,"E17"),sQuery(id+"F0.wireOp",EDGE,"E25")])]});
            var Q151;
            Q151=makeQuery(id+"F5.opExtrude","SWEPT_BODY",BODY,{"disambiguationData":[OSD([sQuery(id+"F0.wireOp",EDGE,"E10"),sQuery(id+"F0.wireOp",EDGE,"E22"),sQuery(id+"F0.wireOp",EDGE,"E34")])]});
            var Q152;
            Q152=makeQuery(id+"F5.opExtrude","SWEPT_BODY",BODY,{"disambiguationData":[OSD([sQuery(id+"F0.wireOp",EDGE,"E10"),sQuery(id+"F0.wireOp",EDGE,"E15"),sQuery(id+"F0.wireOp",EDGE,"E38")])]});
            var Q153;
            Q153=makeQuery(id+"F5.opExtrude","SWEPT_BODY",BODY,{"disambiguationData":[OSD([sQuery(id+"F0.wireOp",EDGE,"E10"),sQuery(id+"F0.wireOp",EDGE,"E24"),sQuery(id+"F0.wireOp",EDGE,"E40")])]});
            var Q154;
            Q154=makeQuery(id+"F5.opExtrude","SWEPT_BODY",BODY,{"disambiguationData":[OSD([sQuery(id+"F0.wireOp",EDGE,"E10"),sQuery(id+"F0.wireOp",EDGE,"E21"),sQuery(id+"F0.wireOp",EDGE,"E32")])]});
            var Q155;
            Q155=makeQuery(id+"F5.opExtrude","SWEPT_BODY",BODY,{"disambiguationData":[OSD([sQuery(id+"F0.wireOp",EDGE,"E10"),sQuery(id+"F0.wireOp",EDGE,"E14"),sQuery(id+"F0.wireOp",EDGE,"E30")])]});
            var Q156;
            Q156=makeQuery(id+"F5.opExtrude","SWEPT_BODY",BODY,{"disambiguationData":[OSD([sQuery(id+"F0.wireOp",EDGE,"E10"),sQuery(id+"F0.wireOp",EDGE,"E12"),sQuery(id+"F0.wireOp",EDGE,"E30")])]});
            var Q157;
            Q157=makeQuery(id+"F5.opExtrude","SWEPT_BODY",BODY,{"disambiguationData":[OSD([sQuery(id+"F0.wireOp",EDGE,"E10"),sQuery(id+"F0.wireOp",EDGE,"E27"),sQuery(id+"F0.wireOp",EDGE,"E32")])]});
            var Q158;
            Q158=makeQuery(id+"F5.opExtrude","SWEPT_BODY",BODY,{"disambiguationData":[OSD([sQuery(id+"F0.wireOp",EDGE,"E10"),sQuery(id+"F0.wireOp",EDGE,"E18"),sQuery(id+"F0.wireOp",EDGE,"E40")])]});
            var Q159;
            Q159=makeQuery(id+"F5.opExtrude","SWEPT_BODY",BODY,{"disambiguationData":[OSD([sQuery(id+"F0.wireOp",EDGE,"E10"),sQuery(id+"F0.wireOp",EDGE,"E11"),sQuery(id+"F0.wireOp",EDGE,"E38")])]});
            var Q160;
            Q160=makeQuery(id+"F5.opExtrude","SWEPT_BODY",BODY,{"disambiguationData":[OSD([sQuery(id+"F0.wireOp",EDGE,"E10"),sQuery(id+"F0.wireOp",EDGE,"E26"),sQuery(id+"F0.wireOp",EDGE,"E34")])]});
            var Q161;
            Q161=makeQuery(id+"F5.opExtrude","SWEPT_BODY",BODY,{"disambiguationData":[OSD([sQuery(id+"F0.wireOp",EDGE,"E11"),sQuery(id+"F0.wireOp",EDGE,"E17"),sQuery(id+"F0.wireOp",EDGE,"E34")])]});
            var Q162;
            Q162=makeQuery(id+"F5.opExtrude","SWEPT_BODY",BODY,{"disambiguationData":[OSD([sQuery(id+"F0.wireOp",EDGE,"E11"),sQuery(id+"F0.wireOp",EDGE,"E25"),sQuery(id+"F0.wireOp",EDGE,"E40")])]});
            var Q163;
            Q163=makeQuery(id+"F5.opExtrude","SWEPT_BODY",BODY,{"disambiguationData":[OSD([sQuery(id+"F0.wireOp",EDGE,"E11"),sQuery(id+"F0.wireOp",EDGE,"E22"),sQuery(id+"F0.wireOp",EDGE,"E32")])]});
            var Q164;
            Q164=makeQuery(id+"F5.opExtrude","SWEPT_BODY",BODY,{"disambiguationData":[OSD([sQuery(id+"F0.wireOp",EDGE,"E11"),sQuery(id+"F0.wireOp",EDGE,"E15"),sQuery(id+"F0.wireOp",EDGE,"E30")])]});
            var Q165;
            Q165=makeQuery(id+"F5.opExtrude","SWEPT_BODY",BODY,{"disambiguationData":[OSD([sQuery(id+"F0.wireOp",EDGE,"E11"),sQuery(id+"F0.wireOp",EDGE,"E13"),sQuery(id+"F0.wireOp",EDGE,"E30")])]});
            var Q166;
            Q166=makeQuery(id+"F5.opExtrude","SWEPT_BODY",BODY,{"disambiguationData":[OSD([sQuery(id+"F0.wireOp",EDGE,"E11"),sQuery(id+"F0.wireOp",EDGE,"E28"),sQuery(id+"F0.wireOp",EDGE,"E32")])]});
            var Q167;
            Q167=makeQuery(id+"F5.opExtrude","SWEPT_BODY",BODY,{"disambiguationData":[OSD([sQuery(id+"F0.wireOp",EDGE,"E11"),sQuery(id+"F0.wireOp",EDGE,"E19"),sQuery(id+"F0.wireOp",EDGE,"E40")])]});
            var Q168;
            Q168=makeQuery(id+"F5.opExtrude","SWEPT_BODY",BODY,{"disambiguationData":[OSD([sQuery(id+"F0.wireOp",EDGE,"E11"),sQuery(id+"F0.wireOp",EDGE,"E12"),sQuery(id+"F0.wireOp",EDGE,"E38")])]});
            var Q169;
            Q169=makeQuery(id+"F5.opExtrude","SWEPT_BODY",BODY,{"disambiguationData":[OSD([sQuery(id+"F0.wireOp",EDGE,"E11"),sQuery(id+"F0.wireOp",EDGE,"E27"),sQuery(id+"F0.wireOp",EDGE,"E34")])]});
            var Q170;
            Q170=makeQuery(id+"F5.opExtrude","SWEPT_BODY",BODY,{"disambiguationData":[OSD([sQuery(id+"F0.wireOp",EDGE,"E11"),sQuery(id+"F0.wireOp",EDGE,"E18"),sQuery(id+"F0.wireOp",EDGE,"E26")])]});
            var Q171;
            Q171=makeQuery(id+"F5.opExtrude","SWEPT_BODY",BODY,{"disambiguationData":[OSD([sQuery(id+"F0.wireOp",EDGE,"E12"),sQuery(id+"F0.wireOp",EDGE,"E17"),sQuery(id+"F0.wireOp",EDGE,"E32")])]});
            var Q172;
            Q172=makeQuery(id+"F5.opExtrude","SWEPT_BODY",BODY,{"disambiguationData":[OSD([sQuery(id+"F0.wireOp",EDGE,"E12"),sQuery(id+"F0.wireOp",EDGE,"E14"),sQuery(id+"F0.wireOp",EDGE,"E30")])]});
            var Q173;
            Q173=makeQuery(id+"F5.opExtrude","SWEPT_BODY",BODY,{"disambiguationData":[OSD([sQuery(id+"F0.wireOp",EDGE,"E12"),sQuery(id+"F0.wireOp",EDGE,"E29"),sQuery(id+"F0.wireOp",EDGE,"E32")])]});
            var Q174;
            Q174=makeQuery(id+"F5.opExtrude","SWEPT_BODY",BODY,{"disambiguationData":[OSD([sQuery(id+"F0.wireOp",EDGE,"E12"),sQuery(id+"F0.wireOp",EDGE,"E20"),sQuery(id+"F0.wireOp",EDGE,"E40")])]});
            var Q175;
            Q175=makeQuery(id+"F5.opExtrude","SWEPT_BODY",BODY,{"disambiguationData":[OSD([sQuery(id+"F0.wireOp",EDGE,"E12"),sQuery(id+"F0.wireOp",EDGE,"E13"),sQuery(id+"F0.wireOp",EDGE,"E38")])]});
            var Q176;
            Q176=makeQuery(id+"F5.opExtrude","SWEPT_BODY",BODY,{"disambiguationData":[OSD([sQuery(id+"F0.wireOp",EDGE,"E12"),sQuery(id+"F0.wireOp",EDGE,"E28"),sQuery(id+"F0.wireOp",EDGE,"E34")])]});
            var Q177;
            Q177=makeQuery(id+"F5.opExtrude","SWEPT_BODY",BODY,{"disambiguationData":[OSD([sQuery(id+"F0.wireOp",EDGE,"E12"),sQuery(id+"F0.wireOp",EDGE,"E19"),sQuery(id+"F0.wireOp",EDGE,"E27")])]});
            var Q178;
            Q178=makeQuery(id+"F5.opExtrude","SWEPT_BODY",BODY,{"disambiguationData":[OSD([sQuery(id+"F0.wireOp",EDGE,"E12"),sQuery(id+"F0.wireOp",EDGE,"E18"),sQuery(id+"F0.wireOp",EDGE,"E34")])]});
            var Q179;
            Q179=makeQuery(id+"F5.opExtrude","SWEPT_BODY",BODY,{"disambiguationData":[OSD([sQuery(id+"F0.wireOp",EDGE,"E12"),sQuery(id+"F0.wireOp",EDGE,"E26"),sQuery(id+"F0.wireOp",EDGE,"E40")])]});
            var Q180;
            Q180=makeQuery(id+"F5.opExtrude","SWEPT_BODY",BODY,{"disambiguationData":[OSD([sQuery(id+"F0.wireOp",EDGE,"E13"),sQuery(id+"F0.wireOp",EDGE,"E15"),sQuery(id+"F0.wireOp",EDGE,"E30")])]});
            var Q181;
            Q181=makeQuery(id+"F5.opExtrude","SWEPT_BODY",BODY,{"disambiguationData":[OSD([sQuery(id+"F0.wireOp",EDGE,"E13"),sQuery(id+"F0.wireOp",EDGE,"E24"),sQuery(id+"F0.wireOp",EDGE,"E32")])]});
            var Q182;
            Q182=makeQuery(id+"F5.opExtrude","SWEPT_BODY",BODY,{"disambiguationData":[OSD([sQuery(id+"F0.wireOp",EDGE,"E13"),sQuery(id+"F0.wireOp",EDGE,"E21"),sQuery(id+"F0.wireOp",EDGE,"E40")])]});
            var Q183;
            Q183=makeQuery(id+"F5.opExtrude","SWEPT_BODY",BODY,{"disambiguationData":[OSD([sQuery(id+"F0.wireOp",EDGE,"E13"),sQuery(id+"F0.wireOp",EDGE,"E14"),sQuery(id+"F0.wireOp",EDGE,"E38")])]});
            var Q184;
            Q184=makeQuery(id+"F5.opExtrude","SWEPT_BODY",BODY,{"disambiguationData":[OSD([sQuery(id+"F0.wireOp",EDGE,"E13"),sQuery(id+"F0.wireOp",EDGE,"E29"),sQuery(id+"F0.wireOp",EDGE,"E34")])]});
            var Q185;
            Q185=makeQuery(id+"F5.opExtrude","SWEPT_BODY",BODY,{"disambiguationData":[OSD([sQuery(id+"F0.wireOp",EDGE,"E13"),sQuery(id+"F0.wireOp",EDGE,"E20"),sQuery(id+"F0.wireOp",EDGE,"E28")])]});
            var Q186;
            Q186=makeQuery(id+"F5.opExtrude","SWEPT_BODY",BODY,{"disambiguationData":[OSD([sQuery(id+"F0.wireOp",EDGE,"E13"),sQuery(id+"F0.wireOp",EDGE,"E19"),sQuery(id+"F0.wireOp",EDGE,"E34")])]});
            var Q187;
            Q187=makeQuery(id+"F5.opExtrude","SWEPT_BODY",BODY,{"disambiguationData":[OSD([sQuery(id+"F0.wireOp",EDGE,"E13"),sQuery(id+"F0.wireOp",EDGE,"E27"),sQuery(id+"F0.wireOp",EDGE,"E40")])]});
            var Q188;
            Q188=makeQuery(id+"F5.opExtrude","SWEPT_BODY",BODY,{"disambiguationData":[OSD([sQuery(id+"F0.wireOp",EDGE,"E13"),sQuery(id+"F0.wireOp",EDGE,"E18"),sQuery(id+"F0.wireOp",EDGE,"E32")])]});
            var Q189;
            Q189=makeQuery(id+"F5.opExtrude","SWEPT_BODY",BODY,{"disambiguationData":[OSD([sQuery(id+"F0.wireOp",EDGE,"E14"),sQuery(id+"F0.wireOp",EDGE,"E25"),sQuery(id+"F0.wireOp",EDGE,"E32")])]});
            var Q190;
            Q190=makeQuery(id+"F5.opExtrude","SWEPT_BODY",BODY,{"disambiguationData":[OSD([sQuery(id+"F0.wireOp",EDGE,"E14"),sQuery(id+"F0.wireOp",EDGE,"E22"),sQuery(id+"F0.wireOp",EDGE,"E40")])]});
            var Q191;
            Q191=makeQuery(id+"F5.opExtrude","SWEPT_BODY",BODY,{"disambiguationData":[OSD([sQuery(id+"F0.wireOp",EDGE,"E14"),sQuery(id+"F0.wireOp",EDGE,"E15"),sQuery(id+"F0.wireOp",EDGE,"E38")])]});
            var Q192;
            Q192=makeQuery(id+"F5.opExtrude","SWEPT_BODY",BODY,{"disambiguationData":[OSD([sQuery(id+"F0.wireOp",EDGE,"E14"),sQuery(id+"F0.wireOp",EDGE,"E24"),sQuery(id+"F0.wireOp",EDGE,"E34")])]});
            var Q193;
            Q193=makeQuery(id+"F5.opExtrude","SWEPT_BODY",BODY,{"disambiguationData":[OSD([sQuery(id+"F0.wireOp",EDGE,"E14"),sQuery(id+"F0.wireOp",EDGE,"E21"),sQuery(id+"F0.wireOp",EDGE,"E29")])]});
            var Q194;
            Q194=makeQuery(id+"F5.opExtrude","SWEPT_BODY",BODY,{"disambiguationData":[OSD([sQuery(id+"F0.wireOp",EDGE,"E14"),sQuery(id+"F0.wireOp",EDGE,"E20"),sQuery(id+"F0.wireOp",EDGE,"E34")])]});
            var Q195;
            Q195=makeQuery(id+"F5.opExtrude","SWEPT_BODY",BODY,{"disambiguationData":[OSD([sQuery(id+"F0.wireOp",EDGE,"E14"),sQuery(id+"F0.wireOp",EDGE,"E28"),sQuery(id+"F0.wireOp",EDGE,"E40")])]});
            var Q196;
            Q196=makeQuery(id+"F5.opExtrude","SWEPT_BODY",BODY,{"disambiguationData":[OSD([sQuery(id+"F0.wireOp",EDGE,"E14"),sQuery(id+"F0.wireOp",EDGE,"E19"),sQuery(id+"F0.wireOp",EDGE,"E32")])]});
            var Q197;
            Q197=makeQuery(id+"F5.opExtrude","SWEPT_BODY",BODY,{"disambiguationData":[OSD([sQuery(id+"F0.wireOp",EDGE,"E15"),sQuery(id+"F0.wireOp",EDGE,"E17"),sQuery(id+"F0.wireOp",EDGE,"E40")])]});
            var Q198;
            Q198=makeQuery(id+"F5.opExtrude","SWEPT_BODY",BODY,{"disambiguationData":[OSD([sQuery(id+"F0.wireOp",EDGE,"E15"),sQuery(id+"F0.wireOp",EDGE,"E25"),sQuery(id+"F0.wireOp",EDGE,"E34")])]});
            var Q199;
            Q199=makeQuery(id+"F5.opExtrude","SWEPT_BODY",BODY,{"disambiguationData":[OSD([sQuery(id+"F0.wireOp",EDGE,"E15"),sQuery(id+"F0.wireOp",EDGE,"E22"),sQuery(id+"F0.wireOp",EDGE,"E24")])]});
            var Q200;
            Q200=makeQuery(id+"F5.opExtrude","SWEPT_BODY",BODY,{"disambiguationData":[OSD([sQuery(id+"F0.wireOp",EDGE,"E15"),sQuery(id+"F0.wireOp",EDGE,"E21"),sQuery(id+"F0.wireOp",EDGE,"E34")])]});
            var Q201;
            Q201=makeQuery(id+"F5.opExtrude","SWEPT_BODY",BODY,{"disambiguationData":[OSD([sQuery(id+"F0.wireOp",EDGE,"E15"),sQuery(id+"F0.wireOp",EDGE,"E29"),sQuery(id+"F0.wireOp",EDGE,"E40")])]});
            var Q202;
            Q202=makeQuery(id+"F5.opExtrude","SWEPT_BODY",BODY,{"disambiguationData":[OSD([sQuery(id+"F0.wireOp",EDGE,"E15"),sQuery(id+"F0.wireOp",EDGE,"E20"),sQuery(id+"F0.wireOp",EDGE,"E32")])]});
            var Q203;
            Q203=makeQuery(id+"F5.opExtrude","SWEPT_BODY",BODY,{"disambiguationData":[OSD([sQuery(id+"F0.wireOp",EDGE,"E15"),sQuery(id+"F0.wireOp",EDGE,"E26"),sQuery(id+"F0.wireOp",EDGE,"E32")])]});
            var Q204;
            Q204=makeQuery(id+"F5.opExtrude","SWEPT_BODY",BODY,{"disambiguationData":[OSD([sQuery(id+"F0.wireOp",EDGE,"E17"),sQuery(id+"F0.wireOp",EDGE,"E22"),sQuery(id+"F0.wireOp",EDGE,"E38")])]});
            var Q205;
            Q205=makeQuery(id+"F5.opExtrude","SWEPT_BODY",BODY,{"disambiguationData":[OSD([sQuery(id+"F0.wireOp",EDGE,"E17"),sQuery(id+"F0.wireOp",EDGE,"E24"),sQuery(id+"F0.wireOp",EDGE,"E36")])]});
            var Q206;
            Q206=makeQuery(id+"F5.opExtrude","SWEPT_BODY",BODY,{"disambiguationData":[OSD([sQuery(id+"F0.wireOp",EDGE,"E17"),sQuery(id+"F0.wireOp",EDGE,"E21"),sQuery(id+"F0.wireOp",EDGE,"E30")])]});
            var Q207;
            Q207=makeQuery(id+"F5.opExtrude","SWEPT_BODY",BODY,{"disambiguationData":[OSD([sQuery(id+"F0.wireOp",EDGE,"E17"),sQuery(id+"F0.wireOp",EDGE,"E19"),sQuery(id+"F0.wireOp",EDGE,"E30")])]});
            var Q208;
            Q208=makeQuery(id+"F5.opExtrude","SWEPT_BODY",BODY,{"disambiguationData":[OSD([sQuery(id+"F0.wireOp",EDGE,"E17"),sQuery(id+"F0.wireOp",EDGE,"E27"),sQuery(id+"F0.wireOp",EDGE,"E36")])]});
            var Q209;
            Q209=makeQuery(id+"F5.opExtrude","SWEPT_BODY",BODY,{"disambiguationData":[OSD([sQuery(id+"F0.wireOp",EDGE,"E17"),sQuery(id+"F0.wireOp",EDGE,"E18"),sQuery(id+"F0.wireOp",EDGE,"E38")])]});
            var Q210;
            Q210=makeQuery(id+"F5.opExtrude","SWEPT_BODY",BODY,{"disambiguationData":[OSD([sQuery(id+"F0.wireOp",EDGE,"E18"),sQuery(id+"F0.wireOp",EDGE,"E25"),sQuery(id+"F0.wireOp",EDGE,"E36")])]});
            var Q211;
            Q211=makeQuery(id+"F5.opExtrude","SWEPT_BODY",BODY,{"disambiguationData":[OSD([sQuery(id+"F0.wireOp",EDGE,"E18"),sQuery(id+"F0.wireOp",EDGE,"E22"),sQuery(id+"F0.wireOp",EDGE,"E30")])]});
            var Q212;
            Q212=makeQuery(id+"F5.opExtrude","SWEPT_BODY",BODY,{"disambiguationData":[OSD([sQuery(id+"F0.wireOp",EDGE,"E18"),sQuery(id+"F0.wireOp",EDGE,"E20"),sQuery(id+"F0.wireOp",EDGE,"E30")])]});
            var Q213;
            Q213=makeQuery(id+"F5.opExtrude","SWEPT_BODY",BODY,{"disambiguationData":[OSD([sQuery(id+"F0.wireOp",EDGE,"E18"),sQuery(id+"F0.wireOp",EDGE,"E28"),sQuery(id+"F0.wireOp",EDGE,"E36")])]});
            var Q214;
            Q214=makeQuery(id+"F5.opExtrude","SWEPT_BODY",BODY,{"disambiguationData":[OSD([sQuery(id+"F0.wireOp",EDGE,"E18"),sQuery(id+"F0.wireOp",EDGE,"E19"),sQuery(id+"F0.wireOp",EDGE,"E38")])]});
            var Q215;
            Q215=makeQuery(id+"F5.opExtrude","SWEPT_BODY",BODY,{"disambiguationData":[OSD([sQuery(id+"F0.wireOp",EDGE,"E19"),sQuery(id+"F0.wireOp",EDGE,"E21"),sQuery(id+"F0.wireOp",EDGE,"E30")])]});
            var Q216;
            Q216=makeQuery(id+"F5.opExtrude","SWEPT_BODY",BODY,{"disambiguationData":[OSD([sQuery(id+"F0.wireOp",EDGE,"E19"),sQuery(id+"F0.wireOp",EDGE,"E29"),sQuery(id+"F0.wireOp",EDGE,"E36")])]});
            var Q217;
            Q217=makeQuery(id+"F5.opExtrude","SWEPT_BODY",BODY,{"disambiguationData":[OSD([sQuery(id+"F0.wireOp",EDGE,"E19"),sQuery(id+"F0.wireOp",EDGE,"E20"),sQuery(id+"F0.wireOp",EDGE,"E38")])]});
            var Q218;
            Q218=makeQuery(id+"F5.opExtrude","SWEPT_BODY",BODY,{"disambiguationData":[OSD([sQuery(id+"F0.wireOp",EDGE,"E19"),sQuery(id+"F0.wireOp",EDGE,"E26"),sQuery(id+"F0.wireOp",EDGE,"E36")])]});
            var Q219;
            Q219=makeQuery(id+"F5.opExtrude","SWEPT_BODY",BODY,{"disambiguationData":[OSD([sQuery(id+"F0.wireOp",EDGE,"E20"),sQuery(id+"F0.wireOp",EDGE,"E22"),sQuery(id+"F0.wireOp",EDGE,"E30")])]});
            var Q220;
            Q220=makeQuery(id+"F5.opExtrude","SWEPT_BODY",BODY,{"disambiguationData":[OSD([sQuery(id+"F0.wireOp",EDGE,"E20"),sQuery(id+"F0.wireOp",EDGE,"E24"),sQuery(id+"F0.wireOp",EDGE,"E36")])]});
            var Q221;
            Q221=makeQuery(id+"F5.opExtrude","SWEPT_BODY",BODY,{"disambiguationData":[OSD([sQuery(id+"F0.wireOp",EDGE,"E20"),sQuery(id+"F0.wireOp",EDGE,"E21"),sQuery(id+"F0.wireOp",EDGE,"E38")])]});
            var Q222;
            Q222=makeQuery(id+"F5.opExtrude","SWEPT_BODY",BODY,{"disambiguationData":[OSD([sQuery(id+"F0.wireOp",EDGE,"E20"),sQuery(id+"F0.wireOp",EDGE,"E27"),sQuery(id+"F0.wireOp",EDGE,"E36")])]});
            var Q223;
            Q223=makeQuery(id+"F5.opExtrude","SWEPT_BODY",BODY,{"disambiguationData":[OSD([sQuery(id+"F0.wireOp",EDGE,"E21"),sQuery(id+"F0.wireOp",EDGE,"E25"),sQuery(id+"F0.wireOp",EDGE,"E36")])]});
            var Q224;
            Q224=makeQuery(id+"F5.opExtrude","SWEPT_BODY",BODY,{"disambiguationData":[OSD([sQuery(id+"F0.wireOp",EDGE,"E21"),sQuery(id+"F0.wireOp",EDGE,"E22"),sQuery(id+"F0.wireOp",EDGE,"E38")])]});
            var Q225;
            Q225=makeQuery(id+"F5.opExtrude","SWEPT_BODY",BODY,{"disambiguationData":[OSD([sQuery(id+"F0.wireOp",EDGE,"E21"),sQuery(id+"F0.wireOp",EDGE,"E28"),sQuery(id+"F0.wireOp",EDGE,"E36")])]});
            var Q226;
            Q226=makeQuery(id+"F5.opExtrude","SWEPT_BODY",BODY,{"disambiguationData":[OSD([sQuery(id+"F0.wireOp",EDGE,"E22"),sQuery(id+"F0.wireOp",EDGE,"E29"),sQuery(id+"F0.wireOp",EDGE,"E36")])]});
            var Q227;
            Q227=makeQuery(id+"F5.opExtrude","SWEPT_BODY",BODY,{"disambiguationData":[OSD([sQuery(id+"F0.wireOp",EDGE,"E22"),sQuery(id+"F0.wireOp",EDGE,"E26"),sQuery(id+"F0.wireOp",EDGE,"E36")])]});
            var Q228;
            Q228=makeQuery(id+"F5.opExtrude","SWEPT_BODY",BODY,{"disambiguationData":[OSD([sQuery(id+"F0.wireOp",EDGE,"E24"),sQuery(id+"F0.wireOp",EDGE,"E25"),sQuery(id+"F0.wireOp",EDGE,"E38")])]});
            var Q229;
            Q229=makeQuery(id+"F5.opExtrude","SWEPT_BODY",BODY,{"disambiguationData":[OSD([sQuery(id+"F0.wireOp",EDGE,"E24"),sQuery(id+"F0.wireOp",EDGE,"E29"),sQuery(id+"F0.wireOp",EDGE,"E38")])]});
            var Q230;
            Q230=makeQuery(id+"F5.opExtrude","SWEPT_BODY",BODY,{"disambiguationData":[OSD([sQuery(id+"F0.wireOp",EDGE,"E24"),sQuery(id+"F0.wireOp",EDGE,"E28"),sQuery(id+"F0.wireOp",EDGE,"E30")])]});
            var Q231;
            Q231=makeQuery(id+"F5.opExtrude","SWEPT_BODY",BODY,{"disambiguationData":[OSD([sQuery(id+"F0.wireOp",EDGE,"E24"),sQuery(id+"F0.wireOp",EDGE,"E26"),sQuery(id+"F0.wireOp",EDGE,"E30")])]});
            var Q232;
            Q232=makeQuery(id+"F5.opExtrude","SWEPT_BODY",BODY,{"disambiguationData":[OSD([sQuery(id+"F0.wireOp",EDGE,"E25"),sQuery(id+"F0.wireOp",EDGE,"E29"),sQuery(id+"F0.wireOp",EDGE,"E30")])]});
            var Q233;
            Q233=makeQuery(id+"F5.opExtrude","SWEPT_BODY",BODY,{"disambiguationData":[OSD([sQuery(id+"F0.wireOp",EDGE,"E25"),sQuery(id+"F0.wireOp",EDGE,"E27"),sQuery(id+"F0.wireOp",EDGE,"E30")])]});
            var Q234;
            Q234=makeQuery(id+"F5.opExtrude","SWEPT_BODY",BODY,{"disambiguationData":[OSD([sQuery(id+"F0.wireOp",EDGE,"E25"),sQuery(id+"F0.wireOp",EDGE,"E26"),sQuery(id+"F0.wireOp",EDGE,"E38")])]});
            var Q235;
            Q235=makeQuery(id+"F5.opExtrude","SWEPT_BODY",BODY,{"disambiguationData":[OSD([sQuery(id+"F0.wireOp",EDGE,"E26"),sQuery(id+"F0.wireOp",EDGE,"E28"),sQuery(id+"F0.wireOp",EDGE,"E30")])]});
            var Q236;
            Q236=makeQuery(id+"F5.opExtrude","SWEPT_BODY",BODY,{"disambiguationData":[OSD([sQuery(id+"F0.wireOp",EDGE,"E26"),sQuery(id+"F0.wireOp",EDGE,"E27"),sQuery(id+"F0.wireOp",EDGE,"E38")])]});
            var Q237;
            Q237=makeQuery(id+"F5.opExtrude","SWEPT_BODY",BODY,{"disambiguationData":[OSD([sQuery(id+"F0.wireOp",EDGE,"E27"),sQuery(id+"F0.wireOp",EDGE,"E29"),sQuery(id+"F0.wireOp",EDGE,"E30")])]});
            var Q238;
            Q238=makeQuery(id+"F5.opExtrude","SWEPT_BODY",BODY,{"disambiguationData":[OSD([sQuery(id+"F0.wireOp",EDGE,"E27"),sQuery(id+"F0.wireOp",EDGE,"E28"),sQuery(id+"F0.wireOp",EDGE,"E38")])]});
            var Q239;
            Q239=makeQuery(id+"F5.opExtrude","SWEPT_BODY",BODY,{"disambiguationData":[OSD([sQuery(id+"F0.wireOp",EDGE,"E28"),sQuery(id+"F0.wireOp",EDGE,"E29"),sQuery(id+"F0.wireOp",EDGE,"E38")])]});
            var Q240;
            Q240=makeQuery(id+"F10.opExtrude","SWEPT_BODY",BODY,{"disambiguationData":[OSD([sQuery(id+"F9.wireOp",EDGE,"E155.0")])]});
            var Q241;
            Q241=qCreatedBy(id+"F13.planeOp",FACE);
            mirror(context, id + "F14", {"entities" : qUnion([Q0, Q1, Q2, Q3, Q4, Q5, Q6, Q7, Q8, Q9, Q10, Q11, Q12, Q13, Q14, Q15, Q16, Q17, Q18, Q19, Q20, Q21, Q22, Q23, Q24, Q25, Q26, Q27, Q28, Q29, Q30, Q31, Q32, Q33, Q34, Q35, Q36, Q37, Q38, Q39, Q40, Q41, Q42, Q43, Q44, Q45, Q46, Q47, Q48, Q49, Q50, Q51, Q52, Q53, Q54, Q55, Q56, Q57, Q58, Q59, Q60, Q61, Q62, Q63, Q64, Q65, Q66, Q67, Q68, Q69, Q70, Q71, Q72, Q73, Q74, Q75, Q76, Q77, Q78, Q79, Q80, Q81, Q82, Q83, Q84, Q85, Q86, Q87, Q88, Q89, Q90, Q91, Q92, Q93, Q94, Q95, Q96, Q97, Q98, Q99, Q100, Q101, Q102, Q103, Q104, Q105, Q106, Q107, Q108, Q109, Q110, Q111, Q112, Q113, Q114, Q115, Q116, Q117, Q118, Q119, Q120, Q121, Q122, Q123, Q124, Q125, Q126, Q127, Q128, Q129, Q130, Q131, Q132, Q133, Q134, Q135, Q136, Q137, Q138, Q139, Q140, Q141, Q142, Q143, Q144, Q145, Q146, Q147, Q148, Q149, Q150, Q151, Q152, Q153, Q154, Q155, Q156, Q157, Q158, Q159, Q160, Q161, Q162, Q163, Q164, Q165, Q166, Q167, Q168, Q169, Q170, Q171, Q172, Q173, Q174, Q175, Q176, Q177, Q178, Q179, Q180, Q181, Q182, Q183, Q184, Q185, Q186, Q187, Q188, Q189, Q190, Q191, Q192, Q193, Q194, Q195, Q196, Q197, Q198, Q199, Q200, Q201, Q202, Q203, Q204, Q205, Q206, Q207, Q208, Q209, Q210, Q211, Q212, Q213, Q214, Q215, Q216, Q217, Q218, Q219, Q220, Q221, Q222, Q223, Q224, Q225, Q226, Q227, Q228, Q229, Q230, Q231, Q232, Q233, Q234, Q235, Q236, Q237, Q238, Q239, Q240]), "mirrorPlane" : qUnion([Q241])});
        }
        {
            var Q0;
            Q0=sQuery(id+"F11.wireOp",EDGE,"E156.0");
            var Q1;
            Q1=sQuery(id+"F11.wireOp",EDGE,"E158.0");
            extrude(context, id + "F15", {"bodyType" : ToolBodyType.SURFACE, "surfaceEntities" : qUnion([Q0, Q1]), "oppositeDirection" : true, "depth" : 40 * mm});
        }
    });
